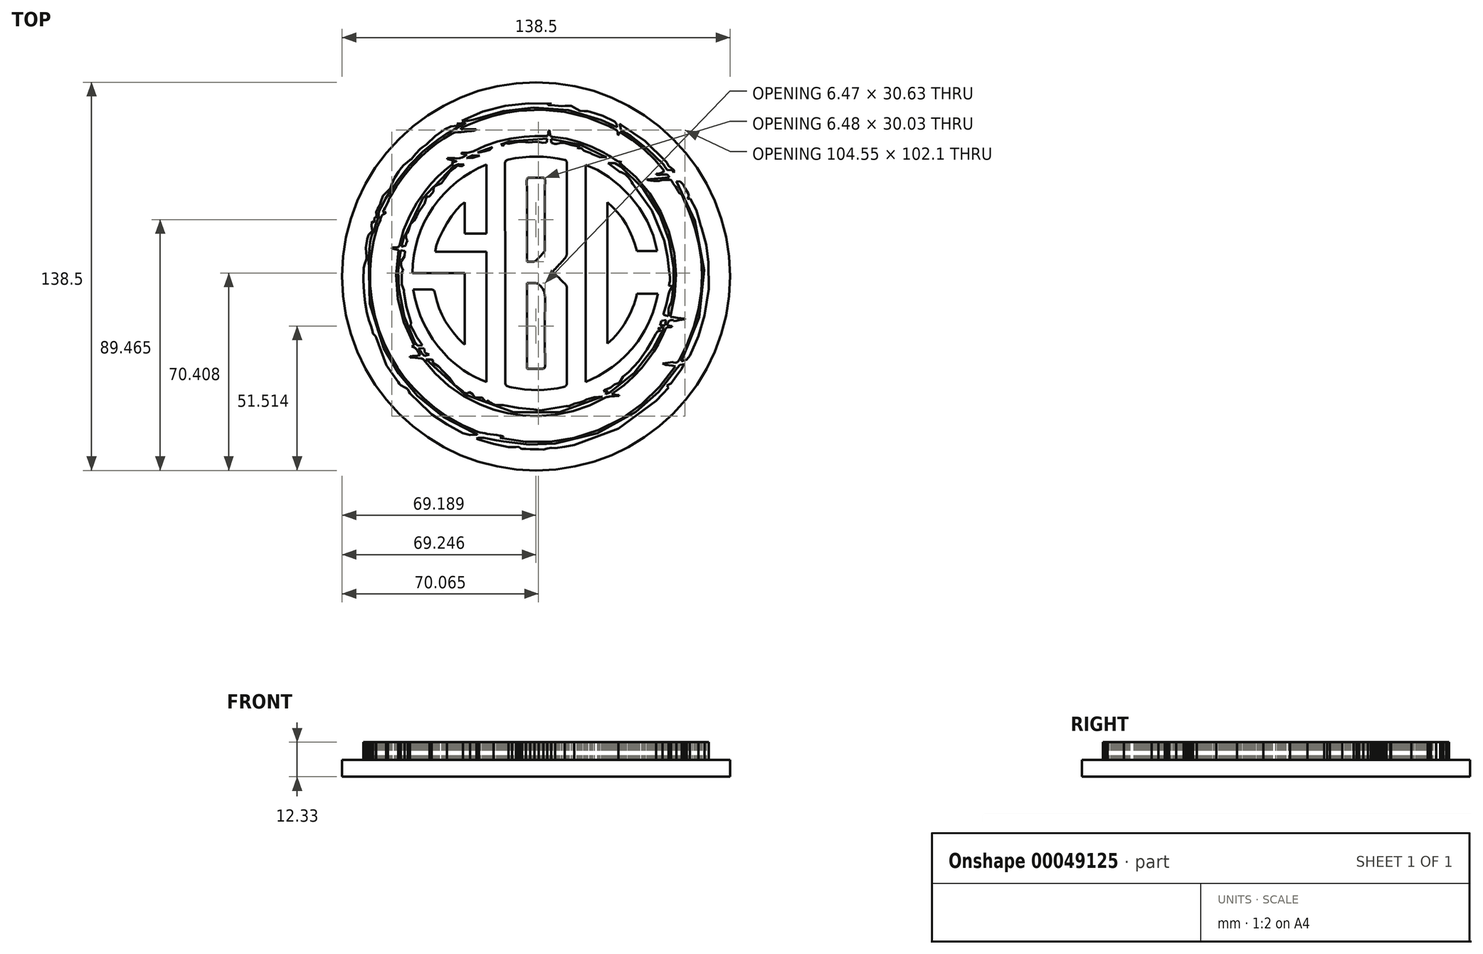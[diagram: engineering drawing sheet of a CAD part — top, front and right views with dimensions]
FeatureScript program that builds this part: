
annotation { "Feature Type Name" : "Feature", "Feature Type Description" : "" }
export const myFeature = defineFeature(function(context is Context, id is Id, definition is map)
    precondition{}
    {
        {
            var Q0;
            Q0=qCreatedBy(makeId("Top.planeOp"),FACE);
            var sketch = newSketch(context, id + "F0", { "sketchPlane" : qUnion([Q0])});
            skLineSegment(sketch, "E0", {"start": v(-53.55, 22.87) * mm, "end": v(-53.9, 22.9) * mm});
            skLineSegment(sketch, "E1", {"start": v(-53.9, 22.9) * mm, "end": v(-54.2, 22.94) * mm});
            skLineSegment(sketch, "E2", {"start": v(-54.2, 22.94) * mm, "end": v(-54.48, 22.97) * mm});
            skLineSegment(sketch, "E3", {"start": v(-54.48, 22.97) * mm, "end": v(-54.75, 23) * mm});
            skLineSegment(sketch, "E4", {"start": v(-54.75, 23) * mm, "end": v(-54.33, 23.74) * mm});
            skLineSegment(sketch, "E5", {"start": v(-54.33, 23.74) * mm, "end": v(-53.9, 24.47) * mm});
            skLineSegment(sketch, "E6", {"start": v(-53.9, 24.47) * mm, "end": v(-53.5, 25.2) * mm});
            skLineSegment(sketch, "E7", {"start": v(-53.5, 25.2) * mm, "end": v(-53.1, 25.95) * mm});
            skLineSegment(sketch, "E8", {"start": v(-53.1, 25.95) * mm, "end": v(-52.87, 26.48) * mm});
            skLineSegment(sketch, "E9", {"start": v(-52.87, 26.48) * mm, "end": v(-52.68, 27.03) * mm});
            skLineSegment(sketch, "E10", {"start": v(-52.68, 27.03) * mm, "end": v(-52.47, 27.58) * mm});
            skLineSegment(sketch, "E11", {"start": v(-52.47, 27.58) * mm, "end": v(-52.23, 28.1) * mm});
            skLineSegment(sketch, "E12", {"start": v(-52.23, 28.1) * mm, "end": v(-49.87, 32.12) * mm});
            skLineSegment(sketch, "E13", {"start": v(-49.87, 32.12) * mm, "end": v(-47.2, 35.9) * mm});
            skLineSegment(sketch, "E14", {"start": v(-47.2, 35.9) * mm, "end": v(-44.24, 39.46) * mm});
            skLineSegment(sketch, "E15", {"start": v(-44.24, 39.46) * mm, "end": v(-41, 42.8) * mm});
            skLineSegment(sketch, "E16", {"start": v(-41, 42.8) * mm, "end": v(-38.46, 45.1) * mm});
            skLineSegment(sketch, "E17", {"start": v(-38.46, 45.1) * mm, "end": v(-35.8, 47.26) * mm});
            skLineSegment(sketch, "E18", {"start": v(-35.8, 47.26) * mm, "end": v(-33, 49.21) * mm});
            skLineSegment(sketch, "E19", {"start": v(-33, 49.21) * mm, "end": v(-30.05, 50.93) * mm});
            skLineSegment(sketch, "E20", {"start": v(-30.05, 50.93) * mm, "end": v(-29.02, 51.28) * mm});
            skLineSegment(sketch, "E21", {"start": v(-29.02, 51.28) * mm, "end": v(-27.88, 51.44) * mm});
            skLineSegment(sketch, "E22", {"start": v(-27.88, 51.44) * mm, "end": v(-26.7, 51.5) * mm});
            skLineSegment(sketch, "E23", {"start": v(-26.7, 51.5) * mm, "end": v(-25.54, 51.6) * mm});
            skLineSegment(sketch, "E24", {"start": v(-25.54, 51.6) * mm, "end": v(-24.72, 51.7) * mm});
            skLineSegment(sketch, "E25", {"start": v(-24.72, 51.7) * mm, "end": v(-23.91, 51.8) * mm});
            skLineSegment(sketch, "E26", {"start": v(-23.91, 51.8) * mm, "end": v(-23.1, 51.9) * mm});
            skLineSegment(sketch, "E27", {"start": v(-23.1, 51.9) * mm, "end": v(-22.29, 52.01) * mm});
            skLineSegment(sketch, "E28", {"start": v(-22.29, 52.01) * mm, "end": v(-22.06, 52.06) * mm});
            skLineSegment(sketch, "E29", {"start": v(-22.06, 52.06) * mm, "end": v(-21.84, 52.14) * mm});
            skLineSegment(sketch, "E30", {"start": v(-21.84, 52.14) * mm, "end": v(-21.62, 52.23) * mm});
            skLineSegment(sketch, "E31", {"start": v(-21.62, 52.23) * mm, "end": v(-21.4, 52.31) * mm});
            skLineSegment(sketch, "E32", {"start": v(-21.4, 52.31) * mm, "end": v(-21.4, 52.37) * mm});
            skLineSegment(sketch, "E33", {"start": v(-21.4, 52.37) * mm, "end": v(-21.41, 52.43) * mm});
            skLineSegment(sketch, "E34", {"start": v(-21.41, 52.43) * mm, "end": v(-21.42, 52.49) * mm});
            skLineSegment(sketch, "E35", {"start": v(-21.42, 52.49) * mm, "end": v(-21.42, 52.54) * mm});
            skLineSegment(sketch, "E36", {"start": v(-21.42, 52.54) * mm, "end": v(-22.76, 52.54) * mm});
            skLineSegment(sketch, "E37", {"start": v(-22.76, 52.54) * mm, "end": v(-24.1, 52.54) * mm});
            skLineSegment(sketch, "E38", {"start": v(-24.1, 52.54) * mm, "end": v(-25.44, 52.54) * mm});
            skLineSegment(sketch, "E39", {"start": v(-25.44, 52.54) * mm, "end": v(-26.78, 52.54) * mm});
            skLineSegment(sketch, "E40", {"start": v(-26.78, 52.54) * mm, "end": v(-26.8, 52.61) * mm});
            skLineSegment(sketch, "E41", {"start": v(-26.8, 52.61) * mm, "end": v(-26.8, 52.68) * mm});
            skLineSegment(sketch, "E42", {"start": v(-26.8, 52.68) * mm, "end": v(-26.82, 52.74) * mm});
            skLineSegment(sketch, "E43", {"start": v(-26.82, 52.74) * mm, "end": v(-26.83, 52.81) * mm});
            skLineSegment(sketch, "E44", {"start": v(-26.83, 52.81) * mm, "end": v(-26.31, 53.08) * mm});
            skLineSegment(sketch, "E45", {"start": v(-26.31, 53.08) * mm, "end": v(-25.8, 53.35) * mm});
            skLineSegment(sketch, "E46", {"start": v(-25.8, 53.35) * mm, "end": v(-25.27, 53.61) * mm});
            skLineSegment(sketch, "E47", {"start": v(-25.27, 53.61) * mm, "end": v(-24.74, 53.87) * mm});
            skLineSegment(sketch, "E48", {"start": v(-24.74, 53.87) * mm, "end": v(-20.25, 55.7) * mm});
            skLineSegment(sketch, "E49", {"start": v(-20.25, 55.7) * mm, "end": v(-15.66, 57.19) * mm});
            skLineSegment(sketch, "E50", {"start": v(-15.66, 57.19) * mm, "end": v(-10.96, 58.3) * mm});
            skLineSegment(sketch, "E51", {"start": v(-10.96, 58.3) * mm, "end": v(-6.17, 59.06) * mm});
            skLineSegment(sketch, "E52", {"start": v(-6.17, 59.06) * mm, "end": v(2.1, 59.44) * mm});
            skLineSegment(sketch, "E53", {"start": v(2.1, 59.44) * mm, "end": v(10.16, 58.67) * mm});
            skLineSegment(sketch, "E54", {"start": v(10.16, 58.67) * mm, "end": v(18.04, 56.78) * mm});
            skLineSegment(sketch, "E55", {"start": v(18.04, 56.78) * mm, "end": v(25.74, 53.76) * mm});
            skLineSegment(sketch, "E56", {"start": v(25.74, 53.76) * mm, "end": v(26.35, 53.46) * mm});
            skLineSegment(sketch, "E57", {"start": v(26.35, 53.46) * mm, "end": v(26.96, 53.13) * mm});
            skLineSegment(sketch, "E58", {"start": v(26.96, 53.13) * mm, "end": v(27.57, 52.8) * mm});
            skLineSegment(sketch, "E59", {"start": v(27.57, 52.8) * mm, "end": v(28.18, 52.5) * mm});
            skLineSegment(sketch, "E60", {"start": v(28.18, 52.5) * mm, "end": v(28.6, 52.27) * mm});
            skLineSegment(sketch, "E61", {"start": v(28.6, 52.27) * mm, "end": v(28.92, 51.98) * mm});
            skLineSegment(sketch, "E62", {"start": v(28.92, 51.98) * mm, "end": v(29.1, 51.6) * mm});
            skLineSegment(sketch, "E63", {"start": v(29.1, 51.6) * mm, "end": v(29.1, 51.1) * mm});
            skLineSegment(sketch, "E64", {"start": v(29.1, 51.1) * mm, "end": v(29.1, 50.97) * mm});
            skLineSegment(sketch, "E65", {"start": v(29.1, 50.97) * mm, "end": v(29.15, 50.8) * mm});
            skLineSegment(sketch, "E66", {"start": v(29.15, 50.8) * mm, "end": v(29.22, 50.6) * mm});
            skLineSegment(sketch, "E67", {"start": v(29.22, 50.6) * mm, "end": v(29.3, 50.33) * mm});
            skLineSegment(sketch, "E68", {"start": v(29.3, 50.33) * mm, "end": v(29.47, 50.68) * mm});
            skLineSegment(sketch, "E69", {"start": v(29.47, 50.68) * mm, "end": v(29.62, 50.97) * mm});
            skLineSegment(sketch, "E70", {"start": v(29.62, 50.97) * mm, "end": v(29.75, 51.25) * mm});
            skLineSegment(sketch, "E71", {"start": v(29.75, 51.25) * mm, "end": v(29.9, 51.54) * mm});
            skLineSegment(sketch, "E72", {"start": v(29.9, 51.54) * mm, "end": v(34.35, 48.61) * mm});
            skLineSegment(sketch, "E73", {"start": v(34.35, 48.61) * mm, "end": v(38.5, 45.35) * mm});
            skLineSegment(sketch, "E74", {"start": v(38.5, 45.35) * mm, "end": v(42.34, 41.72) * mm});
            skLineSegment(sketch, "E75", {"start": v(42.34, 41.72) * mm, "end": v(45.83, 37.66) * mm});
            skLineSegment(sketch, "E76", {"start": v(45.83, 37.66) * mm, "end": v(45.5, 37.43) * mm});
            skLineSegment(sketch, "E77", {"start": v(45.5, 37.43) * mm, "end": v(45.17, 37.19) * mm});
            skLineSegment(sketch, "E78", {"start": v(45.17, 37.19) * mm, "end": v(44.83, 36.97) * mm});
            skLineSegment(sketch, "E79", {"start": v(44.83, 36.97) * mm, "end": v(44.48, 36.8) * mm});
            skLineSegment(sketch, "E80", {"start": v(44.48, 36.8) * mm, "end": v(44.09, 36.7) * mm});
            skLineSegment(sketch, "E81", {"start": v(44.09, 36.7) * mm, "end": v(43.68, 36.66) * mm});
            skLineSegment(sketch, "E82", {"start": v(43.68, 36.66) * mm, "end": v(43.26, 36.63) * mm});
            skLineSegment(sketch, "E83", {"start": v(43.26, 36.63) * mm, "end": v(42.85, 36.6) * mm});
            skLineSegment(sketch, "E84", {"start": v(42.85, 36.6) * mm, "end": v(42.85, 36.53) * mm});
            skLineSegment(sketch, "E85", {"start": v(42.85, 36.53) * mm, "end": v(42.84, 36.47) * mm});
            skLineSegment(sketch, "E86", {"start": v(42.84, 36.47) * mm, "end": v(42.84, 36.4) * mm});
            skLineSegment(sketch, "E87", {"start": v(42.84, 36.4) * mm, "end": v(42.84, 36.34) * mm});
            skLineSegment(sketch, "E88", {"start": v(42.84, 36.34) * mm, "end": v(43.05, 36.3) * mm});
            skLineSegment(sketch, "E89", {"start": v(43.05, 36.3) * mm, "end": v(43.27, 36.27) * mm});
            skLineSegment(sketch, "E90", {"start": v(43.27, 36.27) * mm, "end": v(43.48, 36.24) * mm});
            skLineSegment(sketch, "E91", {"start": v(43.48, 36.24) * mm, "end": v(43.7, 36.24) * mm});
            skLineSegment(sketch, "E92", {"start": v(43.7, 36.24) * mm, "end": v(44.27, 36.27) * mm});
            skLineSegment(sketch, "E93", {"start": v(44.27, 36.27) * mm, "end": v(44.85, 36.3) * mm});
            skLineSegment(sketch, "E94", {"start": v(44.85, 36.3) * mm, "end": v(45.43, 36.34) * mm});
            skLineSegment(sketch, "E95", {"start": v(45.43, 36.34) * mm, "end": v(46, 36.4) * mm});
            skLineSegment(sketch, "E96", {"start": v(46, 36.4) * mm, "end": v(46.49, 36.38) * mm});
            skLineSegment(sketch, "E97", {"start": v(46.49, 36.38) * mm, "end": v(46.91, 36.23) * mm});
            skLineSegment(sketch, "E98", {"start": v(46.91, 36.23) * mm, "end": v(47.28, 35.9) * mm});
            skLineSegment(sketch, "E99", {"start": v(47.28, 35.9) * mm, "end": v(47.62, 35.4) * mm});
            skLineSegment(sketch, "E100", {"start": v(47.62, 35.4) * mm, "end": v(45.56, 35.2) * mm});
            skLineSegment(sketch, "E101", {"start": v(45.56, 35.2) * mm, "end": v(43.53, 35) * mm});
            skLineSegment(sketch, "E102", {"start": v(43.53, 35) * mm, "end": v(41.53, 34.8) * mm});
            skLineSegment(sketch, "E103", {"start": v(41.53, 34.8) * mm, "end": v(39.53, 34.6) * mm});
            skLineSegment(sketch, "E104", {"start": v(39.53, 34.6) * mm, "end": v(39.52, 34.56) * mm});
            skLineSegment(sketch, "E105", {"start": v(39.52, 34.56) * mm, "end": v(39.52, 34.52) * mm});
            skLineSegment(sketch, "E106", {"start": v(39.52, 34.52) * mm, "end": v(39.51, 34.48) * mm});
            skLineSegment(sketch, "E107", {"start": v(39.51, 34.48) * mm, "end": v(39.5, 34.44) * mm});
            skLineSegment(sketch, "E108", {"start": v(39.5, 34.44) * mm, "end": v(39.88, 34.4) * mm});
            skLineSegment(sketch, "E109", {"start": v(39.88, 34.4) * mm, "end": v(40.25, 34.35) * mm});
            skLineSegment(sketch, "E110", {"start": v(40.25, 34.35) * mm, "end": v(40.62, 34.3) * mm});
            skLineSegment(sketch, "E111", {"start": v(40.62, 34.3) * mm, "end": v(41, 34.24) * mm});
            skLineSegment(sketch, "E112", {"start": v(41, 34.24) * mm, "end": v(41.94, 34.1) * mm});
            skLineSegment(sketch, "E113", {"start": v(41.94, 34.1) * mm, "end": v(42.87, 34.04) * mm});
            skLineSegment(sketch, "E114", {"start": v(42.87, 34.04) * mm, "end": v(43.81, 34.1) * mm});
            skLineSegment(sketch, "E115", {"start": v(43.81, 34.1) * mm, "end": v(44.76, 34.27) * mm});
            skLineSegment(sketch, "E116", {"start": v(44.76, 34.27) * mm, "end": v(45.45, 34.4) * mm});
            skLineSegment(sketch, "E117", {"start": v(45.45, 34.4) * mm, "end": v(46.16, 34.45) * mm});
            skLineSegment(sketch, "E118", {"start": v(46.16, 34.45) * mm, "end": v(46.88, 34.46) * mm});
            skLineSegment(sketch, "E119", {"start": v(46.88, 34.46) * mm, "end": v(47.6, 34.47) * mm});
            skLineSegment(sketch, "E120", {"start": v(47.6, 34.47) * mm, "end": v(47.9, 34.44) * mm});
            skLineSegment(sketch, "E121", {"start": v(47.9, 34.44) * mm, "end": v(48.17, 34.33) * mm});
            skLineSegment(sketch, "E122", {"start": v(48.17, 34.33) * mm, "end": v(48.4, 34.12) * mm});
            skLineSegment(sketch, "E123", {"start": v(48.4, 34.12) * mm, "end": v(48.57, 33.79) * mm});
            skLineSegment(sketch, "E124", {"start": v(48.57, 33.79) * mm, "end": v(48.8, 33.32) * mm});
            skLineSegment(sketch, "E125", {"start": v(48.8, 33.32) * mm, "end": v(49.1, 32.88) * mm});
            skLineSegment(sketch, "E126", {"start": v(49.1, 32.88) * mm, "end": v(49.44, 32.46) * mm});
            skLineSegment(sketch, "E127", {"start": v(49.44, 32.46) * mm, "end": v(49.8, 32.07) * mm});
            skLineSegment(sketch, "E128", {"start": v(49.8, 32.07) * mm, "end": v(50.25, 31.34) * mm});
            skLineSegment(sketch, "E129", {"start": v(50.25, 31.34) * mm, "end": v(50.59, 30.51) * mm});
            skLineSegment(sketch, "E130", {"start": v(50.59, 30.51) * mm, "end": v(51.06, 29.8) * mm});
            skLineSegment(sketch, "E131", {"start": v(51.06, 29.8) * mm, "end": v(51.93, 29.41) * mm});
            skLineSegment(sketch, "E132", {"start": v(51.93, 29.41) * mm, "end": v(51.96, 29.4) * mm});
            skLineSegment(sketch, "E133", {"start": v(51.96, 29.4) * mm, "end": v(51.98, 29.36) * mm});
            skLineSegment(sketch, "E134", {"start": v(51.98, 29.36) * mm, "end": v(52, 29.3) * mm});
            skLineSegment(sketch, "E135", {"start": v(52, 29.3) * mm, "end": v(52.02, 29.26) * mm});
            skLineSegment(sketch, "E136", {"start": v(52.02, 29.26) * mm, "end": v(53.24, 26.24) * mm});
            skLineSegment(sketch, "E137", {"start": v(53.24, 26.24) * mm, "end": v(54.48, 23.23) * mm});
            skLineSegment(sketch, "E138", {"start": v(54.48, 23.23) * mm, "end": v(55.67, 20.2) * mm});
            skLineSegment(sketch, "E139", {"start": v(55.67, 20.2) * mm, "end": v(56.73, 17.13) * mm});
            skLineSegment(sketch, "E140", {"start": v(56.73, 17.13) * mm, "end": v(58.14, 11.63) * mm});
            skLineSegment(sketch, "E141", {"start": v(58.14, 11.63) * mm, "end": v(58.96, 6.05) * mm});
            skLineSegment(sketch, "E142", {"start": v(58.96, 6.05) * mm, "end": v(59.23, 0.42) * mm});
            skLineSegment(sketch, "E143", {"start": v(59.23, 0.42) * mm, "end": v(58.97, -5.27) * mm});
            skLineSegment(sketch, "E144", {"start": v(58.97, -5.27) * mm, "end": v(58.02, -11.75) * mm});
            skLineSegment(sketch, "E145", {"start": v(58.02, -11.75) * mm, "end": v(56.38, -18) * mm});
            skLineSegment(sketch, "E146", {"start": v(56.38, -18) * mm, "end": v(54.05, -24.02) * mm});
            skLineSegment(sketch, "E147", {"start": v(54.05, -24.02) * mm, "end": v(51.08, -29.84) * mm});
            skLineSegment(sketch, "E148", {"start": v(51.08, -29.84) * mm, "end": v(50.67, -30.45) * mm});
            skLineSegment(sketch, "E149", {"start": v(50.67, -30.45) * mm, "end": v(50.28, -30.76) * mm});
            skLineSegment(sketch, "E150", {"start": v(50.28, -30.76) * mm, "end": v(49.77, -30.8) * mm});
            skLineSegment(sketch, "E151", {"start": v(49.77, -30.8) * mm, "end": v(49.02, -30.65) * mm});
            skLineSegment(sketch, "E152", {"start": v(49.02, -30.65) * mm, "end": v(48.97, -30.64) * mm});
            skLineSegment(sketch, "E153", {"start": v(48.97, -30.64) * mm, "end": v(48.93, -30.62) * mm});
            skLineSegment(sketch, "E154", {"start": v(48.93, -30.62) * mm, "end": v(48.89, -30.61) * mm});
            skLineSegment(sketch, "E155", {"start": v(48.89, -30.61) * mm, "end": v(48.85, -30.61) * mm});
            skLineSegment(sketch, "E156", {"start": v(48.85, -30.61) * mm, "end": v(47.96, -30.73) * mm});
            skLineSegment(sketch, "E157", {"start": v(47.96, -30.73) * mm, "end": v(47.06, -30.86) * mm});
            skLineSegment(sketch, "E158", {"start": v(47.06, -30.86) * mm, "end": v(46.14, -30.98) * mm});
            skLineSegment(sketch, "E159", {"start": v(46.14, -30.98) * mm, "end": v(45.2, -31.11) * mm});
            skLineSegment(sketch, "E160", {"start": v(45.2, -31.11) * mm, "end": v(46.27, -31.6) * mm});
            skLineSegment(sketch, "E161", {"start": v(46.27, -31.6) * mm, "end": v(47.41, -31.78) * mm});
            skLineSegment(sketch, "E162", {"start": v(47.41, -31.78) * mm, "end": v(48.58, -31.86) * mm});
            skLineSegment(sketch, "E163", {"start": v(48.58, -31.86) * mm, "end": v(49.73, -32.09) * mm});
            skLineSegment(sketch, "E164", {"start": v(49.73, -32.09) * mm, "end": v(44.16, -39.36) * mm});
            skLineSegment(sketch, "E165", {"start": v(44.16, -39.36) * mm, "end": v(37.75, -45.58) * mm});
            skLineSegment(sketch, "E166", {"start": v(37.75, -45.58) * mm, "end": v(30.48, -50.73) * mm});
            skLineSegment(sketch, "E167", {"start": v(30.48, -50.73) * mm, "end": v(22.34, -54.8) * mm});
            skLineSegment(sketch, "E168", {"start": v(22.34, -54.8) * mm, "end": v(13.71, -57.6) * mm});
            skLineSegment(sketch, "E169", {"start": v(13.71, -57.6) * mm, "end": v(4.95, -59) * mm});
            skLineSegment(sketch, "E170", {"start": v(4.95, -59) * mm, "end": v(-3.93, -59) * mm});
            skLineSegment(sketch, "E171", {"start": v(-3.93, -59) * mm, "end": v(-12.92, -57.63) * mm});
            skLineSegment(sketch, "E172", {"start": v(-12.92, -57.63) * mm, "end": v(-12.6, -57.53) * mm});
            skLineSegment(sketch, "E173", {"start": v(-12.6, -57.53) * mm, "end": v(-12.26, -57.44) * mm});
            skLineSegment(sketch, "E174", {"start": v(-12.26, -57.44) * mm, "end": v(-11.93, -57.35) * mm});
            skLineSegment(sketch, "E175", {"start": v(-11.93, -57.35) * mm, "end": v(-11.6, -57.25) * mm});
            skLineSegment(sketch, "E176", {"start": v(-11.6, -57.25) * mm, "end": v(-11.6, -57.22) * mm});
            skLineSegment(sketch, "E177", {"start": v(-11.6, -57.22) * mm, "end": v(-11.6, -57.19) * mm});
            skLineSegment(sketch, "E178", {"start": v(-11.6, -57.19) * mm, "end": v(-11.59, -57.16) * mm});
            skLineSegment(sketch, "E179", {"start": v(-11.59, -57.16) * mm, "end": v(-11.58, -57.12) * mm});
            skLineSegment(sketch, "E180", {"start": v(-11.58, -57.12) * mm, "end": v(-11.85, -57.07) * mm});
            skLineSegment(sketch, "E181", {"start": v(-11.85, -57.07) * mm, "end": v(-12.1, -57.02) * mm});
            skLineSegment(sketch, "E182", {"start": v(-12.1, -57.02) * mm, "end": v(-12.37, -56.96) * mm});
            skLineSegment(sketch, "E183", {"start": v(-12.37, -56.96) * mm, "end": v(-12.63, -56.91) * mm});
            skLineSegment(sketch, "E184", {"start": v(-12.63, -56.91) * mm, "end": v(-12.7, -56.9) * mm});
            skLineSegment(sketch, "E185", {"start": v(-12.7, -56.9) * mm, "end": v(-12.76, -56.9) * mm});
            skLineSegment(sketch, "E186", {"start": v(-12.76, -56.9) * mm, "end": v(-12.83, -56.9) * mm});
            skLineSegment(sketch, "E187", {"start": v(-12.83, -56.9) * mm, "end": v(-12.9, -56.88) * mm});
            skLineSegment(sketch, "E188", {"start": v(-12.9, -56.88) * mm, "end": v(-14, -56.57) * mm});
            skLineSegment(sketch, "E189", {"start": v(-14, -56.57) * mm, "end": v(-15.15, -56.46) * mm});
            skLineSegment(sketch, "E190", {"start": v(-15.15, -56.46) * mm, "end": v(-16.3, -56.4) * mm});
            skLineSegment(sketch, "E191", {"start": v(-16.3, -56.4) * mm, "end": v(-17.4, -56.22) * mm});
            skLineSegment(sketch, "E192", {"start": v(-17.4, -56.22) * mm, "end": v(-18.27, -56.04) * mm});
            skLineSegment(sketch, "E193", {"start": v(-18.27, -56.04) * mm, "end": v(-19.14, -55.9) * mm});
            skLineSegment(sketch, "E194", {"start": v(-19.14, -55.9) * mm, "end": v(-20, -55.7) * mm});
            skLineSegment(sketch, "E195", {"start": v(-20, -55.7) * mm, "end": v(-20.85, -55.41) * mm});
            skLineSegment(sketch, "E196", {"start": v(-20.85, -55.41) * mm, "end": v(-21.72, -55.03) * mm});
            skLineSegment(sketch, "E197", {"start": v(-21.72, -55.03) * mm, "end": v(-22.6, -54.67) * mm});
            skLineSegment(sketch, "E198", {"start": v(-22.6, -54.67) * mm, "end": v(-23.5, -54.3) * mm});
            skLineSegment(sketch, "E199", {"start": v(-23.5, -54.3) * mm, "end": v(-24.37, -53.93) * mm});
            skLineSegment(sketch, "E200", {"start": v(-24.37, -53.93) * mm, "end": v(-25.24, -53.54) * mm});
            skLineSegment(sketch, "E201", {"start": v(-25.24, -53.54) * mm, "end": v(-26.1, -53.13) * mm});
            skLineSegment(sketch, "E202", {"start": v(-26.1, -53.13) * mm, "end": v(-26.96, -52.7) * mm});
            skLineSegment(sketch, "E203", {"start": v(-26.96, -52.7) * mm, "end": v(-27.8, -52.27) * mm});
            skLineSegment(sketch, "E204", {"start": v(-27.8, -52.27) * mm, "end": v(-32.17, -49.71) * mm});
            skLineSegment(sketch, "E205", {"start": v(-32.17, -49.71) * mm, "end": v(-36.27, -46.8) * mm});
            skLineSegment(sketch, "E206", {"start": v(-36.27, -46.8) * mm, "end": v(-40.11, -43.57) * mm});
            skLineSegment(sketch, "E207", {"start": v(-40.11, -43.57) * mm, "end": v(-43.7, -40) * mm});
            skLineSegment(sketch, "E208", {"start": v(-43.7, -40) * mm, "end": v(-46.75, -36.4) * mm});
            skLineSegment(sketch, "E209", {"start": v(-46.75, -36.4) * mm, "end": v(-49.5, -32.6) * mm});
            skLineSegment(sketch, "E210", {"start": v(-49.5, -32.6) * mm, "end": v(-51.93, -28.58) * mm});
            skLineSegment(sketch, "E211", {"start": v(-51.93, -28.58) * mm, "end": v(-54.04, -24.35) * mm});
            skLineSegment(sketch, "E212", {"start": v(-54.04, -24.35) * mm, "end": v(-56.06, -19.25) * mm});
            skLineSegment(sketch, "E213", {"start": v(-56.06, -19.25) * mm, "end": v(-57.6, -14.04) * mm});
            skLineSegment(sketch, "E214", {"start": v(-57.6, -14.04) * mm, "end": v(-58.64, -8.7) * mm});
            skLineSegment(sketch, "E215", {"start": v(-58.64, -8.7) * mm, "end": v(-59.2, -3.25) * mm});
            skLineSegment(sketch, "E216", {"start": v(-59.2, -3.25) * mm, "end": v(-59.26, 2.15) * mm});
            skLineSegment(sketch, "E217", {"start": v(-59.26, 2.15) * mm, "end": v(-58.83, 7.48) * mm});
            skLineSegment(sketch, "E218", {"start": v(-58.83, 7.48) * mm, "end": v(-57.93, 12.76) * mm});
            skLineSegment(sketch, "E219", {"start": v(-57.93, 12.76) * mm, "end": v(-56.58, 17.97) * mm});
            skLineSegment(sketch, "E220", {"start": v(-56.58, 17.97) * mm, "end": v(-56.58, 18) * mm});
            skLineSegment(sketch, "E221", {"start": v(-56.58, 18) * mm, "end": v(-56.57, 18.01) * mm});
            skLineSegment(sketch, "E222", {"start": v(-56.57, 18.01) * mm, "end": v(-56.56, 18.04) * mm});
            skLineSegment(sketch, "E223", {"start": v(-56.56, 18.04) * mm, "end": v(-56.55, 18.06) * mm});
            skLineSegment(sketch, "E224", {"start": v(-56.55, 18.06) * mm, "end": v(-56.21, 18.74) * mm});
            skLineSegment(sketch, "E225", {"start": v(-56.21, 18.74) * mm, "end": v(-55.85, 19.42) * mm});
            skLineSegment(sketch, "E226", {"start": v(-55.85, 19.42) * mm, "end": v(-55.54, 20.12) * mm});
            skLineSegment(sketch, "E227", {"start": v(-55.54, 20.12) * mm, "end": v(-55.38, 20.9) * mm});
            skLineSegment(sketch, "E228", {"start": v(-55.38, 20.9) * mm, "end": v(-55.24, 21.44) * mm});
            skLineSegment(sketch, "E229", {"start": v(-55.24, 21.44) * mm, "end": v(-54.94, 21.86) * mm});
            skLineSegment(sketch, "E230", {"start": v(-54.94, 21.86) * mm, "end": v(-54.51, 22.18) * mm});
            skLineSegment(sketch, "E231", {"start": v(-54.51, 22.18) * mm, "end": v(-54.02, 22.44) * mm});
            skLineSegment(sketch, "E232", {"start": v(-54.02, 22.44) * mm, "end": v(-53.92, 22.5) * mm});
            skLineSegment(sketch, "E233", {"start": v(-53.92, 22.5) * mm, "end": v(-53.82, 22.6) * mm});
            skLineSegment(sketch, "E234", {"start": v(-53.82, 22.6) * mm, "end": v(-53.7, 22.72) * mm});
            skLineSegment(sketch, "E235", {"start": v(-53.7, 22.72) * mm, "end": v(-53.55, 22.87) * mm});
            skLineSegment(sketch, "E236", {"start": v(27, -42.03) * mm, "end": v(27.25, -41.85) * mm});
            skLineSegment(sketch, "E237", {"start": v(27.25, -41.85) * mm, "end": v(27.46, -41.7) * mm});
            skLineSegment(sketch, "E238", {"start": v(27.46, -41.7) * mm, "end": v(27.65, -41.56) * mm});
            skLineSegment(sketch, "E239", {"start": v(27.65, -41.56) * mm, "end": v(27.83, -41.43) * mm});
            skLineSegment(sketch, "E240", {"start": v(27.83, -41.43) * mm, "end": v(31.4, -38.77) * mm});
            skLineSegment(sketch, "E241", {"start": v(31.4, -38.77) * mm, "end": v(34.7, -35.83) * mm});
            skLineSegment(sketch, "E242", {"start": v(34.7, -35.83) * mm, "end": v(37.74, -32.61) * mm});
            skLineSegment(sketch, "E243", {"start": v(37.74, -32.61) * mm, "end": v(40.5, -29.1) * mm});
            skLineSegment(sketch, "E244", {"start": v(40.5, -29.1) * mm, "end": v(42.11, -26.73) * mm});
            skLineSegment(sketch, "E245", {"start": v(42.11, -26.73) * mm, "end": v(43.58, -24.28) * mm});
            skLineSegment(sketch, "E246", {"start": v(43.58, -24.28) * mm, "end": v(44.9, -21.74) * mm});
            skLineSegment(sketch, "E247", {"start": v(44.9, -21.74) * mm, "end": v(46.06, -19.12) * mm});
            skLineSegment(sketch, "E248", {"start": v(46.06, -19.12) * mm, "end": v(46.27, -18.68) * mm});
            skLineSegment(sketch, "E249", {"start": v(46.27, -18.68) * mm, "end": v(46.54, -18.36) * mm});
            skLineSegment(sketch, "E250", {"start": v(46.54, -18.36) * mm, "end": v(46.9, -18.17) * mm});
            skLineSegment(sketch, "E251", {"start": v(46.9, -18.17) * mm, "end": v(47.4, -18.14) * mm});
            skLineSegment(sketch, "E252", {"start": v(47.4, -18.14) * mm, "end": v(47.7, -18.14) * mm});
            skLineSegment(sketch, "E253", {"start": v(47.7, -18.14) * mm, "end": v(48, -18.09) * mm});
            skLineSegment(sketch, "E254", {"start": v(48, -18.09) * mm, "end": v(48.32, -18.02) * mm});
            skLineSegment(sketch, "E255", {"start": v(48.32, -18.02) * mm, "end": v(48.63, -17.96) * mm});
            skLineSegment(sketch, "E256", {"start": v(48.63, -17.96) * mm, "end": v(48.62, -17.91) * mm});
            skLineSegment(sketch, "E257", {"start": v(48.62, -17.91) * mm, "end": v(48.62, -17.86) * mm});
            skLineSegment(sketch, "E258", {"start": v(48.62, -17.86) * mm, "end": v(48.62, -17.81) * mm});
            skLineSegment(sketch, "E259", {"start": v(48.62, -17.81) * mm, "end": v(48.61, -17.76) * mm});
            skLineSegment(sketch, "E260", {"start": v(48.61, -17.76) * mm, "end": v(48.16, -17.71) * mm});
            skLineSegment(sketch, "E261", {"start": v(48.16, -17.71) * mm, "end": v(47.71, -17.66) * mm});
            skLineSegment(sketch, "E262", {"start": v(47.71, -17.66) * mm, "end": v(47.26, -17.61) * mm});
            skLineSegment(sketch, "E263", {"start": v(47.26, -17.61) * mm, "end": v(46.8, -17.56) * mm});
            skLineSegment(sketch, "E264", {"start": v(46.8, -17.56) * mm, "end": v(47.1, -16.5) * mm});
            skLineSegment(sketch, "E265", {"start": v(47.1, -16.5) * mm, "end": v(47.5, -15.9) * mm});
            skLineSegment(sketch, "E266", {"start": v(47.5, -15.9) * mm, "end": v(48.13, -15.63) * mm});
            skLineSegment(sketch, "E267", {"start": v(48.13, -15.63) * mm, "end": v(49.14, -15.58) * mm});
            skLineSegment(sketch, "E268", {"start": v(49.14, -15.58) * mm, "end": v(49.12, -15.7) * mm});
            skLineSegment(sketch, "E269", {"start": v(49.12, -15.7) * mm, "end": v(49.1, -15.83) * mm});
            skLineSegment(sketch, "E270", {"start": v(49.1, -15.83) * mm, "end": v(49.09, -15.93) * mm});
            skLineSegment(sketch, "E271", {"start": v(49.09, -15.93) * mm, "end": v(49.08, -16) * mm});
            skLineSegment(sketch, "E272", {"start": v(49.08, -16) * mm, "end": v(50.1, -15.82) * mm});
            skLineSegment(sketch, "E273", {"start": v(50.1, -15.82) * mm, "end": v(51.1, -15.65) * mm});
            skLineSegment(sketch, "E274", {"start": v(51.1, -15.65) * mm, "end": v(52.1, -15.48) * mm});
            skLineSegment(sketch, "E275", {"start": v(52.1, -15.48) * mm, "end": v(53.09, -15.31) * mm});
            skLineSegment(sketch, "E276", {"start": v(53.09, -15.31) * mm, "end": v(53.09, -15.27) * mm});
            skLineSegment(sketch, "E277", {"start": v(53.09, -15.27) * mm, "end": v(53.09, -15.23) * mm});
            skLineSegment(sketch, "E278", {"start": v(53.09, -15.23) * mm, "end": v(53.09, -15.19) * mm});
            skLineSegment(sketch, "E279", {"start": v(53.09, -15.19) * mm, "end": v(53.09, -15.14) * mm});
            skLineSegment(sketch, "E280", {"start": v(53.09, -15.14) * mm, "end": v(51.78, -14.96) * mm});
            skLineSegment(sketch, "E281", {"start": v(51.78, -14.96) * mm, "end": v(50.48, -14.77) * mm});
            skLineSegment(sketch, "E282", {"start": v(50.48, -14.77) * mm, "end": v(49.2, -14.6) * mm});
            skLineSegment(sketch, "E283", {"start": v(49.2, -14.6) * mm, "end": v(47.9, -14.4) * mm});
            skLineSegment(sketch, "E284", {"start": v(47.9, -14.4) * mm, "end": v(49.47, -6.82) * mm});
            skLineSegment(sketch, "E285", {"start": v(49.47, -6.82) * mm, "end": v(49.94, 0.75) * mm});
            skLineSegment(sketch, "E286", {"start": v(49.94, 0.75) * mm, "end": v(49.28, 8.3) * mm});
            skLineSegment(sketch, "E287", {"start": v(49.28, 8.3) * mm, "end": v(47.44, 15.84) * mm});
            skLineSegment(sketch, "E288", {"start": v(47.44, 15.84) * mm, "end": v(44.48, 23.06) * mm});
            skLineSegment(sketch, "E289", {"start": v(44.48, 23.06) * mm, "end": v(40.53, 29.6) * mm});
            skLineSegment(sketch, "E290", {"start": v(40.53, 29.6) * mm, "end": v(35.59, 35.45) * mm});
            skLineSegment(sketch, "E291", {"start": v(35.59, 35.45) * mm, "end": v(29.67, 40.65) * mm});
            skLineSegment(sketch, "E292", {"start": v(29.67, 40.65) * mm, "end": v(29.96, 40.7) * mm});
            skLineSegment(sketch, "E293", {"start": v(29.96, 40.7) * mm, "end": v(30.2, 40.76) * mm});
            skLineSegment(sketch, "E294", {"start": v(30.2, 40.76) * mm, "end": v(30.4, 40.8) * mm});
            skLineSegment(sketch, "E295", {"start": v(30.4, 40.8) * mm, "end": v(30.58, 40.84) * mm});
            skLineSegment(sketch, "E296", {"start": v(30.58, 40.84) * mm, "end": v(29.26, 41.08) * mm});
            skLineSegment(sketch, "E297", {"start": v(29.26, 41.08) * mm, "end": v(28.1, 41.67) * mm});
            skLineSegment(sketch, "E298", {"start": v(28.1, 41.67) * mm, "end": v(27.04, 42.41) * mm});
            skLineSegment(sketch, "E299", {"start": v(27.04, 42.41) * mm, "end": v(25.95, 43.1) * mm});
            skLineSegment(sketch, "E300", {"start": v(25.95, 43.1) * mm, "end": v(25.54, 43.33) * mm});
            skLineSegment(sketch, "E301", {"start": v(25.54, 43.33) * mm, "end": v(25.14, 43.57) * mm});
            skLineSegment(sketch, "E302", {"start": v(25.14, 43.57) * mm, "end": v(24.74, 43.82) * mm});
            skLineSegment(sketch, "E303", {"start": v(24.74, 43.82) * mm, "end": v(24.34, 44.05) * mm});
            skLineSegment(sketch, "E304", {"start": v(24.34, 44.05) * mm, "end": v(19.93, 46.2) * mm});
            skLineSegment(sketch, "E305", {"start": v(19.93, 46.2) * mm, "end": v(15.38, 47.9) * mm});
            skLineSegment(sketch, "E306", {"start": v(15.38, 47.9) * mm, "end": v(10.68, 49.13) * mm});
            skLineSegment(sketch, "E307", {"start": v(10.68, 49.13) * mm, "end": v(5.82, 49.85) * mm});
            skLineSegment(sketch, "E308", {"start": v(5.82, 49.85) * mm, "end": v(5.44, 49.93) * mm});
            skLineSegment(sketch, "E309", {"start": v(5.44, 49.93) * mm, "end": v(5.19, 50.09) * mm});
            skLineSegment(sketch, "E310", {"start": v(5.19, 50.09) * mm, "end": v(5.03, 50.34) * mm});
            skLineSegment(sketch, "E311", {"start": v(5.03, 50.34) * mm, "end": v(4.96, 50.7) * mm});
            skLineSegment(sketch, "E312", {"start": v(4.96, 50.7) * mm, "end": v(4.92, 51.08) * mm});
            skLineSegment(sketch, "E313", {"start": v(4.92, 51.08) * mm, "end": v(4.86, 51.46) * mm});
            skLineSegment(sketch, "E314", {"start": v(4.86, 51.46) * mm, "end": v(4.8, 51.83) * mm});
            skLineSegment(sketch, "E315", {"start": v(4.8, 51.83) * mm, "end": v(4.73, 52.2) * mm});
            skLineSegment(sketch, "E316", {"start": v(4.73, 52.2) * mm, "end": v(4.56, 51.87) * mm});
            skLineSegment(sketch, "E317", {"start": v(4.56, 51.87) * mm, "end": v(4.45, 51.54) * mm});
            skLineSegment(sketch, "E318", {"start": v(4.45, 51.54) * mm, "end": v(4.38, 51.21) * mm});
            skLineSegment(sketch, "E319", {"start": v(4.38, 51.21) * mm, "end": v(4.36, 50.89) * mm});
            skLineSegment(sketch, "E320", {"start": v(4.36, 50.89) * mm, "end": v(4.3, 50.42) * mm});
            skLineSegment(sketch, "E321", {"start": v(4.3, 50.42) * mm, "end": v(4.1, 50.16) * mm});
            skLineSegment(sketch, "E322", {"start": v(4.1, 50.16) * mm, "end": v(3.77, 50.04) * mm});
            skLineSegment(sketch, "E323", {"start": v(3.77, 50.04) * mm, "end": v(3.31, 50.02) * mm});
            skLineSegment(sketch, "E324", {"start": v(3.31, 50.02) * mm, "end": v(1.42, 50.03) * mm});
            skLineSegment(sketch, "E325", {"start": v(1.42, 50.03) * mm, "end": v(-0.47, 50.02) * mm});
            skLineSegment(sketch, "E326", {"start": v(-0.47, 50.02) * mm, "end": v(-2.35, 49.98) * mm});
            skLineSegment(sketch, "E327", {"start": v(-2.35, 49.98) * mm, "end": v(-4.23, 49.87) * mm});
            skLineSegment(sketch, "E328", {"start": v(-4.23, 49.87) * mm, "end": v(-8.98, 49.23) * mm});
            skLineSegment(sketch, "E329", {"start": v(-8.98, 49.23) * mm, "end": v(-13.6, 48.12) * mm});
            skLineSegment(sketch, "E330", {"start": v(-13.6, 48.12) * mm, "end": v(-18.1, 46.58) * mm});
            skLineSegment(sketch, "E331", {"start": v(-18.1, 46.58) * mm, "end": v(-22.47, 44.6) * mm});
            skLineSegment(sketch, "E332", {"start": v(-22.47, 44.6) * mm, "end": v(-22.92, 44.42) * mm});
            skLineSegment(sketch, "E333", {"start": v(-22.92, 44.42) * mm, "end": v(-23.41, 44.3) * mm});
            skLineSegment(sketch, "E334", {"start": v(-23.41, 44.3) * mm, "end": v(-23.91, 44.21) * mm});
            skLineSegment(sketch, "E335", {"start": v(-23.91, 44.21) * mm, "end": v(-24.41, 44.15) * mm});
            skLineSegment(sketch, "E336", {"start": v(-24.41, 44.15) * mm, "end": v(-24.97, 44.12) * mm});
            skLineSegment(sketch, "E337", {"start": v(-24.97, 44.12) * mm, "end": v(-25.53, 44.11) * mm});
            skLineSegment(sketch, "E338", {"start": v(-25.53, 44.11) * mm, "end": v(-26.09, 44.13) * mm});
            skLineSegment(sketch, "E339", {"start": v(-26.09, 44.13) * mm, "end": v(-26.65, 44.13) * mm});
            skLineSegment(sketch, "E340", {"start": v(-26.65, 44.13) * mm, "end": v(-26.66, 44.06) * mm});
            skLineSegment(sketch, "E341", {"start": v(-26.66, 44.06) * mm, "end": v(-26.66, 43.98) * mm});
            skLineSegment(sketch, "E342", {"start": v(-26.66, 43.98) * mm, "end": v(-26.67, 43.9) * mm});
            skLineSegment(sketch, "E343", {"start": v(-26.67, 43.9) * mm, "end": v(-26.68, 43.82) * mm});
            skLineSegment(sketch, "E344", {"start": v(-26.68, 43.82) * mm, "end": v(-26.23, 43.72) * mm});
            skLineSegment(sketch, "E345", {"start": v(-26.23, 43.72) * mm, "end": v(-25.77, 43.63) * mm});
            skLineSegment(sketch, "E346", {"start": v(-25.77, 43.63) * mm, "end": v(-25.28, 43.52) * mm});
            skLineSegment(sketch, "E347", {"start": v(-25.28, 43.52) * mm, "end": v(-24.75, 43.41) * mm});
            skLineSegment(sketch, "E348", {"start": v(-24.75, 43.41) * mm, "end": v(-25.58, 42.88) * mm});
            skLineSegment(sketch, "E349", {"start": v(-25.58, 42.88) * mm, "end": v(-26.38, 42.44) * mm});
            skLineSegment(sketch, "E350", {"start": v(-26.38, 42.44) * mm, "end": v(-27.21, 42.17) * mm});
            skLineSegment(sketch, "E351", {"start": v(-27.21, 42.17) * mm, "end": v(-28.13, 42.12) * mm});
            skLineSegment(sketch, "E352", {"start": v(-28.13, 42.12) * mm, "end": v(-29.02, 42.17) * mm});
            skLineSegment(sketch, "E353", {"start": v(-29.02, 42.17) * mm, "end": v(-29.9, 42.18) * mm});
            skLineSegment(sketch, "E354", {"start": v(-29.9, 42.18) * mm, "end": v(-30.8, 42.16) * mm});
            skLineSegment(sketch, "E355", {"start": v(-30.8, 42.16) * mm, "end": v(-31.7, 42.15) * mm});
            skLineSegment(sketch, "E356", {"start": v(-31.7, 42.15) * mm, "end": v(-31.7, 42.06) * mm});
            skLineSegment(sketch, "E357", {"start": v(-31.7, 42.06) * mm, "end": v(-31.7, 41.97) * mm});
            skLineSegment(sketch, "E358", {"start": v(-31.7, 41.97) * mm, "end": v(-31.7, 41.88) * mm});
            skLineSegment(sketch, "E359", {"start": v(-31.7, 41.88) * mm, "end": v(-31.7, 41.79) * mm});
            skLineSegment(sketch, "E360", {"start": v(-31.7, 41.79) * mm, "end": v(-30.88, 41.65) * mm});
            skLineSegment(sketch, "E361", {"start": v(-30.88, 41.65) * mm, "end": v(-30.06, 41.5) * mm});
            skLineSegment(sketch, "E362", {"start": v(-30.06, 41.5) * mm, "end": v(-29.23, 41.36) * mm});
            skLineSegment(sketch, "E363", {"start": v(-29.23, 41.36) * mm, "end": v(-28.41, 41.22) * mm});
            skLineSegment(sketch, "E364", {"start": v(-28.41, 41.22) * mm, "end": v(-28.4, 41.17) * mm});
            skLineSegment(sketch, "E365", {"start": v(-28.4, 41.17) * mm, "end": v(-28.4, 41.12) * mm});
            skLineSegment(sketch, "E366", {"start": v(-28.4, 41.12) * mm, "end": v(-28.39, 41.07) * mm});
            skLineSegment(sketch, "E367", {"start": v(-28.39, 41.07) * mm, "end": v(-28.38, 41.02) * mm});
            skLineSegment(sketch, "E368", {"start": v(-28.38, 41.02) * mm, "end": v(-28.8, 40.93) * mm});
            skLineSegment(sketch, "E369", {"start": v(-28.8, 40.93) * mm, "end": v(-29.23, 40.84) * mm});
            skLineSegment(sketch, "E370", {"start": v(-29.23, 40.84) * mm, "end": v(-29.66, 40.74) * mm});
            skLineSegment(sketch, "E371", {"start": v(-29.66, 40.74) * mm, "end": v(-30.1, 40.65) * mm});
            skLineSegment(sketch, "E372", {"start": v(-30.1, 40.65) * mm, "end": v(-29.97, 40.54) * mm});
            skLineSegment(sketch, "E373", {"start": v(-29.97, 40.54) * mm, "end": v(-29.84, 40.45) * mm});
            skLineSegment(sketch, "E374", {"start": v(-29.84, 40.45) * mm, "end": v(-29.72, 40.35) * mm});
            skLineSegment(sketch, "E375", {"start": v(-29.72, 40.35) * mm, "end": v(-29.6, 40.25) * mm});
            skLineSegment(sketch, "E376", {"start": v(-29.6, 40.25) * mm, "end": v(-29.73, 40.15) * mm});
            skLineSegment(sketch, "E377", {"start": v(-29.73, 40.15) * mm, "end": v(-29.84, 40.05) * mm});
            skLineSegment(sketch, "E378", {"start": v(-29.84, 40.05) * mm, "end": v(-29.95, 39.96) * mm});
            skLineSegment(sketch, "E379", {"start": v(-29.95, 39.96) * mm, "end": v(-30.06, 39.88) * mm});
            skLineSegment(sketch, "E380", {"start": v(-30.06, 39.88) * mm, "end": v(-32.65, 37.8) * mm});
            skLineSegment(sketch, "E381", {"start": v(-32.65, 37.8) * mm, "end": v(-35.09, 35.58) * mm});
            skLineSegment(sketch, "E382", {"start": v(-35.09, 35.58) * mm, "end": v(-37.37, 33.2) * mm});
            skLineSegment(sketch, "E383", {"start": v(-37.37, 33.2) * mm, "end": v(-39.5, 30.65) * mm});
            skLineSegment(sketch, "E384", {"start": v(-39.5, 30.65) * mm, "end": v(-42.63, 26.19) * mm});
            skLineSegment(sketch, "E385", {"start": v(-42.63, 26.19) * mm, "end": v(-45.21, 21.46) * mm});
            skLineSegment(sketch, "E386", {"start": v(-45.21, 21.46) * mm, "end": v(-47.26, 16.48) * mm});
            skLineSegment(sketch, "E387", {"start": v(-47.26, 16.48) * mm, "end": v(-48.75, 11.25) * mm});
            skLineSegment(sketch, "E388", {"start": v(-48.75, 11.25) * mm, "end": v(-48.88, 10.86) * mm});
            skLineSegment(sketch, "E389", {"start": v(-48.88, 10.86) * mm, "end": v(-49.08, 10.59) * mm});
            skLineSegment(sketch, "E390", {"start": v(-49.08, 10.59) * mm, "end": v(-49.36, 10.43) * mm});
            skLineSegment(sketch, "E391", {"start": v(-49.36, 10.43) * mm, "end": v(-49.74, 10.37) * mm});
            skLineSegment(sketch, "E392", {"start": v(-49.74, 10.37) * mm, "end": v(-50.17, 10.34) * mm});
            skLineSegment(sketch, "E393", {"start": v(-50.17, 10.34) * mm, "end": v(-50.6, 10.3) * mm});
            skLineSegment(sketch, "E394", {"start": v(-50.6, 10.3) * mm, "end": v(-51.02, 10.27) * mm});
            skLineSegment(sketch, "E395", {"start": v(-51.02, 10.27) * mm, "end": v(-51.45, 10.23) * mm});
            skLineSegment(sketch, "E396", {"start": v(-51.45, 10.23) * mm, "end": v(-51.45, 10.17) * mm});
            skLineSegment(sketch, "E397", {"start": v(-51.45, 10.17) * mm, "end": v(-51.45, 10.11) * mm});
            skLineSegment(sketch, "E398", {"start": v(-51.45, 10.11) * mm, "end": v(-51.46, 10.05) * mm});
            skLineSegment(sketch, "E399", {"start": v(-51.46, 10.05) * mm, "end": v(-51.46, 10) * mm});
            skLineSegment(sketch, "E400", {"start": v(-51.46, 10) * mm, "end": v(-50.9, 9.87) * mm});
            skLineSegment(sketch, "E401", {"start": v(-50.9, 9.87) * mm, "end": v(-50.32, 9.74) * mm});
            skLineSegment(sketch, "E402", {"start": v(-50.32, 9.74) * mm, "end": v(-49.74, 9.61) * mm});
            skLineSegment(sketch, "E403", {"start": v(-49.74, 9.61) * mm, "end": v(-49.14, 9.48) * mm});
            skLineSegment(sketch, "E404", {"start": v(-49.14, 9.48) * mm, "end": v(-50.03, 0.54) * mm});
            skLineSegment(sketch, "E405", {"start": v(-50.03, 0.54) * mm, "end": v(-49.38, -8.12) * mm});
            skLineSegment(sketch, "E406", {"start": v(-49.38, -8.12) * mm, "end": v(-47.2, -16.5) * mm});
            skLineSegment(sketch, "E407", {"start": v(-47.2, -16.5) * mm, "end": v(-43.54, -24.64) * mm});
            skLineSegment(sketch, "E408", {"start": v(-43.54, -24.64) * mm, "end": v(-43.72, -24.73) * mm});
            skLineSegment(sketch, "E409", {"start": v(-43.72, -24.73) * mm, "end": v(-43.91, -24.82) * mm});
            skLineSegment(sketch, "E410", {"start": v(-43.91, -24.82) * mm, "end": v(-44.12, -24.92) * mm});
            skLineSegment(sketch, "E411", {"start": v(-44.12, -24.92) * mm, "end": v(-44.37, -25.04) * mm});
            skLineSegment(sketch, "E412", {"start": v(-44.37, -25.04) * mm, "end": v(-43.23, -25.48) * mm});
            skLineSegment(sketch, "E413", {"start": v(-43.23, -25.48) * mm, "end": v(-42.5, -26.24) * mm});
            skLineSegment(sketch, "E414", {"start": v(-42.5, -26.24) * mm, "end": v(-41.94, -27.18) * mm});
            skLineSegment(sketch, "E415", {"start": v(-41.94, -27.18) * mm, "end": v(-41.3, -28.1) * mm});
            skLineSegment(sketch, "E416", {"start": v(-41.3, -28.1) * mm, "end": v(-42.31, -28.24) * mm});
            skLineSegment(sketch, "E417", {"start": v(-42.31, -28.24) * mm, "end": v(-43.26, -28.36) * mm});
            skLineSegment(sketch, "E418", {"start": v(-43.26, -28.36) * mm, "end": v(-44.17, -28.47) * mm});
            skLineSegment(sketch, "E419", {"start": v(-44.17, -28.47) * mm, "end": v(-45.06, -28.59) * mm});
            skLineSegment(sketch, "E420", {"start": v(-45.06, -28.59) * mm, "end": v(-45.06, -28.66) * mm});
            skLineSegment(sketch, "E421", {"start": v(-45.06, -28.66) * mm, "end": v(-45.06, -28.74) * mm});
            skLineSegment(sketch, "E422", {"start": v(-45.06, -28.74) * mm, "end": v(-45.06, -28.81) * mm});
            skLineSegment(sketch, "E423", {"start": v(-45.06, -28.81) * mm, "end": v(-45.06, -28.89) * mm});
            skLineSegment(sketch, "E424", {"start": v(-45.06, -28.89) * mm, "end": v(-44.06, -29) * mm});
            skLineSegment(sketch, "E425", {"start": v(-44.06, -29) * mm, "end": v(-43.06, -29.1) * mm});
            skLineSegment(sketch, "E426", {"start": v(-43.06, -29.1) * mm, "end": v(-42.06, -29.2) * mm});
            skLineSegment(sketch, "E427", {"start": v(-42.06, -29.2) * mm, "end": v(-41.06, -29.32) * mm});
            skLineSegment(sketch, "E428", {"start": v(-41.06, -29.32) * mm, "end": v(-40.82, -29.36) * mm});
            skLineSegment(sketch, "E429", {"start": v(-40.82, -29.36) * mm, "end": v(-40.58, -29.43) * mm});
            skLineSegment(sketch, "E430", {"start": v(-40.58, -29.43) * mm, "end": v(-40.36, -29.52) * mm});
            skLineSegment(sketch, "E431", {"start": v(-40.36, -29.52) * mm, "end": v(-40.2, -29.66) * mm});
            skLineSegment(sketch, "E432", {"start": v(-40.2, -29.66) * mm, "end": v(-35.94, -34.68) * mm});
            skLineSegment(sketch, "E433", {"start": v(-35.94, -34.68) * mm, "end": v(-31.16, -39.04) * mm});
            skLineSegment(sketch, "E434", {"start": v(-31.16, -39.04) * mm, "end": v(-25.85, -42.73) * mm});
            skLineSegment(sketch, "E435", {"start": v(-25.85, -42.73) * mm, "end": v(-20, -45.74) * mm});
            skLineSegment(sketch, "E436", {"start": v(-20, -45.74) * mm, "end": v(-15.04, -47.6) * mm});
            skLineSegment(sketch, "E437", {"start": v(-15.04, -47.6) * mm, "end": v(-9.97, -48.92) * mm});
            skLineSegment(sketch, "E438", {"start": v(-9.97, -48.92) * mm, "end": v(-4.8, -49.68) * mm});
            skLineSegment(sketch, "E439", {"start": v(-4.8, -49.68) * mm, "end": v(0.48, -49.9) * mm});
            skLineSegment(sketch, "E440", {"start": v(0.48, -49.9) * mm, "end": v(6.93, -49.42) * mm});
            skLineSegment(sketch, "E441", {"start": v(6.93, -49.42) * mm, "end": v(13.16, -48.14) * mm});
            skLineSegment(sketch, "E442", {"start": v(13.16, -48.14) * mm, "end": v(19.18, -46.06) * mm});
            skLineSegment(sketch, "E443", {"start": v(19.18, -46.06) * mm, "end": v(24.98, -43.21) * mm});
            skLineSegment(sketch, "E444", {"start": v(24.98, -43.21) * mm, "end": v(25.31, -43.07) * mm});
            skLineSegment(sketch, "E445", {"start": v(25.31, -43.07) * mm, "end": v(25.67, -42.96) * mm});
            skLineSegment(sketch, "E446", {"start": v(25.67, -42.96) * mm, "end": v(26.04, -42.9) * mm});
            skLineSegment(sketch, "E447", {"start": v(26.04, -42.9) * mm, "end": v(26.4, -42.85) * mm});
            skLineSegment(sketch, "E448", {"start": v(26.4, -42.85) * mm, "end": v(27.23, -42.77) * mm});
            skLineSegment(sketch, "E449", {"start": v(27.23, -42.77) * mm, "end": v(28.06, -42.7) * mm});
            skLineSegment(sketch, "E450", {"start": v(28.06, -42.7) * mm, "end": v(28.89, -42.65) * mm});
            skLineSegment(sketch, "E451", {"start": v(28.89, -42.65) * mm, "end": v(29.72, -42.6) * mm});
            skLineSegment(sketch, "E452", {"start": v(29.72, -42.6) * mm, "end": v(29.72, -42.54) * mm});
            skLineSegment(sketch, "E453", {"start": v(29.72, -42.54) * mm, "end": v(29.71, -42.48) * mm});
            skLineSegment(sketch, "E454", {"start": v(29.71, -42.48) * mm, "end": v(29.71, -42.42) * mm});
            skLineSegment(sketch, "E455", {"start": v(29.71, -42.42) * mm, "end": v(29.71, -42.36) * mm});
            skLineSegment(sketch, "E456", {"start": v(29.71, -42.36) * mm, "end": v(29.08, -42.28) * mm});
            skLineSegment(sketch, "E457", {"start": v(29.08, -42.28) * mm, "end": v(28.43, -42.2) * mm});
            skLineSegment(sketch, "E458", {"start": v(28.43, -42.2) * mm, "end": v(27.74, -42.12) * mm});
            skLineSegment(sketch, "E459", {"start": v(27.74, -42.12) * mm, "end": v(27, -42.03) * mm});
            skLineSegment(sketch, "E460", {"start": v(-20.98, -56.46) * mm, "end": v(-23.56, -56.67) * mm});
            skLineSegment(sketch, "E461", {"start": v(-23.56, -56.67) * mm, "end": v(-26.1, -55.99) * mm});
            skLineSegment(sketch, "E462", {"start": v(-26.1, -55.99) * mm, "end": v(-31.84, -52.86) * mm});
            skLineSegment(sketch, "E463", {"start": v(-31.84, -52.86) * mm, "end": v(-37.26, -49.24) * mm});
            skLineSegment(sketch, "E464", {"start": v(-37.26, -49.24) * mm, "end": v(-37.68, -48.85) * mm});
            skLineSegment(sketch, "E465", {"start": v(-37.68, -48.85) * mm, "end": v(-38.07, -48.42) * mm});
            skLineSegment(sketch, "E466", {"start": v(-38.07, -48.42) * mm, "end": v(-41.54, -45.09) * mm});
            skLineSegment(sketch, "E467", {"start": v(-41.54, -45.09) * mm, "end": v(-44.98, -41.73) * mm});
            skLineSegment(sketch, "E468", {"start": v(-44.98, -41.73) * mm, "end": v(-45.37, -41.1) * mm});
            skLineSegment(sketch, "E469", {"start": v(-45.37, -41.1) * mm, "end": v(-45.73, -40.25) * mm});
            skLineSegment(sketch, "E470", {"start": v(-45.73, -40.25) * mm, "end": v(-46.98, -39.6) * mm});
            skLineSegment(sketch, "E471", {"start": v(-46.98, -39.6) * mm, "end": v(-48.35, -38.8) * mm});
            skLineSegment(sketch, "E472", {"start": v(-48.35, -38.8) * mm, "end": v(-48.8, -38.3) * mm});
            skLineSegment(sketch, "E473", {"start": v(-48.8, -38.3) * mm, "end": v(-49.2, -37.69) * mm});
            skLineSegment(sketch, "E474", {"start": v(-49.2, -37.69) * mm, "end": v(-51.07, -35.06) * mm});
            skLineSegment(sketch, "E475", {"start": v(-51.07, -35.06) * mm, "end": v(-52.95, -32.43) * mm});
            skLineSegment(sketch, "E476", {"start": v(-52.95, -32.43) * mm, "end": v(-53.27, -31.96) * mm});
            skLineSegment(sketch, "E477", {"start": v(-53.27, -31.96) * mm, "end": v(-53.53, -31.46) * mm});
            skLineSegment(sketch, "E478", {"start": v(-53.53, -31.46) * mm, "end": v(-55.3, -26.67) * mm});
            skLineSegment(sketch, "E479", {"start": v(-55.3, -26.67) * mm, "end": v(-57.06, -21.88) * mm});
            skLineSegment(sketch, "E480", {"start": v(-57.06, -21.88) * mm, "end": v(-57.2, -21.53) * mm});
            skLineSegment(sketch, "E481", {"start": v(-57.2, -21.53) * mm, "end": v(-57.4, -21.28) * mm});
            skLineSegment(sketch, "E482", {"start": v(-57.4, -21.28) * mm, "end": v(-58.18, -20.36) * mm});
            skLineSegment(sketch, "E483", {"start": v(-58.18, -20.36) * mm, "end": v(-58.45, -19.18) * mm});
            skLineSegment(sketch, "E484", {"start": v(-58.45, -19.18) * mm, "end": v(-59.04, -17.5) * mm});
            skLineSegment(sketch, "E485", {"start": v(-59.04, -17.5) * mm, "end": v(-59.67, -15.82) * mm});
            skLineSegment(sketch, "E486", {"start": v(-59.67, -15.82) * mm, "end": v(-60.07, -14.45) * mm});
            skLineSegment(sketch, "E487", {"start": v(-60.07, -14.45) * mm, "end": v(-60.36, -13.07) * mm});
            skLineSegment(sketch, "E488", {"start": v(-60.36, -13.07) * mm, "end": v(-60.98, -9.39) * mm});
            skLineSegment(sketch, "E489", {"start": v(-60.98, -9.39) * mm, "end": v(-61.44, -5.7) * mm});
            skLineSegment(sketch, "E490", {"start": v(-61.44, -5.7) * mm, "end": v(-61.62, -1.34) * mm});
            skLineSegment(sketch, "E491", {"start": v(-61.62, -1.34) * mm, "end": v(-61.58, 3.02) * mm});
            skLineSegment(sketch, "E492", {"start": v(-61.58, 3.02) * mm, "end": v(-61.2, 4.44) * mm});
            skLineSegment(sketch, "E493", {"start": v(-61.2, 4.44) * mm, "end": v(-60.6, 5.85) * mm});
            skLineSegment(sketch, "E494", {"start": v(-60.6, 5.85) * mm, "end": v(-60.48, 6.44) * mm});
            skLineSegment(sketch, "E495", {"start": v(-60.48, 6.44) * mm, "end": v(-60.53, 7.03) * mm});
            skLineSegment(sketch, "E496", {"start": v(-60.53, 7.03) * mm, "end": v(-60.82, 10.19) * mm});
            skLineSegment(sketch, "E497", {"start": v(-60.82, 10.19) * mm, "end": v(-60.3, 13.32) * mm});
            skLineSegment(sketch, "E498", {"start": v(-60.3, 13.32) * mm, "end": v(-59.8, 14.84) * mm});
            skLineSegment(sketch, "E499", {"start": v(-59.8, 14.84) * mm, "end": v(-58.65, 15.97) * mm});
            skLineSegment(sketch, "E500", {"start": v(-58.65, 15.97) * mm, "end": v(-58.47, 16.22) * mm});
            skLineSegment(sketch, "E501", {"start": v(-58.47, 16.22) * mm, "end": v(-58.44, 16.48) * mm});
            skLineSegment(sketch, "E502", {"start": v(-58.44, 16.48) * mm, "end": v(-58.76, 17.99) * mm});
            skLineSegment(sketch, "E503", {"start": v(-58.76, 17.99) * mm, "end": v(-58.6, 19.6) * mm});
            skLineSegment(sketch, "E504", {"start": v(-58.6, 19.6) * mm, "end": v(-58.24, 19.4) * mm});
            skLineSegment(sketch, "E505", {"start": v(-58.24, 19.4) * mm, "end": v(-57.87, 19.2) * mm});
            skLineSegment(sketch, "E506", {"start": v(-57.87, 19.2) * mm, "end": v(-57.7, 20.12) * mm});
            skLineSegment(sketch, "E507", {"start": v(-57.7, 20.12) * mm, "end": v(-57.53, 21.06) * mm});
            skLineSegment(sketch, "E508", {"start": v(-57.53, 21.06) * mm, "end": v(-57.2, 21.03) * mm});
            skLineSegment(sketch, "E509", {"start": v(-57.2, 21.03) * mm, "end": v(-56.83, 21) * mm});
            skLineSegment(sketch, "E510", {"start": v(-56.83, 21) * mm, "end": v(-56.9, 21.5) * mm});
            skLineSegment(sketch, "E511", {"start": v(-56.9, 21.5) * mm, "end": v(-57, 21.93) * mm});
            skLineSegment(sketch, "E512", {"start": v(-57, 21.93) * mm, "end": v(-57.06, 23.03) * mm});
            skLineSegment(sketch, "E513", {"start": v(-57.06, 23.03) * mm, "end": v(-56.52, 24.04) * mm});
            skLineSegment(sketch, "E514", {"start": v(-56.52, 24.04) * mm, "end": v(-55.87, 25.26) * mm});
            skLineSegment(sketch, "E515", {"start": v(-55.87, 25.26) * mm, "end": v(-55.43, 26.6) * mm});
            skLineSegment(sketch, "E516", {"start": v(-55.43, 26.6) * mm, "end": v(-54.66, 28.68) * mm});
            skLineSegment(sketch, "E517", {"start": v(-54.66, 28.68) * mm, "end": v(-53.1, 30.28) * mm});
            skLineSegment(sketch, "E518", {"start": v(-53.1, 30.28) * mm, "end": v(-52.06, 31.35) * mm});
            skLineSegment(sketch, "E519", {"start": v(-52.06, 31.35) * mm, "end": v(-51.45, 32.86) * mm});
            skLineSegment(sketch, "E520", {"start": v(-51.45, 32.86) * mm, "end": v(-50.44, 35.2) * mm});
            skLineSegment(sketch, "E521", {"start": v(-50.44, 35.2) * mm, "end": v(-49.12, 37.41) * mm});
            skLineSegment(sketch, "E522", {"start": v(-49.12, 37.41) * mm, "end": v(-48.2, 38.66) * mm});
            skLineSegment(sketch, "E523", {"start": v(-48.2, 38.66) * mm, "end": v(-47.14, 39.8) * mm});
            skLineSegment(sketch, "E524", {"start": v(-47.14, 39.8) * mm, "end": v(-46.1, 40.71) * mm});
            skLineSegment(sketch, "E525", {"start": v(-46.1, 40.71) * mm, "end": v(-44.98, 41.57) * mm});
            skLineSegment(sketch, "E526", {"start": v(-44.98, 41.57) * mm, "end": v(-44.75, 41.7) * mm});
            skLineSegment(sketch, "E527", {"start": v(-44.75, 41.7) * mm, "end": v(-44.53, 41.84) * mm});
            skLineSegment(sketch, "E528", {"start": v(-44.53, 41.84) * mm, "end": v(-42.97, 43.66) * mm});
            skLineSegment(sketch, "E529", {"start": v(-42.97, 43.66) * mm, "end": v(-41.35, 45.44) * mm});
            skLineSegment(sketch, "E530", {"start": v(-41.35, 45.44) * mm, "end": v(-40.33, 46.25) * mm});
            skLineSegment(sketch, "E531", {"start": v(-40.33, 46.25) * mm, "end": v(-39.22, 46.97) * mm});
            skLineSegment(sketch, "E532", {"start": v(-39.22, 46.97) * mm, "end": v(-39.12, 47.05) * mm});
            skLineSegment(sketch, "E533", {"start": v(-39.12, 47.05) * mm, "end": v(-39.03, 47.15) * mm});
            skLineSegment(sketch, "E534", {"start": v(-39.03, 47.15) * mm, "end": v(-36.04, 50.1) * mm});
            skLineSegment(sketch, "E535", {"start": v(-36.04, 50.1) * mm, "end": v(-32.55, 52.43) * mm});
            skLineSegment(sketch, "E536", {"start": v(-32.55, 52.43) * mm, "end": v(-30.44, 53.53) * mm});
            skLineSegment(sketch, "E537", {"start": v(-30.44, 53.53) * mm, "end": v(-28.1, 53.72) * mm});
            skLineSegment(sketch, "E538", {"start": v(-28.1, 53.72) * mm, "end": v(-27.78, 53.73) * mm});
            skLineSegment(sketch, "E539", {"start": v(-27.78, 53.73) * mm, "end": v(-27.47, 53.77) * mm});
            skLineSegment(sketch, "E540", {"start": v(-27.47, 53.77) * mm, "end": v(-27.4, 53.82) * mm});
            skLineSegment(sketch, "E541", {"start": v(-27.4, 53.82) * mm, "end": v(-27.31, 53.94) * mm});
            skLineSegment(sketch, "E542", {"start": v(-27.31, 53.94) * mm, "end": v(-27.74, 54.18) * mm});
            skLineSegment(sketch, "E543", {"start": v(-27.74, 54.18) * mm, "end": v(-28.32, 54.5) * mm});
            skLineSegment(sketch, "E544", {"start": v(-28.32, 54.5) * mm, "end": v(-26.7, 54.67) * mm});
            skLineSegment(sketch, "E545", {"start": v(-26.7, 54.67) * mm, "end": v(-25.26, 54.81) * mm});
            skLineSegment(sketch, "E546", {"start": v(-25.26, 54.81) * mm, "end": v(-25.22, 54.72) * mm});
            skLineSegment(sketch, "E547", {"start": v(-25.22, 54.72) * mm, "end": v(-25.18, 54.63) * mm});
            skLineSegment(sketch, "E548", {"start": v(-25.18, 54.63) * mm, "end": v(-25.6, 54.42) * mm});
            skLineSegment(sketch, "E549", {"start": v(-25.6, 54.42) * mm, "end": v(-26.03, 54.2) * mm});
            skLineSegment(sketch, "E550", {"start": v(-26.03, 54.2) * mm, "end": v(-27.58, 53.34) * mm});
            skLineSegment(sketch, "E551", {"start": v(-27.58, 53.34) * mm, "end": v(-29.14, 52.5) * mm});
            skLineSegment(sketch, "E552", {"start": v(-29.14, 52.5) * mm, "end": v(-32.13, 50.78) * mm});
            skLineSegment(sketch, "E553", {"start": v(-32.13, 50.78) * mm, "end": v(-34.96, 48.83) * mm});
            skLineSegment(sketch, "E554", {"start": v(-34.96, 48.83) * mm, "end": v(-37.75, 46.7) * mm});
            skLineSegment(sketch, "E555", {"start": v(-37.75, 46.7) * mm, "end": v(-40.43, 44.43) * mm});
            skLineSegment(sketch, "E556", {"start": v(-40.43, 44.43) * mm, "end": v(-45.2, 39.66) * mm});
            skLineSegment(sketch, "E557", {"start": v(-45.2, 39.66) * mm, "end": v(-49.34, 34.33) * mm});
            skLineSegment(sketch, "E558", {"start": v(-49.34, 34.33) * mm, "end": v(-51.58, 31.03) * mm});
            skLineSegment(sketch, "E559", {"start": v(-51.58, 31.03) * mm, "end": v(-53.76, 27.68) * mm});
            skLineSegment(sketch, "E560", {"start": v(-53.76, 27.68) * mm, "end": v(-54.86, 25.61) * mm});
            skLineSegment(sketch, "E561", {"start": v(-54.86, 25.61) * mm, "end": v(-55.9, 23.5) * mm});
            skLineSegment(sketch, "E562", {"start": v(-55.9, 23.5) * mm, "end": v(-56.26, 22.58) * mm});
            skLineSegment(sketch, "E563", {"start": v(-56.26, 22.58) * mm, "end": v(-56.19, 21.54) * mm});
            skLineSegment(sketch, "E564", {"start": v(-56.19, 21.54) * mm, "end": v(-56.32, 20.8) * mm});
            skLineSegment(sketch, "E565", {"start": v(-56.32, 20.8) * mm, "end": v(-56.7, 19.99) * mm});
            skLineSegment(sketch, "E566", {"start": v(-56.7, 19.99) * mm, "end": v(-57.16, 18.57) * mm});
            skLineSegment(sketch, "E567", {"start": v(-57.16, 18.57) * mm, "end": v(-57.64, 17.15) * mm});
            skLineSegment(sketch, "E568", {"start": v(-57.64, 17.15) * mm, "end": v(-58.1, 15.96) * mm});
            skLineSegment(sketch, "E569", {"start": v(-58.1, 15.96) * mm, "end": v(-58.55, 14.77) * mm});
            skLineSegment(sketch, "E570", {"start": v(-58.55, 14.77) * mm, "end": v(-58.98, 13.52) * mm});
            skLineSegment(sketch, "E571", {"start": v(-58.98, 13.52) * mm, "end": v(-59.28, 12.25) * mm});
            skLineSegment(sketch, "E572", {"start": v(-59.28, 12.25) * mm, "end": v(-59.53, 9.57) * mm});
            skLineSegment(sketch, "E573", {"start": v(-59.53, 9.57) * mm, "end": v(-59.76, 6.87) * mm});
            skLineSegment(sketch, "E574", {"start": v(-59.76, 6.87) * mm, "end": v(-59.35, -9.72) * mm});
            skLineSegment(sketch, "E575", {"start": v(-59.35, -9.72) * mm, "end": v(-54.4, -25.57) * mm});
            skLineSegment(sketch, "E576", {"start": v(-54.4, -25.57) * mm, "end": v(-49.1, -34.66) * mm});
            skLineSegment(sketch, "E577", {"start": v(-49.1, -34.66) * mm, "end": v(-42.3, -42.67) * mm});
            skLineSegment(sketch, "E578", {"start": v(-42.3, -42.67) * mm, "end": v(-32.9, -50.28) * mm});
            skLineSegment(sketch, "E579", {"start": v(-32.9, -50.28) * mm, "end": v(-22.13, -55.83) * mm});
            skLineSegment(sketch, "E580", {"start": v(-22.13, -55.83) * mm, "end": v(-21.6, -56.04) * mm});
            skLineSegment(sketch, "E581", {"start": v(-21.6, -56.04) * mm, "end": v(-21.07, -56.27) * mm});
            skLineSegment(sketch, "E582", {"start": v(-21.07, -56.27) * mm, "end": v(-21.03, -56.33) * mm});
            skLineSegment(sketch, "E583", {"start": v(-21.03, -56.33) * mm, "end": v(-20.98, -56.46) * mm});
            skLineSegment(sketch, "E584", {"start": v(-21.32, -57.87) * mm, "end": v(-20.86, -57.7) * mm});
            skLineSegment(sketch, "E585", {"start": v(-20.86, -57.7) * mm, "end": v(-20.56, -57.63) * mm});
            skLineSegment(sketch, "E586", {"start": v(-20.56, -57.63) * mm, "end": v(-18.62, -57.61) * mm});
            skLineSegment(sketch, "E587", {"start": v(-18.62, -57.61) * mm, "end": v(-16.7, -57.96) * mm});
            skLineSegment(sketch, "E588", {"start": v(-16.7, -57.96) * mm, "end": v(-14.18, -58.48) * mm});
            skLineSegment(sketch, "E589", {"start": v(-14.18, -58.48) * mm, "end": v(-11.66, -58.94) * mm});
            skLineSegment(sketch, "E590", {"start": v(-11.66, -58.94) * mm, "end": v(-2.5, -60.02) * mm});
            skLineSegment(sketch, "E591", {"start": v(-2.5, -60.02) * mm, "end": v(6.73, -59.68) * mm});
            skLineSegment(sketch, "E592", {"start": v(6.73, -59.68) * mm, "end": v(21.96, -55.94) * mm});
            skLineSegment(sketch, "E593", {"start": v(21.96, -55.94) * mm, "end": v(35.65, -48.33) * mm});
            skLineSegment(sketch, "E594", {"start": v(35.65, -48.33) * mm, "end": v(43.69, -41.22) * mm});
            skLineSegment(sketch, "E595", {"start": v(43.69, -41.22) * mm, "end": v(50.32, -32.77) * mm});
            skLineSegment(sketch, "E596", {"start": v(50.32, -32.77) * mm, "end": v(51.32, -31.62) * mm});
            skLineSegment(sketch, "E597", {"start": v(51.32, -31.62) * mm, "end": v(52.84, -31.35) * mm});
            skLineSegment(sketch, "E598", {"start": v(52.84, -31.35) * mm, "end": v(52.42, -32.14) * mm});
            skLineSegment(sketch, "E599", {"start": v(52.42, -32.14) * mm, "end": v(51.94, -32.94) * mm});
            skLineSegment(sketch, "E600", {"start": v(51.94, -32.94) * mm, "end": v(50.09, -35.6) * mm});
            skLineSegment(sketch, "E601", {"start": v(50.09, -35.6) * mm, "end": v(48.17, -38.2) * mm});
            skLineSegment(sketch, "E602", {"start": v(48.17, -38.2) * mm, "end": v(47.5, -38.63) * mm});
            skLineSegment(sketch, "E603", {"start": v(47.5, -38.63) * mm, "end": v(46.61, -38.97) * mm});
            skLineSegment(sketch, "E604", {"start": v(46.61, -38.97) * mm, "end": v(46.93, -39.27) * mm});
            skLineSegment(sketch, "E605", {"start": v(46.93, -39.27) * mm, "end": v(47.36, -39.67) * mm});
            skLineSegment(sketch, "E606", {"start": v(47.36, -39.67) * mm, "end": v(45.12, -42.05) * mm});
            skLineSegment(sketch, "E607", {"start": v(45.12, -42.05) * mm, "end": v(42.84, -44.39) * mm});
            skLineSegment(sketch, "E608", {"start": v(42.84, -44.39) * mm, "end": v(29.34, -54.28) * mm});
            skLineSegment(sketch, "E609", {"start": v(29.34, -54.28) * mm, "end": v(13.67, -60.16) * mm});
            skLineSegment(sketch, "E610", {"start": v(13.67, -60.16) * mm, "end": v(10.22, -60.8) * mm});
            skLineSegment(sketch, "E611", {"start": v(10.22, -60.8) * mm, "end": v(6.76, -61.34) * mm});
            skLineSegment(sketch, "E612", {"start": v(6.76, -61.34) * mm, "end": v(5.44, -61.2) * mm});
            skLineSegment(sketch, "E613", {"start": v(5.44, -61.2) * mm, "end": v(4, -61.46) * mm});
            skLineSegment(sketch, "E614", {"start": v(4, -61.46) * mm, "end": v(2.6, -61.76) * mm});
            skLineSegment(sketch, "E615", {"start": v(2.6, -61.76) * mm, "end": v(0.96, -61.7) * mm});
            skLineSegment(sketch, "E616", {"start": v(0.96, -61.7) * mm, "end": v(-0.55, -61.72) * mm});
            skLineSegment(sketch, "E617", {"start": v(-0.55, -61.72) * mm, "end": v(-2.06, -61.7) * mm});
            skLineSegment(sketch, "E618", {"start": v(-2.06, -61.7) * mm, "end": v(-3.57, -61.61) * mm});
            skLineSegment(sketch, "E619", {"start": v(-3.57, -61.61) * mm, "end": v(-5.08, -61.5) * mm});
            skLineSegment(sketch, "E620", {"start": v(-5.08, -61.5) * mm, "end": v(-5.36, -61.47) * mm});
            skLineSegment(sketch, "E621", {"start": v(-5.36, -61.47) * mm, "end": v(-5.56, -61.37) * mm});
            skLineSegment(sketch, "E622", {"start": v(-5.56, -61.37) * mm, "end": v(-6.27, -60.82) * mm});
            skLineSegment(sketch, "E623", {"start": v(-6.27, -60.82) * mm, "end": v(-7.15, -60.9) * mm});
            skLineSegment(sketch, "E624", {"start": v(-7.15, -60.9) * mm, "end": v(-8.52, -60.94) * mm});
            skLineSegment(sketch, "E625", {"start": v(-8.52, -60.94) * mm, "end": v(-9.88, -60.87) * mm});
            skLineSegment(sketch, "E626", {"start": v(-9.88, -60.87) * mm, "end": v(-15.23, -59.81) * mm});
            skLineSegment(sketch, "E627", {"start": v(-15.23, -59.81) * mm, "end": v(-20.45, -58.27) * mm});
            skLineSegment(sketch, "E628", {"start": v(-20.45, -58.27) * mm, "end": v(-20.82, -58.11) * mm});
            skLineSegment(sketch, "E629", {"start": v(-20.82, -58.11) * mm, "end": v(-21.32, -57.87) * mm});
            skLineSegment(sketch, "E630", {"start": v(51.84, -30.38) * mm, "end": v(58.24, -14.62) * mm});
            skLineSegment(sketch, "E631", {"start": v(58.24, -14.62) * mm, "end": v(60.05, 2.19) * mm});
            skLineSegment(sketch, "E632", {"start": v(60.05, 2.19) * mm, "end": v(56.7, 19.8) * mm});
            skLineSegment(sketch, "E633", {"start": v(56.7, 19.8) * mm, "end": v(50.05, 33.96) * mm});
            skLineSegment(sketch, "E634", {"start": v(50.05, 33.96) * mm, "end": v(51.46, 33.79) * mm});
            skLineSegment(sketch, "E635", {"start": v(51.46, 33.79) * mm, "end": v(52.47, 32.82) * mm});
            skLineSegment(sketch, "E636", {"start": v(52.47, 32.82) * mm, "end": v(53.3, 31.21) * mm});
            skLineSegment(sketch, "E637", {"start": v(53.3, 31.21) * mm, "end": v(54.24, 29.65) * mm});
            skLineSegment(sketch, "E638", {"start": v(54.24, 29.65) * mm, "end": v(54.58, 28.71) * mm});
            skLineSegment(sketch, "E639", {"start": v(54.58, 28.71) * mm, "end": v(54.05, 27.74) * mm});
            skLineSegment(sketch, "E640", {"start": v(54.05, 27.74) * mm, "end": v(54.65, 27.74) * mm});
            skLineSegment(sketch, "E641", {"start": v(54.65, 27.74) * mm, "end": v(55.1, 27.74) * mm});
            skLineSegment(sketch, "E642", {"start": v(55.1, 27.74) * mm, "end": v(57.16, 23.62) * mm});
            skLineSegment(sketch, "E643", {"start": v(57.16, 23.62) * mm, "end": v(58.47, 19.22) * mm});
            skLineSegment(sketch, "E644", {"start": v(58.47, 19.22) * mm, "end": v(58.7, 18.2) * mm});
            skLineSegment(sketch, "E645", {"start": v(58.7, 18.2) * mm, "end": v(59.1, 17.2) * mm});
            skLineSegment(sketch, "E646", {"start": v(59.1, 17.2) * mm, "end": v(60.78, 11.16) * mm});
            skLineSegment(sketch, "E647", {"start": v(60.78, 11.16) * mm, "end": v(61.57, 4.96) * mm});
            skLineSegment(sketch, "E648", {"start": v(61.57, 4.96) * mm, "end": v(61.62, -4.53) * mm});
            skLineSegment(sketch, "E649", {"start": v(61.62, -4.53) * mm, "end": v(60.17, -13.92) * mm});
            skLineSegment(sketch, "E650", {"start": v(60.17, -13.92) * mm, "end": v(57.96, -21.27) * mm});
            skLineSegment(sketch, "E651", {"start": v(57.96, -21.27) * mm, "end": v(54.88, -28.3) * mm});
            skLineSegment(sketch, "E652", {"start": v(54.88, -28.3) * mm, "end": v(53.74, -29.73) * mm});
            skLineSegment(sketch, "E653", {"start": v(53.74, -29.73) * mm, "end": v(51.84, -30.38) * mm});
            skLineSegment(sketch, "E654", {"start": v(28.86, 53.23) * mm, "end": v(26.06, 54.53) * mm});
            skLineSegment(sketch, "E655", {"start": v(26.06, 54.53) * mm, "end": v(23.27, 55.78) * mm});
            skLineSegment(sketch, "E656", {"start": v(23.27, 55.78) * mm, "end": v(11.47, 59.33) * mm});
            skLineSegment(sketch, "E657", {"start": v(11.47, 59.33) * mm, "end": v(-0.8, 60.28) * mm});
            skLineSegment(sketch, "E658", {"start": v(-0.8, 60.28) * mm, "end": v(-11.77, 59.02) * mm});
            skLineSegment(sketch, "E659", {"start": v(-11.77, 59.02) * mm, "end": v(-22.35, 55.87) * mm});
            skLineSegment(sketch, "E660", {"start": v(-22.35, 55.87) * mm, "end": v(-24.38, 55.5) * mm});
            skLineSegment(sketch, "E661", {"start": v(-24.38, 55.5) * mm, "end": v(-26.52, 55.52) * mm});
            skLineSegment(sketch, "E662", {"start": v(-26.52, 55.52) * mm, "end": v(-18.93, 58.78) * mm});
            skLineSegment(sketch, "E663", {"start": v(-18.93, 58.78) * mm, "end": v(-10.95, 60.86) * mm});
            skLineSegment(sketch, "E664", {"start": v(-10.95, 60.86) * mm, "end": v(-2.75, 61.76) * mm});
            skLineSegment(sketch, "E665", {"start": v(-2.75, 61.76) * mm, "end": v(5.5, 61.62) * mm});
            skLineSegment(sketch, "E666", {"start": v(5.5, 61.62) * mm, "end": v(4.9, 61.48) * mm});
            skLineSegment(sketch, "E667", {"start": v(4.9, 61.48) * mm, "end": v(4.31, 61.35) * mm});
            skLineSegment(sketch, "E668", {"start": v(4.31, 61.35) * mm, "end": v(4.3, 61.26) * mm});
            skLineSegment(sketch, "E669", {"start": v(4.3, 61.26) * mm, "end": v(4.3, 61.17) * mm});
            skLineSegment(sketch, "E670", {"start": v(4.3, 61.17) * mm, "end": v(4.78, 61.12) * mm});
            skLineSegment(sketch, "E671", {"start": v(4.78, 61.12) * mm, "end": v(5.26, 61.08) * mm});
            skLineSegment(sketch, "E672", {"start": v(5.26, 61.08) * mm, "end": v(6.63, 60.95) * mm});
            skLineSegment(sketch, "E673", {"start": v(6.63, 60.95) * mm, "end": v(8, 60.84) * mm});
            skLineSegment(sketch, "E674", {"start": v(8, 60.84) * mm, "end": v(9.19, 60.78) * mm});
            skLineSegment(sketch, "E675", {"start": v(9.19, 60.78) * mm, "end": v(10.36, 60.84) * mm});
            skLineSegment(sketch, "E676", {"start": v(10.36, 60.84) * mm, "end": v(12.57, 60.8) * mm});
            skLineSegment(sketch, "E677", {"start": v(12.57, 60.8) * mm, "end": v(14.55, 59.77) * mm});
            skLineSegment(sketch, "E678", {"start": v(14.55, 59.77) * mm, "end": v(15.73, 59.03) * mm});
            skLineSegment(sketch, "E679", {"start": v(15.73, 59.03) * mm, "end": v(17.23, 58.97) * mm});
            skLineSegment(sketch, "E680", {"start": v(17.23, 58.97) * mm, "end": v(18.3, 58.96) * mm});
            skLineSegment(sketch, "E681", {"start": v(18.3, 58.96) * mm, "end": v(19.4, 58.64) * mm});
            skLineSegment(sketch, "E682", {"start": v(19.4, 58.64) * mm, "end": v(23.76, 57.25) * mm});
            skLineSegment(sketch, "E683", {"start": v(23.76, 57.25) * mm, "end": v(27.94, 55.3) * mm});
            skLineSegment(sketch, "E684", {"start": v(27.94, 55.3) * mm, "end": v(28.75, 54.4) * mm});
            skLineSegment(sketch, "E685", {"start": v(28.75, 54.4) * mm, "end": v(28.86, 53.23) * mm});
            skLineSegment(sketch, "E686", {"start": v(49.06, 37.16) * mm, "end": v(48.82, 37.54) * mm});
            skLineSegment(sketch, "E687", {"start": v(48.82, 37.54) * mm, "end": v(48.57, 37.92) * mm});
            skLineSegment(sketch, "E688", {"start": v(48.57, 37.92) * mm, "end": v(46.83, 37.96) * mm});
            skLineSegment(sketch, "E689", {"start": v(46.83, 37.96) * mm, "end": v(45.78, 39.45) * mm});
            skLineSegment(sketch, "E690", {"start": v(45.78, 39.45) * mm, "end": v(45.63, 39.76) * mm});
            skLineSegment(sketch, "E691", {"start": v(45.63, 39.76) * mm, "end": v(45.41, 40.03) * mm});
            skLineSegment(sketch, "E692", {"start": v(45.41, 40.03) * mm, "end": v(39.86, 45.33) * mm});
            skLineSegment(sketch, "E693", {"start": v(39.86, 45.33) * mm, "end": v(33.82, 50.06) * mm});
            skLineSegment(sketch, "E694", {"start": v(33.82, 50.06) * mm, "end": v(32.25, 51.07) * mm});
            skLineSegment(sketch, "E695", {"start": v(32.25, 51.07) * mm, "end": v(30.67, 52.05) * mm});
            skLineSegment(sketch, "E696", {"start": v(30.67, 52.05) * mm, "end": v(30.26, 52.39) * mm});
            skLineSegment(sketch, "E697", {"start": v(30.26, 52.39) * mm, "end": v(30.16, 52.94) * mm});
            skLineSegment(sketch, "E698", {"start": v(30.16, 52.94) * mm, "end": v(30.04, 53.63) * mm});
            skLineSegment(sketch, "E699", {"start": v(30.04, 53.63) * mm, "end": v(29.77, 54.36) * mm});
            skLineSegment(sketch, "E700", {"start": v(29.77, 54.36) * mm, "end": v(30.02, 54.27) * mm});
            skLineSegment(sketch, "E701", {"start": v(30.02, 54.27) * mm, "end": v(30.3, 54.14) * mm});
            skLineSegment(sketch, "E702", {"start": v(30.3, 54.14) * mm, "end": v(38.87, 48.3) * mm});
            skLineSegment(sketch, "E703", {"start": v(38.87, 48.3) * mm, "end": v(46.33, 41.08) * mm});
            skLineSegment(sketch, "E704", {"start": v(46.33, 41.08) * mm, "end": v(46.59, 40.77) * mm});
            skLineSegment(sketch, "E705", {"start": v(46.59, 40.77) * mm, "end": v(46.78, 40.43) * mm});
            skLineSegment(sketch, "E706", {"start": v(46.78, 40.43) * mm, "end": v(47.36, 39.38) * mm});
            skLineSegment(sketch, "E707", {"start": v(47.36, 39.38) * mm, "end": v(48.36, 38.66) * mm});
            skLineSegment(sketch, "E708", {"start": v(48.36, 38.66) * mm, "end": v(48.92, 38.13) * mm});
            skLineSegment(sketch, "E709", {"start": v(48.92, 38.13) * mm, "end": v(49.4, 37.44) * mm});
            skLineSegment(sketch, "E710", {"start": v(49.4, 37.44) * mm, "end": v(49.23, 37.3) * mm});
            skLineSegment(sketch, "E711", {"start": v(49.23, 37.3) * mm, "end": v(49.06, 37.16) * mm});
            skLineSegment(sketch, "E712", {"start": v(48.48, 36.12) * mm, "end": v(49.27, 36.12) * mm});
            skLineSegment(sketch, "E713", {"start": v(49.27, 36.12) * mm, "end": v(50.05, 36.12) * mm});
            skLineSegment(sketch, "E714", {"start": v(50.05, 36.12) * mm, "end": v(50.23, 35.46) * mm});
            skLineSegment(sketch, "E715", {"start": v(50.23, 35.46) * mm, "end": v(50.41, 34.73) * mm});
            skLineSegment(sketch, "E716", {"start": v(50.41, 34.73) * mm, "end": v(49.36, 35.25) * mm});
            skLineSegment(sketch, "E717", {"start": v(49.36, 35.25) * mm, "end": v(48.36, 35.75) * mm});
            skLineSegment(sketch, "E718", {"start": v(48.36, 35.75) * mm, "end": v(48.42, 35.93) * mm});
            skLineSegment(sketch, "E719", {"start": v(48.42, 35.93) * mm, "end": v(48.48, 36.12) * mm});
            skLineSegment(sketch, "E720", {"start": v(5.9, 1.68) * mm, "end": v(6.46, 1.12) * mm});
            skLineSegment(sketch, "E721", {"start": v(6.46, 1.12) * mm, "end": v(7.02, 0.57) * mm});
            skLineSegment(sketch, "E722", {"start": v(7.02, 0.57) * mm, "end": v(7.58, 0.02) * mm});
            skLineSegment(sketch, "E723", {"start": v(7.58, 0.02) * mm, "end": v(8.13, -0.52) * mm});
            skLineSegment(sketch, "E724", {"start": v(8.13, -0.52) * mm, "end": v(8.68, -1.06) * mm});
            skLineSegment(sketch, "E725", {"start": v(8.68, -1.06) * mm, "end": v(9.22, -1.6) * mm});
            skLineSegment(sketch, "E726", {"start": v(9.22, -1.6) * mm, "end": v(9.77, -2.13) * mm});
            skLineSegment(sketch, "E727", {"start": v(9.77, -2.13) * mm, "end": v(10.32, -2.66) * mm});
            skLineSegment(sketch, "E728", {"start": v(10.32, -2.66) * mm, "end": v(10.49, -2.83) * mm});
            skLineSegment(sketch, "E729", {"start": v(10.49, -2.83) * mm, "end": v(10.62, -3) * mm});
            skLineSegment(sketch, "E730", {"start": v(10.62, -3) * mm, "end": v(10.73, -3.18) * mm});
            skLineSegment(sketch, "E731", {"start": v(10.73, -3.18) * mm, "end": v(10.82, -3.37) * mm});
            skLineSegment(sketch, "E732", {"start": v(10.82, -3.37) * mm, "end": v(10.88, -3.56) * mm});
            skLineSegment(sketch, "E733", {"start": v(10.88, -3.56) * mm, "end": v(10.93, -3.77) * mm});
            skLineSegment(sketch, "E734", {"start": v(10.93, -3.77) * mm, "end": v(10.95, -3.99) * mm});
            skLineSegment(sketch, "E735", {"start": v(10.95, -3.99) * mm, "end": v(10.96, -4.22) * mm});
            skLineSegment(sketch, "E736", {"start": v(10.96, -4.22) * mm, "end": v(10.96, -8.45) * mm});
            skLineSegment(sketch, "E737", {"start": v(10.96, -8.45) * mm, "end": v(10.95, -12.69) * mm});
            skLineSegment(sketch, "E738", {"start": v(10.95, -12.69) * mm, "end": v(10.95, -16.92) * mm});
            skLineSegment(sketch, "E739", {"start": v(10.95, -16.92) * mm, "end": v(10.95, -21.16) * mm});
            skLineSegment(sketch, "E740", {"start": v(10.95, -21.16) * mm, "end": v(10.95, -25.4) * mm});
            skLineSegment(sketch, "E741", {"start": v(10.95, -25.4) * mm, "end": v(10.95, -29.63) * mm});
            skLineSegment(sketch, "E742", {"start": v(10.95, -29.63) * mm, "end": v(10.96, -33.86) * mm});
            skLineSegment(sketch, "E743", {"start": v(10.96, -33.86) * mm, "end": v(10.97, -38.1) * mm});
            skLineSegment(sketch, "E744", {"start": v(10.97, -38.1) * mm, "end": v(10.96, -38.4) * mm});
            skLineSegment(sketch, "E745", {"start": v(10.96, -38.4) * mm, "end": v(10.92, -38.65) * mm});
            skLineSegment(sketch, "E746", {"start": v(10.92, -38.65) * mm, "end": v(10.84, -38.85) * mm});
            skLineSegment(sketch, "E747", {"start": v(10.84, -38.85) * mm, "end": v(10.73, -39.02) * mm});
            skLineSegment(sketch, "E748", {"start": v(10.73, -39.02) * mm, "end": v(10.59, -39.16) * mm});
            skLineSegment(sketch, "E749", {"start": v(10.59, -39.16) * mm, "end": v(10.4, -39.27) * mm});
            skLineSegment(sketch, "E750", {"start": v(10.4, -39.27) * mm, "end": v(10.17, -39.36) * mm});
            skLineSegment(sketch, "E751", {"start": v(10.17, -39.36) * mm, "end": v(9.9, -39.44) * mm});
            skLineSegment(sketch, "E752", {"start": v(9.9, -39.44) * mm, "end": v(7.57, -39.92) * mm});
            skLineSegment(sketch, "E753", {"start": v(7.57, -39.92) * mm, "end": v(5.24, -40.27) * mm});
            skLineSegment(sketch, "E754", {"start": v(5.24, -40.27) * mm, "end": v(2.9, -40.5) * mm});
            skLineSegment(sketch, "E755", {"start": v(2.9, -40.5) * mm, "end": v(0.57, -40.58) * mm});
            skLineSegment(sketch, "E756", {"start": v(0.57, -40.58) * mm, "end": v(-1.76, -40.53) * mm});
            skLineSegment(sketch, "E757", {"start": v(-1.76, -40.53) * mm, "end": v(-4.1, -40.35) * mm});
            skLineSegment(sketch, "E758", {"start": v(-4.1, -40.35) * mm, "end": v(-6.43, -40.03) * mm});
            skLineSegment(sketch, "E759", {"start": v(-6.43, -40.03) * mm, "end": v(-8.77, -39.58) * mm});
            skLineSegment(sketch, "E760", {"start": v(-8.77, -39.58) * mm, "end": v(-9.52, -39.4) * mm});
            skLineSegment(sketch, "E761", {"start": v(-9.52, -39.4) * mm, "end": v(-10.08, -39.25) * mm});
            skLineSegment(sketch, "E762", {"start": v(-10.08, -39.25) * mm, "end": v(-10.49, -39.08) * mm});
            skLineSegment(sketch, "E763", {"start": v(-10.49, -39.08) * mm, "end": v(-10.76, -38.87) * mm});
            skLineSegment(sketch, "E764", {"start": v(-10.76, -38.87) * mm, "end": v(-10.93, -38.56) * mm});
            skLineSegment(sketch, "E765", {"start": v(-10.93, -38.56) * mm, "end": v(-11.01, -38.14) * mm});
            skLineSegment(sketch, "E766", {"start": v(-11.01, -38.14) * mm, "end": v(-11.04, -37.57) * mm});
            skLineSegment(sketch, "E767", {"start": v(-11.04, -37.57) * mm, "end": v(-11.05, -36.81) * mm});
            skLineSegment(sketch, "E768", {"start": v(-11.05, -36.81) * mm, "end": v(-11.05, -27.19) * mm});
            skLineSegment(sketch, "E769", {"start": v(-11.05, -27.19) * mm, "end": v(-11.05, -17.56) * mm});
            skLineSegment(sketch, "E770", {"start": v(-11.05, -17.56) * mm, "end": v(-11.05, -7.94) * mm});
            skLineSegment(sketch, "E771", {"start": v(-11.05, -7.94) * mm, "end": v(-11.05, 1.69) * mm});
            skLineSegment(sketch, "E772", {"start": v(-11.05, 1.69) * mm, "end": v(-11.05, 11.31) * mm});
            skLineSegment(sketch, "E773", {"start": v(-11.05, 11.31) * mm, "end": v(-11.06, 20.94) * mm});
            skLineSegment(sketch, "E774", {"start": v(-11.06, 20.94) * mm, "end": v(-11.06, 30.57) * mm});
            skLineSegment(sketch, "E775", {"start": v(-11.06, 30.57) * mm, "end": v(-11.07, 40.2) * mm});
            skLineSegment(sketch, "E776", {"start": v(-11.07, 40.2) * mm, "end": v(-11.06, 40.51) * mm});
            skLineSegment(sketch, "E777", {"start": v(-11.06, 40.51) * mm, "end": v(-11.02, 40.78) * mm});
            skLineSegment(sketch, "E778", {"start": v(-11.02, 40.78) * mm, "end": v(-10.94, 41) * mm});
            skLineSegment(sketch, "E779", {"start": v(-10.94, 41) * mm, "end": v(-10.82, 41.19) * mm});
            skLineSegment(sketch, "E780", {"start": v(-10.82, 41.19) * mm, "end": v(-10.66, 41.34) * mm});
            skLineSegment(sketch, "E781", {"start": v(-10.66, 41.34) * mm, "end": v(-10.46, 41.46) * mm});
            skLineSegment(sketch, "E782", {"start": v(-10.46, 41.46) * mm, "end": v(-10.2, 41.56) * mm});
            skLineSegment(sketch, "E783", {"start": v(-10.2, 41.56) * mm, "end": v(-9.9, 41.64) * mm});
            skLineSegment(sketch, "E784", {"start": v(-9.9, 41.64) * mm, "end": v(-7.4, 42.14) * mm});
            skLineSegment(sketch, "E785", {"start": v(-7.4, 42.14) * mm, "end": v(-4.88, 42.5) * mm});
            skLineSegment(sketch, "E786", {"start": v(-4.88, 42.5) * mm, "end": v(-2.37, 42.7) * mm});
            skLineSegment(sketch, "E787", {"start": v(-2.37, 42.7) * mm, "end": v(0.14, 42.76) * mm});
            skLineSegment(sketch, "E788", {"start": v(0.14, 42.76) * mm, "end": v(2.65, 42.68) * mm});
            skLineSegment(sketch, "E789", {"start": v(2.65, 42.68) * mm, "end": v(5.16, 42.45) * mm});
            skLineSegment(sketch, "E790", {"start": v(5.16, 42.45) * mm, "end": v(7.67, 42.07) * mm});
            skLineSegment(sketch, "E791", {"start": v(7.67, 42.07) * mm, "end": v(10.17, 41.56) * mm});
            skLineSegment(sketch, "E792", {"start": v(10.17, 41.56) * mm, "end": v(10.38, 41.5) * mm});
            skLineSegment(sketch, "E793", {"start": v(10.38, 41.5) * mm, "end": v(10.55, 41.43) * mm});
            skLineSegment(sketch, "E794", {"start": v(10.55, 41.43) * mm, "end": v(10.69, 41.34) * mm});
            skLineSegment(sketch, "E795", {"start": v(10.69, 41.34) * mm, "end": v(10.8, 41.23) * mm});
            skLineSegment(sketch, "E796", {"start": v(10.8, 41.23) * mm, "end": v(10.87, 41.1) * mm});
            skLineSegment(sketch, "E797", {"start": v(10.87, 41.1) * mm, "end": v(10.93, 40.95) * mm});
            skLineSegment(sketch, "E798", {"start": v(10.93, 40.95) * mm, "end": v(10.95, 40.77) * mm});
            skLineSegment(sketch, "E799", {"start": v(10.95, 40.77) * mm, "end": v(10.96, 40.55) * mm});
            skLineSegment(sketch, "E800", {"start": v(10.96, 40.55) * mm, "end": v(10.96, 36.46) * mm});
            skLineSegment(sketch, "E801", {"start": v(10.96, 36.46) * mm, "end": v(10.95, 32.37) * mm});
            skLineSegment(sketch, "E802", {"start": v(10.95, 32.37) * mm, "end": v(10.95, 28.28) * mm});
            skLineSegment(sketch, "E803", {"start": v(10.95, 28.28) * mm, "end": v(10.95, 24.19) * mm});
            skLineSegment(sketch, "E804", {"start": v(10.95, 24.19) * mm, "end": v(10.94, 20.1) * mm});
            skLineSegment(sketch, "E805", {"start": v(10.94, 20.1) * mm, "end": v(10.94, 16) * mm});
            skLineSegment(sketch, "E806", {"start": v(10.94, 16) * mm, "end": v(10.94, 11.92) * mm});
            skLineSegment(sketch, "E807", {"start": v(10.94, 11.92) * mm, "end": v(10.93, 7.83) * mm});
            skLineSegment(sketch, "E808", {"start": v(10.93, 7.83) * mm, "end": v(10.92, 7.67) * mm});
            skLineSegment(sketch, "E809", {"start": v(10.92, 7.67) * mm, "end": v(10.89, 7.5) * mm});
            skLineSegment(sketch, "E810", {"start": v(10.89, 7.5) * mm, "end": v(10.84, 7.34) * mm});
            skLineSegment(sketch, "E811", {"start": v(10.84, 7.34) * mm, "end": v(10.78, 7.17) * mm});
            skLineSegment(sketch, "E812", {"start": v(10.78, 7.17) * mm, "end": v(10.71, 7.01) * mm});
            skLineSegment(sketch, "E813", {"start": v(10.71, 7.01) * mm, "end": v(10.63, 6.86) * mm});
            skLineSegment(sketch, "E814", {"start": v(10.63, 6.86) * mm, "end": v(10.53, 6.72) * mm});
            skLineSegment(sketch, "E815", {"start": v(10.53, 6.72) * mm, "end": v(10.43, 6.6) * mm});
            skLineSegment(sketch, "E816", {"start": v(10.43, 6.6) * mm, "end": v(10, 6.1) * mm});
            skLineSegment(sketch, "E817", {"start": v(10, 6.1) * mm, "end": v(9.55, 5.62) * mm});
            skLineSegment(sketch, "E818", {"start": v(9.55, 5.62) * mm, "end": v(9.1, 5.14) * mm});
            skLineSegment(sketch, "E819", {"start": v(9.1, 5.14) * mm, "end": v(8.66, 4.66) * mm});
            skLineSegment(sketch, "E820", {"start": v(8.66, 4.66) * mm, "end": v(8.21, 4.18) * mm});
            skLineSegment(sketch, "E821", {"start": v(8.21, 4.18) * mm, "end": v(7.76, 3.7) * mm});
            skLineSegment(sketch, "E822", {"start": v(7.76, 3.7) * mm, "end": v(7.31, 3.23) * mm});
            skLineSegment(sketch, "E823", {"start": v(7.31, 3.23) * mm, "end": v(6.86, 2.75) * mm});
            skLineSegment(sketch, "E824", {"start": v(6.86, 2.75) * mm, "end": v(6.75, 2.63) * mm});
            skLineSegment(sketch, "E825", {"start": v(6.75, 2.63) * mm, "end": v(6.64, 2.5) * mm});
            skLineSegment(sketch, "E826", {"start": v(6.64, 2.5) * mm, "end": v(6.53, 2.38) * mm});
            skLineSegment(sketch, "E827", {"start": v(6.53, 2.38) * mm, "end": v(6.41, 2.25) * mm});
            skLineSegment(sketch, "E828", {"start": v(6.41, 2.25) * mm, "end": v(6.3, 2.12) * mm});
            skLineSegment(sketch, "E829", {"start": v(6.3, 2.12) * mm, "end": v(6.17, 1.98) * mm});
            skLineSegment(sketch, "E830", {"start": v(6.17, 1.98) * mm, "end": v(6.04, 1.83) * mm});
            skLineSegment(sketch, "E831", {"start": v(6.04, 1.83) * mm, "end": v(5.9, 1.68) * mm});
            skLineSegment(sketch, "E832", {"start": v(-3.24, -2.43) * mm, "end": v(-3.24, -6.27) * mm});
            skLineSegment(sketch, "E833", {"start": v(-3.24, -6.27) * mm, "end": v(-3.24, -10.1) * mm});
            skLineSegment(sketch, "E834", {"start": v(-3.24, -10.1) * mm, "end": v(-3.24, -13.9) * mm});
            skLineSegment(sketch, "E835", {"start": v(-3.24, -13.9) * mm, "end": v(-3.24, -17.72) * mm});
            skLineSegment(sketch, "E836", {"start": v(-3.24, -17.72) * mm, "end": v(-3.24, -21.52) * mm});
            skLineSegment(sketch, "E837", {"start": v(-3.24, -21.52) * mm, "end": v(-3.24, -25.32) * mm});
            skLineSegment(sketch, "E838", {"start": v(-3.24, -25.32) * mm, "end": v(-3.24, -29.12) * mm});
            skLineSegment(sketch, "E839", {"start": v(-3.24, -29.12) * mm, "end": v(-3.24, -32.92) * mm});
            skLineSegment(sketch, "E840", {"start": v(-3.24, -32.92) * mm, "end": v(-3.06, -32.94) * mm});
            skLineSegment(sketch, "E841", {"start": v(-3.06, -32.94) * mm, "end": v(-2.88, -32.96) * mm});
            skLineSegment(sketch, "E842", {"start": v(-2.88, -32.96) * mm, "end": v(-2.71, -32.98) * mm});
            skLineSegment(sketch, "E843", {"start": v(-2.71, -32.98) * mm, "end": v(-2.54, -33) * mm});
            skLineSegment(sketch, "E844", {"start": v(-2.54, -33) * mm, "end": v(-2.38, -33.02) * mm});
            skLineSegment(sketch, "E845", {"start": v(-2.38, -33.02) * mm, "end": v(-2.21, -33.04) * mm});
            skLineSegment(sketch, "E846", {"start": v(-2.21, -33.04) * mm, "end": v(-2.05, -33.05) * mm});
            skLineSegment(sketch, "E847", {"start": v(-2.05, -33.05) * mm, "end": v(-1.88, -33.05) * mm});
            skLineSegment(sketch, "E848", {"start": v(-1.88, -33.05) * mm, "end": v(-1.4, -33.04) * mm});
            skLineSegment(sketch, "E849", {"start": v(-1.4, -33.04) * mm, "end": v(-0.9, -33.02) * mm});
            skLineSegment(sketch, "E850", {"start": v(-0.9, -33.02) * mm, "end": v(-0.42, -33) * mm});
            skLineSegment(sketch, "E851", {"start": v(-0.42, -33) * mm, "end": v(0.07, -32.97) * mm});
            skLineSegment(sketch, "E852", {"start": v(0.07, -32.97) * mm, "end": v(0.55, -32.95) * mm});
            skLineSegment(sketch, "E853", {"start": v(0.55, -32.95) * mm, "end": v(1.04, -32.94) * mm});
            skLineSegment(sketch, "E854", {"start": v(1.04, -32.94) * mm, "end": v(1.53, -32.94) * mm});
            skLineSegment(sketch, "E855", {"start": v(1.53, -32.94) * mm, "end": v(2.01, -32.94) * mm});
            skLineSegment(sketch, "E856", {"start": v(2.01, -32.94) * mm, "end": v(2.34, -32.94) * mm});
            skLineSegment(sketch, "E857", {"start": v(2.34, -32.94) * mm, "end": v(2.6, -32.9) * mm});
            skLineSegment(sketch, "E858", {"start": v(2.6, -32.9) * mm, "end": v(2.8, -32.81) * mm});
            skLineSegment(sketch, "E859", {"start": v(2.8, -32.81) * mm, "end": v(2.96, -32.69) * mm});
            skLineSegment(sketch, "E860", {"start": v(2.96, -32.69) * mm, "end": v(3.07, -32.52) * mm});
            skLineSegment(sketch, "E861", {"start": v(3.07, -32.52) * mm, "end": v(3.14, -32.3) * mm});
            skLineSegment(sketch, "E862", {"start": v(3.14, -32.3) * mm, "end": v(3.18, -32.04) * mm});
            skLineSegment(sketch, "E863", {"start": v(3.18, -32.04) * mm, "end": v(3.2, -31.72) * mm});
            skLineSegment(sketch, "E864", {"start": v(3.2, -31.72) * mm, "end": v(3.18, -28.8) * mm});
            skLineSegment(sketch, "E865", {"start": v(3.18, -28.8) * mm, "end": v(3.16, -25.86) * mm});
            skLineSegment(sketch, "E866", {"start": v(3.16, -25.86) * mm, "end": v(3.15, -22.93) * mm});
            skLineSegment(sketch, "E867", {"start": v(3.15, -22.93) * mm, "end": v(3.15, -20) * mm});
            skLineSegment(sketch, "E868", {"start": v(3.15, -20) * mm, "end": v(3.15, -17.07) * mm});
            skLineSegment(sketch, "E869", {"start": v(3.15, -17.07) * mm, "end": v(3.16, -14.13) * mm});
            skLineSegment(sketch, "E870", {"start": v(3.16, -14.13) * mm, "end": v(3.19, -11.2) * mm});
            skLineSegment(sketch, "E871", {"start": v(3.19, -11.2) * mm, "end": v(3.23, -8.27) * mm});
            skLineSegment(sketch, "E872", {"start": v(3.23, -8.27) * mm, "end": v(3.22, -7.45) * mm});
            skLineSegment(sketch, "E873", {"start": v(3.22, -7.45) * mm, "end": v(3.15, -6.67) * mm});
            skLineSegment(sketch, "E874", {"start": v(3.15, -6.67) * mm, "end": v(3.02, -5.93) * mm});
            skLineSegment(sketch, "E875", {"start": v(3.02, -5.93) * mm, "end": v(2.82, -5.24) * mm});
            skLineSegment(sketch, "E876", {"start": v(2.82, -5.24) * mm, "end": v(2.52, -4.59) * mm});
            skLineSegment(sketch, "E877", {"start": v(2.52, -4.59) * mm, "end": v(2.13, -3.98) * mm});
            skLineSegment(sketch, "E878", {"start": v(2.13, -3.98) * mm, "end": v(1.63, -3.4) * mm});
            skLineSegment(sketch, "E879", {"start": v(1.63, -3.4) * mm, "end": v(1, -2.88) * mm});
            skLineSegment(sketch, "E880", {"start": v(1, -2.88) * mm, "end": v(0.92, -2.81) * mm});
            skLineSegment(sketch, "E881", {"start": v(0.92, -2.81) * mm, "end": v(0.84, -2.74) * mm});
            skLineSegment(sketch, "E882", {"start": v(0.84, -2.74) * mm, "end": v(0.75, -2.67) * mm});
            skLineSegment(sketch, "E883", {"start": v(0.75, -2.67) * mm, "end": v(0.65, -2.6) * mm});
            skLineSegment(sketch, "E884", {"start": v(0.65, -2.6) * mm, "end": v(0.56, -2.55) * mm});
            skLineSegment(sketch, "E885", {"start": v(0.56, -2.55) * mm, "end": v(0.47, -2.5) * mm});
            skLineSegment(sketch, "E886", {"start": v(0.47, -2.5) * mm, "end": v(0.38, -2.46) * mm});
            skLineSegment(sketch, "E887", {"start": v(0.38, -2.46) * mm, "end": v(0.29, -2.45) * mm});
            skLineSegment(sketch, "E888", {"start": v(0.29, -2.45) * mm, "end": v(-0.15, -2.44) * mm});
            skLineSegment(sketch, "E889", {"start": v(-0.15, -2.44) * mm, "end": v(-0.58, -2.43) * mm});
            skLineSegment(sketch, "E890", {"start": v(-0.58, -2.43) * mm, "end": v(-1.01, -2.42) * mm});
            skLineSegment(sketch, "E891", {"start": v(-1.01, -2.42) * mm, "end": v(-1.45, -2.42) * mm});
            skLineSegment(sketch, "E892", {"start": v(-1.45, -2.42) * mm, "end": v(-1.89, -2.42) * mm});
            skLineSegment(sketch, "E893", {"start": v(-1.89, -2.42) * mm, "end": v(-2.33, -2.43) * mm});
            skLineSegment(sketch, "E894", {"start": v(-2.33, -2.43) * mm, "end": v(-2.78, -2.43) * mm});
            skLineSegment(sketch, "E895", {"start": v(-2.78, -2.43) * mm, "end": v(-3.24, -2.43) * mm});
            skLineSegment(sketch, "E896", {"start": v(-3.28, 5.22) * mm, "end": v(-2.99, 5.22) * mm});
            skLineSegment(sketch, "E897", {"start": v(-2.99, 5.22) * mm, "end": v(-2.7, 5.21) * mm});
            skLineSegment(sketch, "E898", {"start": v(-2.7, 5.21) * mm, "end": v(-2.4, 5.2) * mm});
            skLineSegment(sketch, "E899", {"start": v(-2.4, 5.2) * mm, "end": v(-2.12, 5.2) * mm});
            skLineSegment(sketch, "E900", {"start": v(-2.12, 5.2) * mm, "end": v(-1.84, 5.2) * mm});
            skLineSegment(sketch, "E901", {"start": v(-1.84, 5.2) * mm, "end": v(-1.57, 5.2) * mm});
            skLineSegment(sketch, "E902", {"start": v(-1.57, 5.2) * mm, "end": v(-1.3, 5.22) * mm});
            skLineSegment(sketch, "E903", {"start": v(-1.3, 5.22) * mm, "end": v(-1.02, 5.24) * mm});
            skLineSegment(sketch, "E904", {"start": v(-1.02, 5.24) * mm, "end": v(-0.88, 5.26) * mm});
            skLineSegment(sketch, "E905", {"start": v(-0.88, 5.26) * mm, "end": v(-0.73, 5.3) * mm});
            skLineSegment(sketch, "E906", {"start": v(-0.73, 5.3) * mm, "end": v(-0.59, 5.34) * mm});
            skLineSegment(sketch, "E907", {"start": v(-0.59, 5.34) * mm, "end": v(-0.44, 5.4) * mm});
            skLineSegment(sketch, "E908", {"start": v(-0.44, 5.4) * mm, "end": v(-0.3, 5.46) * mm});
            skLineSegment(sketch, "E909", {"start": v(-0.3, 5.46) * mm, "end": v(-0.17, 5.54) * mm});
            skLineSegment(sketch, "E910", {"start": v(-0.17, 5.54) * mm, "end": v(-0.05, 5.62) * mm});
            skLineSegment(sketch, "E911", {"start": v(-0.05, 5.62) * mm, "end": v(0.05, 5.71) * mm});
            skLineSegment(sketch, "E912", {"start": v(0.05, 5.71) * mm, "end": v(0.4, 6.07) * mm});
            skLineSegment(sketch, "E913", {"start": v(0.4, 6.07) * mm, "end": v(0.76, 6.42) * mm});
            skLineSegment(sketch, "E914", {"start": v(0.76, 6.42) * mm, "end": v(1.1, 6.78) * mm});
            skLineSegment(sketch, "E915", {"start": v(1.1, 6.78) * mm, "end": v(1.45, 7.14) * mm});
            skLineSegment(sketch, "E916", {"start": v(1.45, 7.14) * mm, "end": v(1.79, 7.51) * mm});
            skLineSegment(sketch, "E917", {"start": v(1.79, 7.51) * mm, "end": v(2.12, 7.88) * mm});
            skLineSegment(sketch, "E918", {"start": v(2.12, 7.88) * mm, "end": v(2.46, 8.25) * mm});
            skLineSegment(sketch, "E919", {"start": v(2.46, 8.25) * mm, "end": v(2.79, 8.62) * mm});
            skLineSegment(sketch, "E920", {"start": v(2.79, 8.62) * mm, "end": v(2.86, 8.72) * mm});
            skLineSegment(sketch, "E921", {"start": v(2.86, 8.72) * mm, "end": v(2.93, 8.83) * mm});
            skLineSegment(sketch, "E922", {"start": v(2.93, 8.83) * mm, "end": v(3, 8.94) * mm});
            skLineSegment(sketch, "E923", {"start": v(3, 8.94) * mm, "end": v(3.05, 9.06) * mm});
            skLineSegment(sketch, "E924", {"start": v(3.05, 9.06) * mm, "end": v(3.1, 9.18) * mm});
            skLineSegment(sketch, "E925", {"start": v(3.1, 9.18) * mm, "end": v(3.13, 9.3) * mm});
            skLineSegment(sketch, "E926", {"start": v(3.13, 9.3) * mm, "end": v(3.15, 9.43) * mm});
            skLineSegment(sketch, "E927", {"start": v(3.15, 9.43) * mm, "end": v(3.16, 9.55) * mm});
            skLineSegment(sketch, "E928", {"start": v(3.16, 9.55) * mm, "end": v(3.16, 12.66) * mm});
            skLineSegment(sketch, "E929", {"start": v(3.16, 12.66) * mm, "end": v(3.17, 15.77) * mm});
            skLineSegment(sketch, "E930", {"start": v(3.17, 15.77) * mm, "end": v(3.17, 18.88) * mm});
            skLineSegment(sketch, "E931", {"start": v(3.17, 18.88) * mm, "end": v(3.17, 21.99) * mm});
            skLineSegment(sketch, "E932", {"start": v(3.17, 21.99) * mm, "end": v(3.17, 25.1) * mm});
            skLineSegment(sketch, "E933", {"start": v(3.17, 25.1) * mm, "end": v(3.17, 28.2) * mm});
            skLineSegment(sketch, "E934", {"start": v(3.17, 28.2) * mm, "end": v(3.17, 31.31) * mm});
            skLineSegment(sketch, "E935", {"start": v(3.17, 31.31) * mm, "end": v(3.18, 34.42) * mm});
            skLineSegment(sketch, "E936", {"start": v(3.18, 34.42) * mm, "end": v(3.17, 34.62) * mm});
            skLineSegment(sketch, "E937", {"start": v(3.17, 34.62) * mm, "end": v(3.14, 34.79) * mm});
            skLineSegment(sketch, "E938", {"start": v(3.14, 34.79) * mm, "end": v(3.1, 34.92) * mm});
            skLineSegment(sketch, "E939", {"start": v(3.1, 34.92) * mm, "end": v(3.02, 35.03) * mm});
            skLineSegment(sketch, "E940", {"start": v(3.02, 35.03) * mm, "end": v(2.91, 35.11) * mm});
            skLineSegment(sketch, "E941", {"start": v(2.91, 35.11) * mm, "end": v(2.78, 35.17) * mm});
            skLineSegment(sketch, "E942", {"start": v(2.78, 35.17) * mm, "end": v(2.62, 35.2) * mm});
            skLineSegment(sketch, "E943", {"start": v(2.62, 35.2) * mm, "end": v(2.42, 35.2) * mm});
            skLineSegment(sketch, "E944", {"start": v(2.42, 35.2) * mm, "end": v(1.83, 35.2) * mm});
            skLineSegment(sketch, "E945", {"start": v(1.83, 35.2) * mm, "end": v(1.25, 35.2) * mm});
            skLineSegment(sketch, "E946", {"start": v(1.25, 35.2) * mm, "end": v(0.66, 35.2) * mm});
            skLineSegment(sketch, "E947", {"start": v(0.66, 35.2) * mm, "end": v(0.07, 35.2) * mm});
            skLineSegment(sketch, "E948", {"start": v(0.07, 35.2) * mm, "end": v(-0.52, 35.2) * mm});
            skLineSegment(sketch, "E949", {"start": v(-0.52, 35.2) * mm, "end": v(-1.1, 35.2) * mm});
            skLineSegment(sketch, "E950", {"start": v(-1.1, 35.2) * mm, "end": v(-1.7, 35.21) * mm});
            skLineSegment(sketch, "E951", {"start": v(-1.7, 35.21) * mm, "end": v(-2.28, 35.23) * mm});
            skLineSegment(sketch, "E952", {"start": v(-2.28, 35.23) * mm, "end": v(-2.57, 35.22) * mm});
            skLineSegment(sketch, "E953", {"start": v(-2.57, 35.22) * mm, "end": v(-2.8, 35.18) * mm});
            skLineSegment(sketch, "E954", {"start": v(-2.8, 35.18) * mm, "end": v(-2.97, 35.1) * mm});
            skLineSegment(sketch, "E955", {"start": v(-2.97, 35.1) * mm, "end": v(-3.1, 34.98) * mm});
            skLineSegment(sketch, "E956", {"start": v(-3.1, 34.98) * mm, "end": v(-3.2, 34.83) * mm});
            skLineSegment(sketch, "E957", {"start": v(-3.2, 34.83) * mm, "end": v(-3.26, 34.64) * mm});
            skLineSegment(sketch, "E958", {"start": v(-3.26, 34.64) * mm, "end": v(-3.3, 34.4) * mm});
            skLineSegment(sketch, "E959", {"start": v(-3.3, 34.4) * mm, "end": v(-3.3, 34.13) * mm});
            skLineSegment(sketch, "E960", {"start": v(-3.3, 34.13) * mm, "end": v(-3.3, 30.64) * mm});
            skLineSegment(sketch, "E961", {"start": v(-3.3, 30.64) * mm, "end": v(-3.29, 27.16) * mm});
            skLineSegment(sketch, "E962", {"start": v(-3.29, 27.16) * mm, "end": v(-3.28, 23.67) * mm});
            skLineSegment(sketch, "E963", {"start": v(-3.28, 23.67) * mm, "end": v(-3.28, 20.18) * mm});
            skLineSegment(sketch, "E964", {"start": v(-3.28, 20.18) * mm, "end": v(-3.28, 16.7) * mm});
            skLineSegment(sketch, "E965", {"start": v(-3.28, 16.7) * mm, "end": v(-3.28, 13.21) * mm});
            skLineSegment(sketch, "E966", {"start": v(-3.28, 13.21) * mm, "end": v(-3.28, 9.73) * mm});
            skLineSegment(sketch, "E967", {"start": v(-3.28, 9.73) * mm, "end": v(-3.28, 6.24) * mm});
            skLineSegment(sketch, "E968", {"start": v(-3.28, 6.24) * mm, "end": v(-3.28, 6.13) * mm});
            skLineSegment(sketch, "E969", {"start": v(-3.28, 6.13) * mm, "end": v(-3.28, 6.02) * mm});
            skLineSegment(sketch, "E970", {"start": v(-3.28, 6.02) * mm, "end": v(-3.28, 5.9) * mm});
            skLineSegment(sketch, "E971", {"start": v(-3.28, 5.9) * mm, "end": v(-3.28, 5.79) * mm});
            skLineSegment(sketch, "E972", {"start": v(-3.28, 5.79) * mm, "end": v(-3.28, 5.66) * mm});
            skLineSegment(sketch, "E973", {"start": v(-3.28, 5.66) * mm, "end": v(-3.28, 5.52) * mm});
            skLineSegment(sketch, "E974", {"start": v(-3.28, 5.52) * mm, "end": v(-3.28, 5.38) * mm});
            skLineSegment(sketch, "E975", {"start": v(-3.28, 5.38) * mm, "end": v(-3.28, 5.22) * mm});
            skLineSegment(sketch, "E976", {"start": v(-36.03, 8.8) * mm, "end": v(-33.74, 8.8) * mm});
            skLineSegment(sketch, "E977", {"start": v(-33.74, 8.8) * mm, "end": v(-31.45, 8.8) * mm});
            skLineSegment(sketch, "E978", {"start": v(-31.45, 8.8) * mm, "end": v(-29.16, 8.8) * mm});
            skLineSegment(sketch, "E979", {"start": v(-29.16, 8.8) * mm, "end": v(-26.88, 8.8) * mm});
            skLineSegment(sketch, "E980", {"start": v(-26.88, 8.8) * mm, "end": v(-24.6, 8.8) * mm});
            skLineSegment(sketch, "E981", {"start": v(-24.6, 8.8) * mm, "end": v(-22.3, 8.8) * mm});
            skLineSegment(sketch, "E982", {"start": v(-22.3, 8.8) * mm, "end": v(-20.02, 8.8) * mm});
            skLineSegment(sketch, "E983", {"start": v(-20.02, 8.8) * mm, "end": v(-17.73, 8.8) * mm});
            skLineSegment(sketch, "E984", {"start": v(-17.73, 8.8) * mm, "end": v(-17.73, 2.98) * mm});
            skLineSegment(sketch, "E985", {"start": v(-17.73, 2.98) * mm, "end": v(-17.73, -2.84) * mm});
            skLineSegment(sketch, "E986", {"start": v(-17.73, -2.84) * mm, "end": v(-17.73, -8.65) * mm});
            skLineSegment(sketch, "E987", {"start": v(-17.73, -8.65) * mm, "end": v(-17.73, -14.46) * mm});
            skLineSegment(sketch, "E988", {"start": v(-17.73, -14.46) * mm, "end": v(-17.73, -20.27) * mm});
            skLineSegment(sketch, "E989", {"start": v(-17.73, -20.27) * mm, "end": v(-17.73, -26.09) * mm});
            skLineSegment(sketch, "E990", {"start": v(-17.73, -26.09) * mm, "end": v(-17.73, -31.92) * mm});
            skLineSegment(sketch, "E991", {"start": v(-17.73, -31.92) * mm, "end": v(-17.73, -37.75) * mm});
            skLineSegment(sketch, "E992", {"start": v(-17.73, -37.75) * mm, "end": v(-19.9, -36.85) * mm});
            skLineSegment(sketch, "E993", {"start": v(-19.9, -36.85) * mm, "end": v(-22, -35.84) * mm});
            skLineSegment(sketch, "E994", {"start": v(-22, -35.84) * mm, "end": v(-24, -34.72) * mm});
            skLineSegment(sketch, "E995", {"start": v(-24, -34.72) * mm, "end": v(-25.94, -33.48) * mm});
            skLineSegment(sketch, "E996", {"start": v(-25.94, -33.48) * mm, "end": v(-27.78, -32.14) * mm});
            skLineSegment(sketch, "E997", {"start": v(-27.78, -32.14) * mm, "end": v(-29.56, -30.69) * mm});
            skLineSegment(sketch, "E998", {"start": v(-29.56, -30.69) * mm, "end": v(-31.25, -29.13) * mm});
            skLineSegment(sketch, "E999", {"start": v(-31.25, -29.13) * mm, "end": v(-32.87, -27.46) * mm});
            skLineSegment(sketch, "E1000", {"start": v(-32.87, -27.46) * mm, "end": v(-34.98, -24.98) * mm});
            skLineSegment(sketch, "E1001", {"start": v(-34.98, -24.98) * mm, "end": v(-36.88, -22.4) * mm});
            skLineSegment(sketch, "E1002", {"start": v(-36.88, -22.4) * mm, "end": v(-38.57, -19.71) * mm});
            skLineSegment(sketch, "E1003", {"start": v(-38.57, -19.71) * mm, "end": v(-40.04, -16.92) * mm});
            skLineSegment(sketch, "E1004", {"start": v(-40.04, -16.92) * mm, "end": v(-41.3, -14.01) * mm});
            skLineSegment(sketch, "E1005", {"start": v(-41.3, -14.01) * mm, "end": v(-42.36, -11) * mm});
            skLineSegment(sketch, "E1006", {"start": v(-42.36, -11) * mm, "end": v(-43.21, -7.88) * mm});
            skLineSegment(sketch, "E1007", {"start": v(-43.21, -7.88) * mm, "end": v(-43.85, -4.65) * mm});
            skLineSegment(sketch, "E1008", {"start": v(-43.85, -4.65) * mm, "end": v(-43.16, -4.65) * mm});
            skLineSegment(sketch, "E1009", {"start": v(-43.16, -4.65) * mm, "end": v(-42.46, -4.65) * mm});
            skLineSegment(sketch, "E1010", {"start": v(-42.46, -4.65) * mm, "end": v(-41.78, -4.65) * mm});
            skLineSegment(sketch, "E1011", {"start": v(-41.78, -4.65) * mm, "end": v(-41.1, -4.65) * mm});
            skLineSegment(sketch, "E1012", {"start": v(-41.1, -4.65) * mm, "end": v(-40.41, -4.65) * mm});
            skLineSegment(sketch, "E1013", {"start": v(-40.41, -4.65) * mm, "end": v(-39.74, -4.65) * mm});
            skLineSegment(sketch, "E1014", {"start": v(-39.74, -4.65) * mm, "end": v(-39.06, -4.65) * mm});
            skLineSegment(sketch, "E1015", {"start": v(-39.06, -4.65) * mm, "end": v(-38.38, -4.65) * mm});
            skLineSegment(sketch, "E1016", {"start": v(-38.38, -4.65) * mm, "end": v(-37.75, -4.65) * mm});
            skLineSegment(sketch, "E1017", {"start": v(-37.75, -4.65) * mm, "end": v(-37.26, -4.68) * mm});
            skLineSegment(sketch, "E1018", {"start": v(-37.26, -4.68) * mm, "end": v(-36.9, -4.75) * mm});
            skLineSegment(sketch, "E1019", {"start": v(-36.9, -4.75) * mm, "end": v(-36.63, -4.88) * mm});
            skLineSegment(sketch, "E1020", {"start": v(-36.63, -4.88) * mm, "end": v(-36.44, -5.1) * mm});
            skLineSegment(sketch, "E1021", {"start": v(-36.44, -5.1) * mm, "end": v(-36.3, -5.42) * mm});
            skLineSegment(sketch, "E1022", {"start": v(-36.3, -5.42) * mm, "end": v(-36.17, -5.88) * mm});
            skLineSegment(sketch, "E1023", {"start": v(-36.17, -5.88) * mm, "end": v(-36.04, -6.49) * mm});
            skLineSegment(sketch, "E1024", {"start": v(-36.04, -6.49) * mm, "end": v(-35.4, -9.01) * mm});
            skLineSegment(sketch, "E1025", {"start": v(-35.4, -9.01) * mm, "end": v(-34.58, -11.43) * mm});
            skLineSegment(sketch, "E1026", {"start": v(-34.58, -11.43) * mm, "end": v(-33.58, -13.74) * mm});
            skLineSegment(sketch, "E1027", {"start": v(-33.58, -13.74) * mm, "end": v(-32.4, -15.95) * mm});
            skLineSegment(sketch, "E1028", {"start": v(-32.4, -15.95) * mm, "end": v(-31.06, -18.06) * mm});
            skLineSegment(sketch, "E1029", {"start": v(-31.06, -18.06) * mm, "end": v(-29.55, -20.08) * mm});
            skLineSegment(sketch, "E1030", {"start": v(-29.55, -20.08) * mm, "end": v(-27.89, -22.02) * mm});
            skLineSegment(sketch, "E1031", {"start": v(-27.89, -22.02) * mm, "end": v(-26.08, -23.87) * mm});
            skLineSegment(sketch, "E1032", {"start": v(-26.08, -23.87) * mm, "end": v(-26.03, -23.92) * mm});
            skLineSegment(sketch, "E1033", {"start": v(-26.03, -23.92) * mm, "end": v(-25.97, -23.96) * mm});
            skLineSegment(sketch, "E1034", {"start": v(-25.97, -23.96) * mm, "end": v(-25.9, -24.01) * mm});
            skLineSegment(sketch, "E1035", {"start": v(-25.9, -24.01) * mm, "end": v(-25.84, -24.06) * mm});
            skLineSegment(sketch, "E1036", {"start": v(-25.84, -24.06) * mm, "end": v(-25.77, -24.12) * mm});
            skLineSegment(sketch, "E1037", {"start": v(-25.77, -24.12) * mm, "end": v(-25.7, -24.18) * mm});
            skLineSegment(sketch, "E1038", {"start": v(-25.7, -24.18) * mm, "end": v(-25.61, -24.24) * mm});
            skLineSegment(sketch, "E1039", {"start": v(-25.61, -24.24) * mm, "end": v(-25.52, -24.32) * mm});
            skLineSegment(sketch, "E1040", {"start": v(-25.52, -24.32) * mm, "end": v(-25.52, -21.13) * mm});
            skLineSegment(sketch, "E1041", {"start": v(-25.52, -21.13) * mm, "end": v(-25.52, -17.94) * mm});
            skLineSegment(sketch, "E1042", {"start": v(-25.52, -17.94) * mm, "end": v(-25.52, -14.77) * mm});
            skLineSegment(sketch, "E1043", {"start": v(-25.52, -14.77) * mm, "end": v(-25.52, -11.6) * mm});
            skLineSegment(sketch, "E1044", {"start": v(-25.52, -11.6) * mm, "end": v(-25.52, -8.43) * mm});
            skLineSegment(sketch, "E1045", {"start": v(-25.52, -8.43) * mm, "end": v(-25.52, -5.25) * mm});
            skLineSegment(sketch, "E1046", {"start": v(-25.52, -5.25) * mm, "end": v(-25.52, -2.07) * mm});
            skLineSegment(sketch, "E1047", {"start": v(-25.52, -2.07) * mm, "end": v(-25.52, 1.11) * mm});
            skLineSegment(sketch, "E1048", {"start": v(-25.52, 1.11) * mm, "end": v(-27.84, 1.11) * mm});
            skLineSegment(sketch, "E1049", {"start": v(-27.84, 1.11) * mm, "end": v(-30.16, 1.11) * mm});
            skLineSegment(sketch, "E1050", {"start": v(-30.16, 1.11) * mm, "end": v(-32.48, 1.11) * mm});
            skLineSegment(sketch, "E1051", {"start": v(-32.48, 1.11) * mm, "end": v(-34.81, 1.11) * mm});
            skLineSegment(sketch, "E1052", {"start": v(-34.81, 1.11) * mm, "end": v(-37.14, 1.11) * mm});
            skLineSegment(sketch, "E1053", {"start": v(-37.14, 1.11) * mm, "end": v(-39.49, 1.11) * mm});
            skLineSegment(sketch, "E1054", {"start": v(-39.49, 1.11) * mm, "end": v(-41.84, 1.11) * mm});
            skLineSegment(sketch, "E1055", {"start": v(-41.84, 1.11) * mm, "end": v(-44.2, 1.11) * mm});
            skLineSegment(sketch, "E1056", {"start": v(-44.2, 1.11) * mm, "end": v(-44.02, 4.34) * mm});
            skLineSegment(sketch, "E1057", {"start": v(-44.02, 4.34) * mm, "end": v(-43.64, 7.48) * mm});
            skLineSegment(sketch, "E1058", {"start": v(-43.64, 7.48) * mm, "end": v(-43.04, 10.54) * mm});
            skLineSegment(sketch, "E1059", {"start": v(-43.04, 10.54) * mm, "end": v(-42.23, 13.53) * mm});
            skLineSegment(sketch, "E1060", {"start": v(-42.23, 13.53) * mm, "end": v(-41.19, 16.44) * mm});
            skLineSegment(sketch, "E1061", {"start": v(-41.19, 16.44) * mm, "end": v(-39.93, 19.27) * mm});
            skLineSegment(sketch, "E1062", {"start": v(-39.93, 19.27) * mm, "end": v(-38.43, 22.03) * mm});
            skLineSegment(sketch, "E1063", {"start": v(-38.43, 22.03) * mm, "end": v(-36.7, 24.71) * mm});
            skLineSegment(sketch, "E1064", {"start": v(-36.7, 24.71) * mm, "end": v(-34.84, 27.21) * mm});
            skLineSegment(sketch, "E1065", {"start": v(-34.84, 27.21) * mm, "end": v(-32.82, 29.55) * mm});
            skLineSegment(sketch, "E1066", {"start": v(-32.82, 29.55) * mm, "end": v(-30.67, 31.7) * mm});
            skLineSegment(sketch, "E1067", {"start": v(-30.67, 31.7) * mm, "end": v(-28.38, 33.7) * mm});
            skLineSegment(sketch, "E1068", {"start": v(-28.38, 33.7) * mm, "end": v(-25.94, 35.52) * mm});
            skLineSegment(sketch, "E1069", {"start": v(-25.94, 35.52) * mm, "end": v(-23.35, 37.16) * mm});
            skLineSegment(sketch, "E1070", {"start": v(-23.35, 37.16) * mm, "end": v(-20.62, 38.64) * mm});
            skLineSegment(sketch, "E1071", {"start": v(-20.62, 38.64) * mm, "end": v(-17.73, 39.94) * mm});
            skLineSegment(sketch, "E1072", {"start": v(-17.73, 39.94) * mm, "end": v(-17.73, 36.84) * mm});
            skLineSegment(sketch, "E1073", {"start": v(-17.73, 36.84) * mm, "end": v(-17.73, 33.75) * mm});
            skLineSegment(sketch, "E1074", {"start": v(-17.73, 33.75) * mm, "end": v(-17.73, 30.67) * mm});
            skLineSegment(sketch, "E1075", {"start": v(-17.73, 30.67) * mm, "end": v(-17.73, 27.6) * mm});
            skLineSegment(sketch, "E1076", {"start": v(-17.73, 27.6) * mm, "end": v(-17.73, 24.52) * mm});
            skLineSegment(sketch, "E1077", {"start": v(-17.73, 24.52) * mm, "end": v(-17.73, 21.46) * mm});
            skLineSegment(sketch, "E1078", {"start": v(-17.73, 21.46) * mm, "end": v(-17.73, 18.39) * mm});
            skLineSegment(sketch, "E1079", {"start": v(-17.73, 18.39) * mm, "end": v(-17.73, 15.31) * mm});
            skLineSegment(sketch, "E1080", {"start": v(-17.73, 15.31) * mm, "end": v(-18.68, 15.31) * mm});
            skLineSegment(sketch, "E1081", {"start": v(-18.68, 15.31) * mm, "end": v(-19.63, 15.31) * mm});
            skLineSegment(sketch, "E1082", {"start": v(-19.63, 15.31) * mm, "end": v(-20.58, 15.31) * mm});
            skLineSegment(sketch, "E1083", {"start": v(-20.58, 15.31) * mm, "end": v(-21.54, 15.31) * mm});
            skLineSegment(sketch, "E1084", {"start": v(-21.54, 15.31) * mm, "end": v(-22.5, 15.31) * mm});
            skLineSegment(sketch, "E1085", {"start": v(-22.5, 15.31) * mm, "end": v(-23.46, 15.31) * mm});
            skLineSegment(sketch, "E1086", {"start": v(-23.46, 15.31) * mm, "end": v(-24.43, 15.31) * mm});
            skLineSegment(sketch, "E1087", {"start": v(-24.43, 15.31) * mm, "end": v(-25.41, 15.31) * mm});
            skLineSegment(sketch, "E1088", {"start": v(-25.41, 15.31) * mm, "end": v(-25.41, 16.7) * mm});
            skLineSegment(sketch, "E1089", {"start": v(-25.41, 16.7) * mm, "end": v(-25.41, 18.07) * mm});
            skLineSegment(sketch, "E1090", {"start": v(-25.41, 18.07) * mm, "end": v(-25.41, 19.46) * mm});
            skLineSegment(sketch, "E1091", {"start": v(-25.41, 19.46) * mm, "end": v(-25.41, 20.84) * mm});
            skLineSegment(sketch, "E1092", {"start": v(-25.41, 20.84) * mm, "end": v(-25.41, 22.22) * mm});
            skLineSegment(sketch, "E1093", {"start": v(-25.41, 22.22) * mm, "end": v(-25.41, 23.61) * mm});
            skLineSegment(sketch, "E1094", {"start": v(-25.41, 23.61) * mm, "end": v(-25.41, 25) * mm});
            skLineSegment(sketch, "E1095", {"start": v(-25.41, 25) * mm, "end": v(-25.41, 26.4) * mm});
            skLineSegment(sketch, "E1096", {"start": v(-25.41, 26.4) * mm, "end": v(-26.82, 25.47) * mm});
            skLineSegment(sketch, "E1097", {"start": v(-26.82, 25.47) * mm, "end": v(-28.43, 23.78) * mm});
            skLineSegment(sketch, "E1098", {"start": v(-28.43, 23.78) * mm, "end": v(-30.15, 21.54) * mm});
            skLineSegment(sketch, "E1099", {"start": v(-30.15, 21.54) * mm, "end": v(-31.84, 18.94) * mm});
            skLineSegment(sketch, "E1100", {"start": v(-31.84, 18.94) * mm, "end": v(-33.39, 16.17) * mm});
            skLineSegment(sketch, "E1101", {"start": v(-33.39, 16.17) * mm, "end": v(-34.68, 13.43) * mm});
            skLineSegment(sketch, "E1102", {"start": v(-34.68, 13.43) * mm, "end": v(-35.6, 10.9) * mm});
            skLineSegment(sketch, "E1103", {"start": v(-35.6, 10.9) * mm, "end": v(-36.03, 8.8) * mm});
            skLineSegment(sketch, "E1104", {"start": v(17.66, 39.81) * mm, "end": v(21.86, 37.96) * mm});
            skLineSegment(sketch, "E1105", {"start": v(21.86, 37.96) * mm, "end": v(25.99, 35.45) * mm});
            skLineSegment(sketch, "E1106", {"start": v(25.99, 35.45) * mm, "end": v(29.93, 32.33) * mm});
            skLineSegment(sketch, "E1107", {"start": v(29.93, 32.33) * mm, "end": v(33.6, 28.63) * mm});
            skLineSegment(sketch, "E1108", {"start": v(33.6, 28.63) * mm, "end": v(36.86, 24.41) * mm});
            skLineSegment(sketch, "E1109", {"start": v(36.86, 24.41) * mm, "end": v(39.63, 19.71) * mm});
            skLineSegment(sketch, "E1110", {"start": v(39.63, 19.71) * mm, "end": v(41.8, 14.59) * mm});
            skLineSegment(sketch, "E1111", {"start": v(41.8, 14.59) * mm, "end": v(43.24, 9.07) * mm});
            skLineSegment(sketch, "E1112", {"start": v(43.24, 9.07) * mm, "end": v(42.79, 9.07) * mm});
            skLineSegment(sketch, "E1113", {"start": v(42.79, 9.07) * mm, "end": v(42.33, 9.07) * mm});
            skLineSegment(sketch, "E1114", {"start": v(42.33, 9.07) * mm, "end": v(41.88, 9.07) * mm});
            skLineSegment(sketch, "E1115", {"start": v(41.88, 9.07) * mm, "end": v(41.43, 9.07) * mm});
            skLineSegment(sketch, "E1116", {"start": v(41.43, 9.07) * mm, "end": v(40.98, 9.07) * mm});
            skLineSegment(sketch, "E1117", {"start": v(40.98, 9.07) * mm, "end": v(40.53, 9.07) * mm});
            skLineSegment(sketch, "E1118", {"start": v(40.53, 9.07) * mm, "end": v(40.08, 9.07) * mm});
            skLineSegment(sketch, "E1119", {"start": v(40.08, 9.07) * mm, "end": v(39.64, 9.07) * mm});
            skLineSegment(sketch, "E1120", {"start": v(39.64, 9.07) * mm, "end": v(39.2, 9.07) * mm});
            skLineSegment(sketch, "E1121", {"start": v(39.2, 9.07) * mm, "end": v(38.75, 9.07) * mm});
            skLineSegment(sketch, "E1122", {"start": v(38.75, 9.07) * mm, "end": v(38.3, 9.07) * mm});
            skLineSegment(sketch, "E1123", {"start": v(38.3, 9.07) * mm, "end": v(37.85, 9.07) * mm});
            skLineSegment(sketch, "E1124", {"start": v(37.85, 9.07) * mm, "end": v(37.4, 9.07) * mm});
            skLineSegment(sketch, "E1125", {"start": v(37.4, 9.07) * mm, "end": v(36.95, 9.07) * mm});
            skLineSegment(sketch, "E1126", {"start": v(36.95, 9.07) * mm, "end": v(36.49, 9.07) * mm});
            skLineSegment(sketch, "E1127", {"start": v(36.49, 9.07) * mm, "end": v(36.03, 9.07) * mm});
            skLineSegment(sketch, "E1128", {"start": v(36.03, 9.07) * mm, "end": v(35.26, 11.57) * mm});
            skLineSegment(sketch, "E1129", {"start": v(35.26, 11.57) * mm, "end": v(34.37, 13.98) * mm});
            skLineSegment(sketch, "E1130", {"start": v(34.37, 13.98) * mm, "end": v(33.33, 16.3) * mm});
            skLineSegment(sketch, "E1131", {"start": v(33.33, 16.3) * mm, "end": v(32.13, 18.54) * mm});
            skLineSegment(sketch, "E1132", {"start": v(32.13, 18.54) * mm, "end": v(30.75, 20.68) * mm});
            skLineSegment(sketch, "E1133", {"start": v(30.75, 20.68) * mm, "end": v(29.2, 22.72) * mm});
            skLineSegment(sketch, "E1134", {"start": v(29.2, 22.72) * mm, "end": v(27.43, 24.65) * mm});
            skLineSegment(sketch, "E1135", {"start": v(27.43, 24.65) * mm, "end": v(25.45, 26.47) * mm});
            skLineSegment(sketch, "E1136", {"start": v(25.45, 26.47) * mm, "end": v(25.45, 20.15) * mm});
            skLineSegment(sketch, "E1137", {"start": v(25.45, 20.15) * mm, "end": v(25.45, 13.84) * mm});
            skLineSegment(sketch, "E1138", {"start": v(25.45, 13.84) * mm, "end": v(25.45, 7.54) * mm});
            skLineSegment(sketch, "E1139", {"start": v(25.45, 7.54) * mm, "end": v(25.45, 1.24) * mm});
            skLineSegment(sketch, "E1140", {"start": v(25.45, 1.24) * mm, "end": v(25.45, -5.06) * mm});
            skLineSegment(sketch, "E1141", {"start": v(25.45, -5.06) * mm, "end": v(25.45, -11.37) * mm});
            skLineSegment(sketch, "E1142", {"start": v(25.45, -11.37) * mm, "end": v(25.45, -17.7) * mm});
            skLineSegment(sketch, "E1143", {"start": v(25.45, -17.7) * mm, "end": v(25.45, -24.04) * mm});
            skLineSegment(sketch, "E1144", {"start": v(25.45, -24.04) * mm, "end": v(26.48, -23.13) * mm});
            skLineSegment(sketch, "E1145", {"start": v(26.48, -23.13) * mm, "end": v(27.46, -22.19) * mm});
            skLineSegment(sketch, "E1146", {"start": v(27.46, -22.19) * mm, "end": v(28.37, -21.21) * mm});
            skLineSegment(sketch, "E1147", {"start": v(28.37, -21.21) * mm, "end": v(29.22, -20.2) * mm});
            skLineSegment(sketch, "E1148", {"start": v(29.22, -20.2) * mm, "end": v(30.02, -19.16) * mm});
            skLineSegment(sketch, "E1149", {"start": v(30.02, -19.16) * mm, "end": v(30.78, -18.1) * mm});
            skLineSegment(sketch, "E1150", {"start": v(30.78, -18.1) * mm, "end": v(31.5, -17) * mm});
            skLineSegment(sketch, "E1151", {"start": v(31.5, -17) * mm, "end": v(32.17, -15.87) * mm});
            skLineSegment(sketch, "E1152", {"start": v(32.17, -15.87) * mm, "end": v(32.81, -14.73) * mm});
            skLineSegment(sketch, "E1153", {"start": v(32.81, -14.73) * mm, "end": v(33.41, -13.56) * mm});
            skLineSegment(sketch, "E1154", {"start": v(33.41, -13.56) * mm, "end": v(33.97, -12.38) * mm});
            skLineSegment(sketch, "E1155", {"start": v(33.97, -12.38) * mm, "end": v(34.49, -11.18) * mm});
            skLineSegment(sketch, "E1156", {"start": v(34.49, -11.18) * mm, "end": v(34.95, -9.95) * mm});
            skLineSegment(sketch, "E1157", {"start": v(34.95, -9.95) * mm, "end": v(35.37, -8.7) * mm});
            skLineSegment(sketch, "E1158", {"start": v(35.37, -8.7) * mm, "end": v(35.73, -7.43) * mm});
            skLineSegment(sketch, "E1159", {"start": v(35.73, -7.43) * mm, "end": v(36.03, -6.14) * mm});
            skLineSegment(sketch, "E1160", {"start": v(36.03, -6.14) * mm, "end": v(36.95, -6.14) * mm});
            skLineSegment(sketch, "E1161", {"start": v(36.95, -6.14) * mm, "end": v(37.87, -6.14) * mm});
            skLineSegment(sketch, "E1162", {"start": v(37.87, -6.14) * mm, "end": v(38.8, -6.14) * mm});
            skLineSegment(sketch, "E1163", {"start": v(38.8, -6.14) * mm, "end": v(39.71, -6.14) * mm});
            skLineSegment(sketch, "E1164", {"start": v(39.71, -6.14) * mm, "end": v(40.63, -6.14) * mm});
            skLineSegment(sketch, "E1165", {"start": v(40.63, -6.14) * mm, "end": v(41.56, -6.14) * mm});
            skLineSegment(sketch, "E1166", {"start": v(41.56, -6.14) * mm, "end": v(42.5, -6.14) * mm});
            skLineSegment(sketch, "E1167", {"start": v(42.5, -6.14) * mm, "end": v(43.44, -6.14) * mm});
            skLineSegment(sketch, "E1168", {"start": v(43.44, -6.14) * mm, "end": v(42.97, -8.45) * mm});
            skLineSegment(sketch, "E1169", {"start": v(42.97, -8.45) * mm, "end": v(42.39, -10.72) * mm});
            skLineSegment(sketch, "E1170", {"start": v(42.39, -10.72) * mm, "end": v(41.67, -12.92) * mm});
            skLineSegment(sketch, "E1171", {"start": v(41.67, -12.92) * mm, "end": v(40.84, -15.07) * mm});
            skLineSegment(sketch, "E1172", {"start": v(40.84, -15.07) * mm, "end": v(39.89, -17.18) * mm});
            skLineSegment(sketch, "E1173", {"start": v(39.89, -17.18) * mm, "end": v(38.82, -19.23) * mm});
            skLineSegment(sketch, "E1174", {"start": v(38.82, -19.23) * mm, "end": v(37.63, -21.23) * mm});
            skLineSegment(sketch, "E1175", {"start": v(37.63, -21.23) * mm, "end": v(36.33, -23.19) * mm});
            skLineSegment(sketch, "E1176", {"start": v(36.33, -23.19) * mm, "end": v(34.3, -25.8) * mm});
            skLineSegment(sketch, "E1177", {"start": v(34.3, -25.8) * mm, "end": v(32.07, -28.21) * mm});
            skLineSegment(sketch, "E1178", {"start": v(32.07, -28.21) * mm, "end": v(29.7, -30.4) * mm});
            skLineSegment(sketch, "E1179", {"start": v(29.7, -30.4) * mm, "end": v(27.24, -32.35) * mm});
            skLineSegment(sketch, "E1180", {"start": v(27.24, -32.35) * mm, "end": v(24.75, -34.07) * mm});
            skLineSegment(sketch, "E1181", {"start": v(24.75, -34.07) * mm, "end": v(22.3, -35.53) * mm});
            skLineSegment(sketch, "E1182", {"start": v(22.3, -35.53) * mm, "end": v(19.9, -36.73) * mm});
            skLineSegment(sketch, "E1183", {"start": v(19.9, -36.73) * mm, "end": v(17.66, -37.67) * mm});
            skLineSegment(sketch, "E1184", {"start": v(17.66, -37.67) * mm, "end": v(17.66, -27.98) * mm});
            skLineSegment(sketch, "E1185", {"start": v(17.66, -27.98) * mm, "end": v(17.66, -18.3) * mm});
            skLineSegment(sketch, "E1186", {"start": v(17.66, -18.3) * mm, "end": v(17.66, -8.6) * mm});
            skLineSegment(sketch, "E1187", {"start": v(17.66, -8.6) * mm, "end": v(17.66, 1.07) * mm});
            skLineSegment(sketch, "E1188", {"start": v(17.66, 1.07) * mm, "end": v(17.66, 10.76) * mm});
            skLineSegment(sketch, "E1189", {"start": v(17.66, 10.76) * mm, "end": v(17.66, 20.44) * mm});
            skLineSegment(sketch, "E1190", {"start": v(17.66, 20.44) * mm, "end": v(17.66, 30.13) * mm});
            skLineSegment(sketch, "E1191", {"start": v(17.66, 30.13) * mm, "end": v(17.66, 39.81) * mm});
            skLineSegment(sketch, "E1192", {"start": v(-36.95, -30.78) * mm, "end": v(-34.88, -32.14) * mm});
            skLineSegment(sketch, "E1193", {"start": v(-34.88, -32.14) * mm, "end": v(-33.24, -33.92) * mm});
            skLineSegment(sketch, "E1194", {"start": v(-33.24, -33.92) * mm, "end": v(-31.97, -35.09) * mm});
            skLineSegment(sketch, "E1195", {"start": v(-31.97, -35.09) * mm, "end": v(-30.8, -36.35) * mm});
            skLineSegment(sketch, "E1196", {"start": v(-30.8, -36.35) * mm, "end": v(-29.88, -37.57) * mm});
            skLineSegment(sketch, "E1197", {"start": v(-29.88, -37.57) * mm, "end": v(-29, -38.82) * mm});
            skLineSegment(sketch, "E1198", {"start": v(-29, -38.82) * mm, "end": v(-28.7, -39.06) * mm});
            skLineSegment(sketch, "E1199", {"start": v(-28.7, -39.06) * mm, "end": v(-28.36, -39.27) * mm});
            skLineSegment(sketch, "E1200", {"start": v(-28.36, -39.27) * mm, "end": v(-27.16, -40.18) * mm});
            skLineSegment(sketch, "E1201", {"start": v(-27.16, -40.18) * mm, "end": v(-25.97, -41.11) * mm});
            skLineSegment(sketch, "E1202", {"start": v(-25.97, -41.11) * mm, "end": v(-25.92, -41.3) * mm});
            skLineSegment(sketch, "E1203", {"start": v(-25.92, -41.3) * mm, "end": v(-25.91, -41.53) * mm});
            skLineSegment(sketch, "E1204", {"start": v(-25.91, -41.53) * mm, "end": v(-25.13, -41.66) * mm});
            skLineSegment(sketch, "E1205", {"start": v(-25.13, -41.66) * mm, "end": v(-24.28, -41.8) * mm});
            skLineSegment(sketch, "E1206", {"start": v(-24.28, -41.8) * mm, "end": v(-24.17, -41.6) * mm});
            skLineSegment(sketch, "E1207", {"start": v(-24.17, -41.6) * mm, "end": v(-24, -41.28) * mm});
            skLineSegment(sketch, "E1208", {"start": v(-24, -41.28) * mm, "end": v(-22.73, -41.98) * mm});
            skLineSegment(sketch, "E1209", {"start": v(-22.73, -41.98) * mm, "end": v(-21.85, -43.14) * mm});
            skLineSegment(sketch, "E1210", {"start": v(-21.85, -43.14) * mm, "end": v(-21.54, -43.27) * mm});
            skLineSegment(sketch, "E1211", {"start": v(-21.54, -43.27) * mm, "end": v(-21.06, -43.27) * mm});
            skLineSegment(sketch, "E1212", {"start": v(-21.06, -43.27) * mm, "end": v(-19.27, -43.34) * mm});
            skLineSegment(sketch, "E1213", {"start": v(-19.27, -43.34) * mm, "end": v(-18.15, -44.67) * mm});
            skLineSegment(sketch, "E1214", {"start": v(-18.15, -44.67) * mm, "end": v(-17.53, -44.5) * mm});
            skLineSegment(sketch, "E1215", {"start": v(-17.53, -44.5) * mm, "end": v(-16.9, -44.34) * mm});
            skLineSegment(sketch, "E1216", {"start": v(-16.9, -44.34) * mm, "end": v(-16.96, -44.47) * mm});
            skLineSegment(sketch, "E1217", {"start": v(-16.96, -44.47) * mm, "end": v(-17.01, -44.6) * mm});
            skLineSegment(sketch, "E1218", {"start": v(-17.01, -44.6) * mm, "end": v(-16.38, -45.04) * mm});
            skLineSegment(sketch, "E1219", {"start": v(-16.38, -45.04) * mm, "end": v(-15.72, -45.43) * mm});
            skLineSegment(sketch, "E1220", {"start": v(-15.72, -45.43) * mm, "end": v(-14.85, -45.77) * mm});
            skLineSegment(sketch, "E1221", {"start": v(-14.85, -45.77) * mm, "end": v(-13.95, -46) * mm});
            skLineSegment(sketch, "E1222", {"start": v(-13.95, -46) * mm, "end": v(-13.3, -46) * mm});
            skLineSegment(sketch, "E1223", {"start": v(-13.3, -46) * mm, "end": v(-12.63, -45.92) * mm});
            skLineSegment(sketch, "E1224", {"start": v(-12.63, -45.92) * mm, "end": v(-12.2, -45.9) * mm});
            skLineSegment(sketch, "E1225", {"start": v(-12.2, -45.9) * mm, "end": v(-11.77, -45.95) * mm});
            skLineSegment(sketch, "E1226", {"start": v(-11.77, -45.95) * mm, "end": v(-6.32, -47) * mm});
            skLineSegment(sketch, "E1227", {"start": v(-6.32, -47) * mm, "end": v(-0.8, -47.46) * mm});
            skLineSegment(sketch, "E1228", {"start": v(-0.8, -47.46) * mm, "end": v(0, -47.6) * mm});
            skLineSegment(sketch, "E1229", {"start": v(0, -47.6) * mm, "end": v(0.84, -47.8) * mm});
            skLineSegment(sketch, "E1230", {"start": v(0.84, -47.8) * mm, "end": v(2.23, -47.7) * mm});
            skLineSegment(sketch, "E1231", {"start": v(2.23, -47.7) * mm, "end": v(3.7, -47.53) * mm});
            skLineSegment(sketch, "E1232", {"start": v(3.7, -47.53) * mm, "end": v(6.76, -46.98) * mm});
            skLineSegment(sketch, "E1233", {"start": v(6.76, -46.98) * mm, "end": v(9.81, -46.42) * mm});
            skLineSegment(sketch, "E1234", {"start": v(9.81, -46.42) * mm, "end": v(10.58, -46.37) * mm});
            skLineSegment(sketch, "E1235", {"start": v(10.58, -46.37) * mm, "end": v(11.36, -46.38) * mm});
            skLineSegment(sketch, "E1236", {"start": v(11.36, -46.38) * mm, "end": v(11.54, -46.37) * mm});
            skLineSegment(sketch, "E1237", {"start": v(11.54, -46.37) * mm, "end": v(11.69, -46.33) * mm});
            skLineSegment(sketch, "E1238", {"start": v(11.69, -46.33) * mm, "end": v(13.64, -45.4) * mm});
            skLineSegment(sketch, "E1239", {"start": v(13.64, -45.4) * mm, "end": v(15.76, -44.96) * mm});
            skLineSegment(sketch, "E1240", {"start": v(15.76, -44.96) * mm, "end": v(16.91, -44.5) * mm});
            skLineSegment(sketch, "E1241", {"start": v(16.91, -44.5) * mm, "end": v(18.05, -43.91) * mm});
            skLineSegment(sketch, "E1242", {"start": v(18.05, -43.91) * mm, "end": v(20.8, -43.13) * mm});
            skLineSegment(sketch, "E1243", {"start": v(20.8, -43.13) * mm, "end": v(23.67, -42.95) * mm});
            skLineSegment(sketch, "E1244", {"start": v(23.67, -42.95) * mm, "end": v(8.27, -48.47) * mm});
            skLineSegment(sketch, "E1245", {"start": v(8.27, -48.47) * mm, "end": v(-8.07, -48.46) * mm});
            skLineSegment(sketch, "E1246", {"start": v(-8.07, -48.46) * mm, "end": v(-25.47, -42.1) * mm});
            skLineSegment(sketch, "E1247", {"start": v(-25.47, -42.1) * mm, "end": v(-39.3, -29.6) * mm});
            skLineSegment(sketch, "E1248", {"start": v(-39.3, -29.6) * mm, "end": v(-38.27, -29.64) * mm});
            skLineSegment(sketch, "E1249", {"start": v(-38.27, -29.64) * mm, "end": v(-37.38, -29.72) * mm});
            skLineSegment(sketch, "E1250", {"start": v(-37.38, -29.72) * mm, "end": v(-36.71, -30.04) * mm});
            skLineSegment(sketch, "E1251", {"start": v(-36.71, -30.04) * mm, "end": v(-36.95, -30.78) * mm});
            skLineSegment(sketch, "E1252", {"start": v(25.66, 40.44) * mm, "end": v(28.15, 40.4) * mm});
            skLineSegment(sketch, "E1253", {"start": v(28.15, 40.4) * mm, "end": v(30.33, 39.17) * mm});
            skLineSegment(sketch, "E1254", {"start": v(30.33, 39.17) * mm, "end": v(38.14, 31.36) * mm});
            skLineSegment(sketch, "E1255", {"start": v(38.14, 31.36) * mm, "end": v(44.07, 22.06) * mm});
            skLineSegment(sketch, "E1256", {"start": v(44.07, 22.06) * mm, "end": v(47.46, 12.97) * mm});
            skLineSegment(sketch, "E1257", {"start": v(47.46, 12.97) * mm, "end": v(49.02, 3.38) * mm});
            skLineSegment(sketch, "E1258", {"start": v(49.02, 3.38) * mm, "end": v(49.04, -2.17) * mm});
            skLineSegment(sketch, "E1259", {"start": v(49.04, -2.17) * mm, "end": v(48.53, -7.7) * mm});
            skLineSegment(sketch, "E1260", {"start": v(48.53, -7.7) * mm, "end": v(48.3, -9.18) * mm});
            skLineSegment(sketch, "E1261", {"start": v(48.3, -9.18) * mm, "end": v(47.63, -10.52) * mm});
            skLineSegment(sketch, "E1262", {"start": v(47.63, -10.52) * mm, "end": v(47.43, -11.05) * mm});
            skLineSegment(sketch, "E1263", {"start": v(47.43, -11.05) * mm, "end": v(47.36, -11.67) * mm});
            skLineSegment(sketch, "E1264", {"start": v(47.36, -11.67) * mm, "end": v(47.28, -12.88) * mm});
            skLineSegment(sketch, "E1265", {"start": v(47.28, -12.88) * mm, "end": v(47.2, -14.18) * mm});
            skLineSegment(sketch, "E1266", {"start": v(47.2, -14.18) * mm, "end": v(46.27, -13.95) * mm});
            skLineSegment(sketch, "E1267", {"start": v(46.27, -13.95) * mm, "end": v(45.47, -13.75) * mm});
            skLineSegment(sketch, "E1268", {"start": v(45.47, -13.75) * mm, "end": v(45.5, -13.53) * mm});
            skLineSegment(sketch, "E1269", {"start": v(45.5, -13.53) * mm, "end": v(45.55, -13.33) * mm});
            skLineSegment(sketch, "E1270", {"start": v(45.55, -13.33) * mm, "end": v(46.52, -9.86) * mm});
            skLineSegment(sketch, "E1271", {"start": v(46.52, -9.86) * mm, "end": v(47.24, -6.34) * mm});
            skLineSegment(sketch, "E1272", {"start": v(47.24, -6.34) * mm, "end": v(47.74, -5.2) * mm});
            skLineSegment(sketch, "E1273", {"start": v(47.74, -5.2) * mm, "end": v(48.3, -4.06) * mm});
            skLineSegment(sketch, "E1274", {"start": v(48.3, -4.06) * mm, "end": v(48.44, -3.8) * mm});
            skLineSegment(sketch, "E1275", {"start": v(48.44, -3.8) * mm, "end": v(48.63, -3.5) * mm});
            skLineSegment(sketch, "E1276", {"start": v(48.63, -3.5) * mm, "end": v(48, -3.35) * mm});
            skLineSegment(sketch, "E1277", {"start": v(48, -3.35) * mm, "end": v(47.4, -3.22) * mm});
            skLineSegment(sketch, "E1278", {"start": v(47.4, -3.22) * mm, "end": v(47.58, -2.46) * mm});
            skLineSegment(sketch, "E1279", {"start": v(47.58, -2.46) * mm, "end": v(47.77, -1.74) * mm});
            skLineSegment(sketch, "E1280", {"start": v(47.77, -1.74) * mm, "end": v(47.84, -0.25) * mm});
            skLineSegment(sketch, "E1281", {"start": v(47.84, -0.25) * mm, "end": v(47.6, 1.24) * mm});
            skLineSegment(sketch, "E1282", {"start": v(47.6, 1.24) * mm, "end": v(46.9, 7.01) * mm});
            skLineSegment(sketch, "E1283", {"start": v(46.9, 7.01) * mm, "end": v(45.78, 12.72) * mm});
            skLineSegment(sketch, "E1284", {"start": v(45.78, 12.72) * mm, "end": v(41.38, 23.55) * mm});
            skLineSegment(sketch, "E1285", {"start": v(41.38, 23.55) * mm, "end": v(34.5, 33.01) * mm});
            skLineSegment(sketch, "E1286", {"start": v(34.5, 33.01) * mm, "end": v(34.07, 33.66) * mm});
            skLineSegment(sketch, "E1287", {"start": v(34.07, 33.66) * mm, "end": v(33.66, 34.47) * mm});
            skLineSegment(sketch, "E1288", {"start": v(33.66, 34.47) * mm, "end": v(33.37, 34.86) * mm});
            skLineSegment(sketch, "E1289", {"start": v(33.37, 34.86) * mm, "end": v(32.99, 35.32) * mm});
            skLineSegment(sketch, "E1290", {"start": v(32.99, 35.32) * mm, "end": v(31.86, 36.53) * mm});
            skLineSegment(sketch, "E1291", {"start": v(31.86, 36.53) * mm, "end": v(30.32, 37.18) * mm});
            skLineSegment(sketch, "E1292", {"start": v(30.32, 37.18) * mm, "end": v(30.08, 37.24) * mm});
            skLineSegment(sketch, "E1293", {"start": v(30.08, 37.24) * mm, "end": v(29.85, 37.37) * mm});
            skLineSegment(sketch, "E1294", {"start": v(29.85, 37.37) * mm, "end": v(27.77, 38.9) * mm});
            skLineSegment(sketch, "E1295", {"start": v(27.77, 38.9) * mm, "end": v(25.66, 40.44) * mm});
            skLineSegment(sketch, "E1296", {"start": v(-40.52, -24.64) * mm, "end": v(-42.28, -24.76) * mm});
            skLineSegment(sketch, "E1297", {"start": v(-42.28, -24.76) * mm, "end": v(-43.2, -23.56) * mm});
            skLineSegment(sketch, "E1298", {"start": v(-43.2, -23.56) * mm, "end": v(-47.1, -14.3) * mm});
            skLineSegment(sketch, "E1299", {"start": v(-47.1, -14.3) * mm, "end": v(-49.03, -4.42) * mm});
            skLineSegment(sketch, "E1300", {"start": v(-49.03, -4.42) * mm, "end": v(-49.2, 2.05) * mm});
            skLineSegment(sketch, "E1301", {"start": v(-49.2, 2.05) * mm, "end": v(-48.47, 8.49) * mm});
            skLineSegment(sketch, "E1302", {"start": v(-48.47, 8.49) * mm, "end": v(-48.39, 8.88) * mm});
            skLineSegment(sketch, "E1303", {"start": v(-48.39, 8.88) * mm, "end": v(-48.28, 9.31) * mm});
            skLineSegment(sketch, "E1304", {"start": v(-48.28, 9.31) * mm, "end": v(-47.55, 9.2) * mm});
            skLineSegment(sketch, "E1305", {"start": v(-47.55, 9.2) * mm, "end": v(-46.77, 9.09) * mm});
            skLineSegment(sketch, "E1306", {"start": v(-46.77, 9.09) * mm, "end": v(-46.97, 7.25) * mm});
            skLineSegment(sketch, "E1307", {"start": v(-46.97, 7.25) * mm, "end": v(-47.88, 5.65) * mm});
            skLineSegment(sketch, "E1308", {"start": v(-47.88, 5.65) * mm, "end": v(-48.16, 5.09) * mm});
            skLineSegment(sketch, "E1309", {"start": v(-48.16, 5.09) * mm, "end": v(-48.2, 4.37) * mm});
            skLineSegment(sketch, "E1310", {"start": v(-48.2, 4.37) * mm, "end": v(-48.01, 3.5) * mm});
            skLineSegment(sketch, "E1311", {"start": v(-48.01, 3.5) * mm, "end": v(-47.72, 2.66) * mm});
            skLineSegment(sketch, "E1312", {"start": v(-47.72, 2.66) * mm, "end": v(-47.48, 2.04) * mm});
            skLineSegment(sketch, "E1313", {"start": v(-47.48, 2.04) * mm, "end": v(-47.89, 1.5) * mm});
            skLineSegment(sketch, "E1314", {"start": v(-47.89, 1.5) * mm, "end": v(-47.94, 1.28) * mm});
            skLineSegment(sketch, "E1315", {"start": v(-47.94, 1.28) * mm, "end": v(-47.93, 0.94) * mm});
            skLineSegment(sketch, "E1316", {"start": v(-47.93, 0.94) * mm, "end": v(-47.91, -0.25) * mm});
            skLineSegment(sketch, "E1317", {"start": v(-47.91, -0.25) * mm, "end": v(-47.89, -1.44) * mm});
            skLineSegment(sketch, "E1318", {"start": v(-47.89, -1.44) * mm, "end": v(-47.9, -2.91) * mm});
            skLineSegment(sketch, "E1319", {"start": v(-47.9, -2.91) * mm, "end": v(-47.38, -4.32) * mm});
            skLineSegment(sketch, "E1320", {"start": v(-47.38, -4.32) * mm, "end": v(-47.18, -4.95) * mm});
            skLineSegment(sketch, "E1321", {"start": v(-47.18, -4.95) * mm, "end": v(-47.14, -5.7) * mm});
            skLineSegment(sketch, "E1322", {"start": v(-47.14, -5.7) * mm, "end": v(-46.25, -10.9) * mm});
            skLineSegment(sketch, "E1323", {"start": v(-46.25, -10.9) * mm, "end": v(-44.78, -15.97) * mm});
            skLineSegment(sketch, "E1324", {"start": v(-44.78, -15.97) * mm, "end": v(-44.7, -16.63) * mm});
            skLineSegment(sketch, "E1325", {"start": v(-44.7, -16.63) * mm, "end": v(-44.72, -17.31) * mm});
            skLineSegment(sketch, "E1326", {"start": v(-44.72, -17.31) * mm, "end": v(-44.74, -17.45) * mm});
            skLineSegment(sketch, "E1327", {"start": v(-44.74, -17.45) * mm, "end": v(-44.73, -17.57) * mm});
            skLineSegment(sketch, "E1328", {"start": v(-44.73, -17.57) * mm, "end": v(-43.66, -19.65) * mm});
            skLineSegment(sketch, "E1329", {"start": v(-43.66, -19.65) * mm, "end": v(-42.57, -21.73) * mm});
            skLineSegment(sketch, "E1330", {"start": v(-42.57, -21.73) * mm, "end": v(-41.57, -23.13) * mm});
            skLineSegment(sketch, "E1331", {"start": v(-41.57, -23.13) * mm, "end": v(-40.52, -24.64) * mm});
            skLineSegment(sketch, "E1332", {"start": v(24.76, -41.72) * mm, "end": v(25.2, -41.5) * mm});
            skLineSegment(sketch, "E1333", {"start": v(25.2, -41.5) * mm, "end": v(25.65, -41.27) * mm});
            skLineSegment(sketch, "E1334", {"start": v(25.65, -41.27) * mm, "end": v(25.65, -41.18) * mm});
            skLineSegment(sketch, "E1335", {"start": v(25.65, -41.18) * mm, "end": v(25.65, -41.1) * mm});
            skLineSegment(sketch, "E1336", {"start": v(25.65, -41.1) * mm, "end": v(24.96, -41.02) * mm});
            skLineSegment(sketch, "E1337", {"start": v(24.96, -41.02) * mm, "end": v(24.12, -40.93) * mm});
            skLineSegment(sketch, "E1338", {"start": v(24.12, -40.93) * mm, "end": v(24.6, -40.55) * mm});
            skLineSegment(sketch, "E1339", {"start": v(24.6, -40.55) * mm, "end": v(24.94, -40.37) * mm});
            skLineSegment(sketch, "E1340", {"start": v(24.94, -40.37) * mm, "end": v(26.6, -39.74) * mm});
            skLineSegment(sketch, "E1341", {"start": v(26.6, -39.74) * mm, "end": v(27.96, -38.62) * mm});
            skLineSegment(sketch, "E1342", {"start": v(27.96, -38.62) * mm, "end": v(28.75, -38.29) * mm});
            skLineSegment(sketch, "E1343", {"start": v(28.75, -38.29) * mm, "end": v(29.75, -37.94) * mm});
            skLineSegment(sketch, "E1344", {"start": v(29.75, -37.94) * mm, "end": v(31, -35.8) * mm});
            skLineSegment(sketch, "E1345", {"start": v(31, -35.8) * mm, "end": v(33.06, -34.08) * mm});
            skLineSegment(sketch, "E1346", {"start": v(33.06, -34.08) * mm, "end": v(36.64, -30.34) * mm});
            skLineSegment(sketch, "E1347", {"start": v(36.64, -30.34) * mm, "end": v(39.56, -26.1) * mm});
            skLineSegment(sketch, "E1348", {"start": v(39.56, -26.1) * mm, "end": v(41.26, -23.36) * mm});
            skLineSegment(sketch, "E1349", {"start": v(41.26, -23.36) * mm, "end": v(42.77, -20.48) * mm});
            skLineSegment(sketch, "E1350", {"start": v(42.77, -20.48) * mm, "end": v(43.32, -19.62) * mm});
            skLineSegment(sketch, "E1351", {"start": v(43.32, -19.62) * mm, "end": v(44.46, -19.38) * mm});
            skLineSegment(sketch, "E1352", {"start": v(44.46, -19.38) * mm, "end": v(43.97, -18.97) * mm});
            skLineSegment(sketch, "E1353", {"start": v(43.97, -18.97) * mm, "end": v(43.48, -18.57) * mm});
            skLineSegment(sketch, "E1354", {"start": v(43.48, -18.57) * mm, "end": v(44.53, -18.43) * mm});
            skLineSegment(sketch, "E1355", {"start": v(44.53, -18.43) * mm, "end": v(45.43, -18.3) * mm});
            skLineSegment(sketch, "E1356", {"start": v(45.43, -18.3) * mm, "end": v(45.54, -18.4) * mm});
            skLineSegment(sketch, "E1357", {"start": v(45.54, -18.4) * mm, "end": v(45.64, -18.51) * mm});
            skLineSegment(sketch, "E1358", {"start": v(45.64, -18.51) * mm, "end": v(43.8, -22.1) * mm});
            skLineSegment(sketch, "E1359", {"start": v(43.8, -22.1) * mm, "end": v(41.87, -25.62) * mm});
            skLineSegment(sketch, "E1360", {"start": v(41.87, -25.62) * mm, "end": v(34.97, -34.5) * mm});
            skLineSegment(sketch, "E1361", {"start": v(34.97, -34.5) * mm, "end": v(26.19, -41.55) * mm});
            skLineSegment(sketch, "E1362", {"start": v(26.19, -41.55) * mm, "end": v(25.54, -41.81) * mm});
            skLineSegment(sketch, "E1363", {"start": v(25.54, -41.81) * mm, "end": v(24.85, -42) * mm});
            skLineSegment(sketch, "E1364", {"start": v(24.85, -42) * mm, "end": v(24.8, -41.86) * mm});
            skLineSegment(sketch, "E1365", {"start": v(24.8, -41.86) * mm, "end": v(24.76, -41.72) * mm});
            skLineSegment(sketch, "E1366", {"start": v(-36.46, 32.09) * mm, "end": v(-36.66, 30.28) * mm});
            skLineSegment(sketch, "E1367", {"start": v(-36.66, 30.28) * mm, "end": v(-37.77, 28.83) * mm});
            skLineSegment(sketch, "E1368", {"start": v(-37.77, 28.83) * mm, "end": v(-38.31, 28.38) * mm});
            skLineSegment(sketch, "E1369", {"start": v(-38.31, 28.38) * mm, "end": v(-39, 28.63) * mm});
            skLineSegment(sketch, "E1370", {"start": v(-39, 28.63) * mm, "end": v(-39.76, 25.96) * mm});
            skLineSegment(sketch, "E1371", {"start": v(-39.76, 25.96) * mm, "end": v(-41.38, 23.78) * mm});
            skLineSegment(sketch, "E1372", {"start": v(-41.38, 23.78) * mm, "end": v(-42.05, 22.65) * mm});
            skLineSegment(sketch, "E1373", {"start": v(-42.05, 22.65) * mm, "end": v(-42.62, 21.44) * mm});
            skLineSegment(sketch, "E1374", {"start": v(-42.62, 21.44) * mm, "end": v(-43.48, 19.95) * mm});
            skLineSegment(sketch, "E1375", {"start": v(-43.48, 19.95) * mm, "end": v(-44.72, 18.75) * mm});
            skLineSegment(sketch, "E1376", {"start": v(-44.72, 18.75) * mm, "end": v(-44.88, 18.47) * mm});
            skLineSegment(sketch, "E1377", {"start": v(-44.88, 18.47) * mm, "end": v(-44.97, 18.1) * mm});
            skLineSegment(sketch, "E1378", {"start": v(-44.97, 18.1) * mm, "end": v(-45.43, 16.74) * mm});
            skLineSegment(sketch, "E1379", {"start": v(-45.43, 16.74) * mm, "end": v(-45.91, 15.4) * mm});
            skLineSegment(sketch, "E1380", {"start": v(-45.91, 15.4) * mm, "end": v(-46.15, 15.23) * mm});
            skLineSegment(sketch, "E1381", {"start": v(-46.15, 15.23) * mm, "end": v(-46.46, 15.12) * mm});
            skLineSegment(sketch, "E1382", {"start": v(-46.46, 15.12) * mm, "end": v(-46.4, 14.22) * mm});
            skLineSegment(sketch, "E1383", {"start": v(-46.4, 14.22) * mm, "end": v(-46.33, 13.28) * mm});
            skLineSegment(sketch, "E1384", {"start": v(-46.33, 13.28) * mm, "end": v(-45.88, 12.9) * mm});
            skLineSegment(sketch, "E1385", {"start": v(-45.88, 12.9) * mm, "end": v(-46.17, 12.18) * mm});
            skLineSegment(sketch, "E1386", {"start": v(-46.17, 12.18) * mm, "end": v(-46.37, 11.68) * mm});
            skLineSegment(sketch, "E1387", {"start": v(-46.37, 11.68) * mm, "end": v(-46.53, 11) * mm});
            skLineSegment(sketch, "E1388", {"start": v(-46.53, 11) * mm, "end": v(-47.16, 10.84) * mm});
            skLineSegment(sketch, "E1389", {"start": v(-47.16, 10.84) * mm, "end": v(-48.07, 10.6) * mm});
            skLineSegment(sketch, "E1390", {"start": v(-48.07, 10.6) * mm, "end": v(-47.71, 12.13) * mm});
            skLineSegment(sketch, "E1391", {"start": v(-47.71, 12.13) * mm, "end": v(-47.35, 13.54) * mm});
            skLineSegment(sketch, "E1392", {"start": v(-47.35, 13.54) * mm, "end": v(-40.5, 27.9) * mm});
            skLineSegment(sketch, "E1393", {"start": v(-40.5, 27.9) * mm, "end": v(-29.44, 39.36) * mm});
            skLineSegment(sketch, "E1394", {"start": v(-29.44, 39.36) * mm, "end": v(-27.64, 40) * mm});
            skLineSegment(sketch, "E1395", {"start": v(-27.64, 40) * mm, "end": v(-25.73, 39.89) * mm});
            skLineSegment(sketch, "E1396", {"start": v(-25.73, 39.89) * mm, "end": v(-26.48, 39.31) * mm});
            skLineSegment(sketch, "E1397", {"start": v(-26.48, 39.31) * mm, "end": v(-27.35, 39.4) * mm});
            skLineSegment(sketch, "E1398", {"start": v(-27.35, 39.4) * mm, "end": v(-28.13, 39.59) * mm});
            skLineSegment(sketch, "E1399", {"start": v(-28.13, 39.59) * mm, "end": v(-28.75, 38.94) * mm});
            skLineSegment(sketch, "E1400", {"start": v(-28.75, 38.94) * mm, "end": v(-28.9, 38.77) * mm});
            skLineSegment(sketch, "E1401", {"start": v(-28.9, 38.77) * mm, "end": v(-29.12, 38.63) * mm});
            skLineSegment(sketch, "E1402", {"start": v(-29.12, 38.63) * mm, "end": v(-30.82, 37.38) * mm});
            skLineSegment(sketch, "E1403", {"start": v(-30.82, 37.38) * mm, "end": v(-32.05, 35.64) * mm});
            skLineSegment(sketch, "E1404", {"start": v(-32.05, 35.64) * mm, "end": v(-33.7, 33.26) * mm});
            skLineSegment(sketch, "E1405", {"start": v(-33.7, 33.26) * mm, "end": v(-36.46, 32.09) * mm});
            skLineSegment(sketch, "E1406", {"start": v(25.23, 42.5) * mm, "end": v(22.6, 42.52) * mm});
            skLineSegment(sketch, "E1407", {"start": v(22.6, 42.52) * mm, "end": v(20.18, 43.65) * mm});
            skLineSegment(sketch, "E1408", {"start": v(20.18, 43.65) * mm, "end": v(19.2, 44.13) * mm});
            skLineSegment(sketch, "E1409", {"start": v(19.2, 44.13) * mm, "end": v(18.05, 44.43) * mm});
            skLineSegment(sketch, "E1410", {"start": v(18.05, 44.43) * mm, "end": v(17.04, 44.8) * mm});
            skLineSegment(sketch, "E1411", {"start": v(17.04, 44.8) * mm, "end": v(16.3, 45.62) * mm});
            skLineSegment(sketch, "E1412", {"start": v(16.3, 45.62) * mm, "end": v(16.06, 45.76) * mm});
            skLineSegment(sketch, "E1413", {"start": v(16.06, 45.76) * mm, "end": v(15.7, 45.81) * mm});
            skLineSegment(sketch, "E1414", {"start": v(15.7, 45.81) * mm, "end": v(15.18, 45.79) * mm});
            skLineSegment(sketch, "E1415", {"start": v(15.18, 45.79) * mm, "end": v(14.62, 45.84) * mm});
            skLineSegment(sketch, "E1416", {"start": v(14.62, 45.84) * mm, "end": v(15.1, 45.97) * mm});
            skLineSegment(sketch, "E1417", {"start": v(15.1, 45.97) * mm, "end": v(15.68, 46.12) * mm});
            skLineSegment(sketch, "E1418", {"start": v(15.68, 46.12) * mm, "end": v(15.35, 46.3) * mm});
            skLineSegment(sketch, "E1419", {"start": v(15.35, 46.3) * mm, "end": v(15.1, 46.4) * mm});
            skLineSegment(sketch, "E1420", {"start": v(15.1, 46.4) * mm, "end": v(12.55, 46.9) * mm});
            skLineSegment(sketch, "E1421", {"start": v(12.55, 46.9) * mm, "end": v(10.03, 47.6) * mm});
            skLineSegment(sketch, "E1422", {"start": v(10.03, 47.6) * mm, "end": v(9, 47.63) * mm});
            skLineSegment(sketch, "E1423", {"start": v(9, 47.63) * mm, "end": v(7.86, 47.4) * mm});
            skLineSegment(sketch, "E1424", {"start": v(7.86, 47.4) * mm, "end": v(7.3, 47.33) * mm});
            skLineSegment(sketch, "E1425", {"start": v(7.3, 47.33) * mm, "end": v(6.72, 47.3) * mm});
            skLineSegment(sketch, "E1426", {"start": v(6.72, 47.3) * mm, "end": v(5.49, 47.67) * mm});
            skLineSegment(sketch, "E1427", {"start": v(5.49, 47.67) * mm, "end": v(5.25, 49.1) * mm});
            skLineSegment(sketch, "E1428", {"start": v(5.25, 49.1) * mm, "end": v(15.63, 46.98) * mm});
            skLineSegment(sketch, "E1429", {"start": v(15.63, 46.98) * mm, "end": v(25.23, 42.5) * mm});
            skLineSegment(sketch, "E1430", {"start": v(4.05, 49.12) * mm, "end": v(3.8, 47.78) * mm});
            skLineSegment(sketch, "E1431", {"start": v(3.8, 47.78) * mm, "end": v(2.53, 47.67) * mm});
            skLineSegment(sketch, "E1432", {"start": v(2.53, 47.67) * mm, "end": v(1.24, 47.86) * mm});
            skLineSegment(sketch, "E1433", {"start": v(1.24, 47.86) * mm, "end": v(-0.06, 48.02) * mm});
            skLineSegment(sketch, "E1434", {"start": v(-0.06, 48.02) * mm, "end": v(-1.33, 47.95) * mm});
            skLineSegment(sketch, "E1435", {"start": v(-1.33, 47.95) * mm, "end": v(-2.61, 47.84) * mm});
            skLineSegment(sketch, "E1436", {"start": v(-2.61, 47.84) * mm, "end": v(-3.78, 47.9) * mm});
            skLineSegment(sketch, "E1437", {"start": v(-3.78, 47.9) * mm, "end": v(-4.95, 47.97) * mm});
            skLineSegment(sketch, "E1438", {"start": v(-4.95, 47.97) * mm, "end": v(-5.85, 48) * mm});
            skLineSegment(sketch, "E1439", {"start": v(-5.85, 48) * mm, "end": v(-6.75, 47.96) * mm});
            skLineSegment(sketch, "E1440", {"start": v(-6.75, 47.96) * mm, "end": v(-8.13, 47.65) * mm});
            skLineSegment(sketch, "E1441", {"start": v(-8.13, 47.65) * mm, "end": v(-9.52, 47.36) * mm});
            skLineSegment(sketch, "E1442", {"start": v(-9.52, 47.36) * mm, "end": v(-10.23, 47.4) * mm});
            skLineSegment(sketch, "E1443", {"start": v(-10.23, 47.4) * mm, "end": v(-11.1, 47.56) * mm});
            skLineSegment(sketch, "E1444", {"start": v(-11.1, 47.56) * mm, "end": v(-11.42, 47.15) * mm});
            skLineSegment(sketch, "E1445", {"start": v(-11.42, 47.15) * mm, "end": v(-11.9, 46.54) * mm});
            skLineSegment(sketch, "E1446", {"start": v(-11.9, 46.54) * mm, "end": v(-12.45, 47.13) * mm});
            skLineSegment(sketch, "E1447", {"start": v(-12.45, 47.13) * mm, "end": v(-13.2, 46.98) * mm});
            skLineSegment(sketch, "E1448", {"start": v(-13.2, 46.98) * mm, "end": v(-14.22, 46.68) * mm});
            skLineSegment(sketch, "E1449", {"start": v(-14.22, 46.68) * mm, "end": v(-15.22, 46.33) * mm});
            skLineSegment(sketch, "E1450", {"start": v(-15.22, 46.33) * mm, "end": v(-15.77, 45.93) * mm});
            skLineSegment(sketch, "E1451", {"start": v(-15.77, 45.93) * mm, "end": v(-16.27, 45.42) * mm});
            skLineSegment(sketch, "E1452", {"start": v(-16.27, 45.42) * mm, "end": v(-16.44, 45.2) * mm});
            skLineSegment(sketch, "E1453", {"start": v(-16.44, 45.2) * mm, "end": v(-16.6, 45.05) * mm});
            skLineSegment(sketch, "E1454", {"start": v(-16.6, 45.05) * mm, "end": v(-18.46, 44.63) * mm});
            skLineSegment(sketch, "E1455", {"start": v(-18.46, 44.63) * mm, "end": v(-20.3, 44.22) * mm});
            skLineSegment(sketch, "E1456", {"start": v(-20.3, 44.22) * mm, "end": v(-20.57, 44.2) * mm});
            skLineSegment(sketch, "E1457", {"start": v(-20.57, 44.2) * mm, "end": v(-20.88, 44.22) * mm});
            skLineSegment(sketch, "E1458", {"start": v(-20.88, 44.22) * mm, "end": v(-9.6, 48.16) * mm});
            skLineSegment(sketch, "E1459", {"start": v(-9.6, 48.16) * mm, "end": v(4.05, 49.12) * mm});
            skLineSegment(sketch, "E1460", {"start": v(-41.93, -25.68) * mm, "end": v(-39.99, -25.75) * mm});
            skLineSegment(sketch, "E1461", {"start": v(-39.99, -25.75) * mm, "end": v(-39.68, -27.25) * mm});
            skLineSegment(sketch, "E1462", {"start": v(-39.68, -27.25) * mm, "end": v(-39, -27.58) * mm});
            skLineSegment(sketch, "E1463", {"start": v(-39, -27.58) * mm, "end": v(-38.2, -27.95) * mm});
            skLineSegment(sketch, "E1464", {"start": v(-38.2, -27.95) * mm, "end": v(-39.8, -28.4) * mm});
            skLineSegment(sketch, "E1465", {"start": v(-39.8, -28.4) * mm, "end": v(-40.82, -27.4) * mm});
            skLineSegment(sketch, "E1466", {"start": v(-40.82, -27.4) * mm, "end": v(-41.37, -26.55) * mm});
            skLineSegment(sketch, "E1467", {"start": v(-41.37, -26.55) * mm, "end": v(-41.93, -25.68) * mm});
            skLineSegment(sketch, "E1468", {"start": v(46.4, -15.55) * mm, "end": v(46.19, -16.56) * mm});
            skLineSegment(sketch, "E1469", {"start": v(46.19, -16.56) * mm, "end": v(45.98, -17.52) * mm});
            skLineSegment(sketch, "E1470", {"start": v(45.98, -17.52) * mm, "end": v(45.07, -17.52) * mm});
            skLineSegment(sketch, "E1471", {"start": v(45.07, -17.52) * mm, "end": v(44.23, -17.52) * mm});
            skLineSegment(sketch, "E1472", {"start": v(44.23, -17.52) * mm, "end": v(44.8, -15.8) * mm});
            skLineSegment(sketch, "E1473", {"start": v(44.8, -15.8) * mm, "end": v(46.4, -15.55) * mm});
            skLineSegment(sketch, "E1474", {"start": v(-20.14, 43.05) * mm, "end": v(-22.5, 42.27) * mm});
            skLineSegment(sketch, "E1475", {"start": v(-22.5, 42.27) * mm, "end": v(-24.87, 42.17) * mm});
            skLineSegment(sketch, "E1476", {"start": v(-24.87, 42.17) * mm, "end": v(-22.65, 43.25) * mm});
            skLineSegment(sketch, "E1477", {"start": v(-22.65, 43.25) * mm, "end": v(-20.14, 43.05) * mm});
            skSolve(sketch);
        }
        {
            var Q0;
            Q0=makeQuery(id+"F0.imprint","IMPRINT",FACE,{"disambiguationData":[TD([[makeQuery(id+"F0.imprint","IMPRINT",EDGE,{"derivedFrom":sQuery(id+"F0.wireOp",EDGE,"E0")}),-1.0]])]});
            var Q1;
            Q1=makeQuery(id+"F0.imprint","IMPRINT",FACE,{"disambiguationData":[TD([[makeQuery(id+"F0.imprint","IMPRINT",EDGE,{"derivedFrom":sQuery(id+"F0.wireOp",EDGE,"E460")}),-1.0]])]});
            var Q2;
            Q2=makeQuery(id+"F0.imprint","IMPRINT",FACE,{"disambiguationData":[TD([[makeQuery(id+"F0.imprint","IMPRINT",EDGE,{"derivedFrom":sQuery(id+"F0.wireOp",EDGE,"E584")}),-1.0]])]});
            var Q3;
            Q3=makeQuery(id+"F0.imprint","IMPRINT",FACE,{"disambiguationData":[TD([[makeQuery(id+"F0.imprint","IMPRINT",EDGE,{"derivedFrom":sQuery(id+"F0.wireOp",EDGE,"E976")}),-1.0]])]});
            var Q4;
            Q4=makeQuery(id+"F0.imprint","IMPRINT",FACE,{"disambiguationData":[TD([[makeQuery(id+"F0.imprint","IMPRINT",EDGE,{"derivedFrom":sQuery(id+"F0.wireOp",EDGE,"E720")}),-1.0]])]});
            var Q5;
            Q5=makeQuery(id+"F0.imprint","IMPRINT",FACE,{"disambiguationData":[TD([[makeQuery(id+"F0.imprint","IMPRINT",EDGE,{"derivedFrom":sQuery(id+"F0.wireOp",EDGE,"E1104")}),-1.0]])]});
            var Q6;
            Q6=makeQuery(id+"F0.imprint","IMPRINT",FACE,{"disambiguationData":[TD([[makeQuery(id+"F0.imprint","IMPRINT",EDGE,{"derivedFrom":sQuery(id+"F0.wireOp",EDGE,"E654")}),-1.0]])]});
            var Q7;
            Q7=makeQuery(id+"F0.imprint","IMPRINT",FACE,{"disambiguationData":[TD([[makeQuery(id+"F0.imprint","IMPRINT",EDGE,{"derivedFrom":sQuery(id+"F0.wireOp",EDGE,"E686")}),-1.0]])]});
            var Q8;
            Q8=makeQuery(id+"F0.imprint","IMPRINT",FACE,{"disambiguationData":[TD([[makeQuery(id+"F0.imprint","IMPRINT",EDGE,{"derivedFrom":sQuery(id+"F0.wireOp",EDGE,"E630")}),-1.0]])]});
            var Q9;
            Q9=makeQuery(id+"F0.imprint","IMPRINT",FACE,{"disambiguationData":[TD([[makeQuery(id+"F0.imprint","IMPRINT",EDGE,{"derivedFrom":sQuery(id+"F0.wireOp",EDGE,"E1406")}),-1.0]])]});
            var Q10;
            Q10=makeQuery(id+"F0.imprint","IMPRINT",FACE,{"disambiguationData":[TD([[makeQuery(id+"F0.imprint","IMPRINT",EDGE,{"derivedFrom":sQuery(id+"F0.wireOp",EDGE,"E1252")}),-1.0]])]});
            var Q11;
            Q11=makeQuery(id+"F0.imprint","IMPRINT",FACE,{"disambiguationData":[TD([[makeQuery(id+"F0.imprint","IMPRINT",EDGE,{"derivedFrom":sQuery(id+"F0.wireOp",EDGE,"E1468")}),-1.0]])]});
            var Q12;
            Q12=makeQuery(id+"F0.imprint","IMPRINT",FACE,{"disambiguationData":[TD([[makeQuery(id+"F0.imprint","IMPRINT",EDGE,{"derivedFrom":sQuery(id+"F0.wireOp",EDGE,"E1332")}),-1.0]])]});
            var Q13;
            Q13=makeQuery(id+"F0.imprint","IMPRINT",FACE,{"disambiguationData":[TD([[makeQuery(id+"F0.imprint","IMPRINT",EDGE,{"derivedFrom":sQuery(id+"F0.wireOp",EDGE,"E1192")}),-1.0]])]});
            var Q14;
            Q14=makeQuery(id+"F0.imprint","IMPRINT",FACE,{"disambiguationData":[TD([[makeQuery(id+"F0.imprint","IMPRINT",EDGE,{"derivedFrom":sQuery(id+"F0.wireOp",EDGE,"E1296")}),-1.0]])]});
            var Q15;
            Q15=makeQuery(id+"F0.imprint","IMPRINT",FACE,{"disambiguationData":[TD([[makeQuery(id+"F0.imprint","IMPRINT",EDGE,{"derivedFrom":sQuery(id+"F0.wireOp",EDGE,"E1460")}),-1.0]])]});
            var Q16;
            {var subQ4=sQuery(id+"F0.wireOp",EDGE,"E1367");Q16=makeQuery(id+"F0.imprint","IMPRINT",FACE,{"disambiguationData":[TD([[makeQuery(id+"F0.imprint","IMPRINT",EDGE,{"derivedFrom":subQ4}),-1.0]])]});}
            var Q17;
            {var subQ4=sQuery(id+"F0.wireOp",EDGE,"E1394");Q17=makeQuery(id+"F0.imprint","IMPRINT",FACE,{"disambiguationData":[TD([[makeQuery(id+"F0.imprint","IMPRINT",EDGE,{"derivedFrom":subQ4}),-1.0]])]});}
            var Q18;
            Q18=makeQuery(id+"F0.imprint","IMPRINT",FACE,{"disambiguationData":[TD([[makeQuery(id+"F0.imprint","IMPRINT",EDGE,{"derivedFrom":sQuery(id+"F0.wireOp",EDGE,"E1474")}),-1.0]])]});
            var Q19;
            Q19=makeQuery(id+"F0.imprint","IMPRINT",FACE,{"disambiguationData":[TD([[makeQuery(id+"F0.imprint","IMPRINT",EDGE,{"derivedFrom":sQuery(id+"F0.wireOp",EDGE,"E1430")}),-1.0]])]});
            var Q20;
            {var subQ4=sQuery(id+"F0.wireOp",EDGE,"E1451");Q20=makeQuery(id+"F0.imprint","IMPRINT",FACE,{"disambiguationData":[TD([[makeQuery(id+"F0.imprint","IMPRINT",EDGE,{"derivedFrom":subQ4}),-1.0]])]});}
            extrude(context, id + "F1", {"entities" : qUnion([Q0, Q1, Q2, Q3, Q4, Q5, Q6, Q7, Q8, Q9, Q10, Q11, Q12, Q13, Q14, Q15, Q16, Q17, Q18, Q19, Q20]), "depth" : 6.35 * mm});
        }
        {
            var Q0;
            Q0=qCreatedBy(makeId("Top.planeOp"),FACE);
            var sketch = newSketch(context, id + "F2", { "sketchPlane" : qUnion([Q0])});
            skCircle(sketch, "E1478", {"center": v(0, 0) * mm, "radius": 69.25 * mm});
            skSolve(sketch);
        }
        {
            var Q0;
            Q0=makeQuery(id+"F2.imprint","IMPRINT",FACE,{"disambiguationData":[TD([[makeQuery(id+"F2.imprint","IMPRINT",EDGE,{"derivedFrom":sQuery(id+"F2.wireOp",EDGE,"E1478")}),1.0]])]});
            extrude(context, id + "F3", {"entities" : qUnion([Q0]), "oppositeDirection" : true, "depth" : 5.98 * mm});
        }
    });
